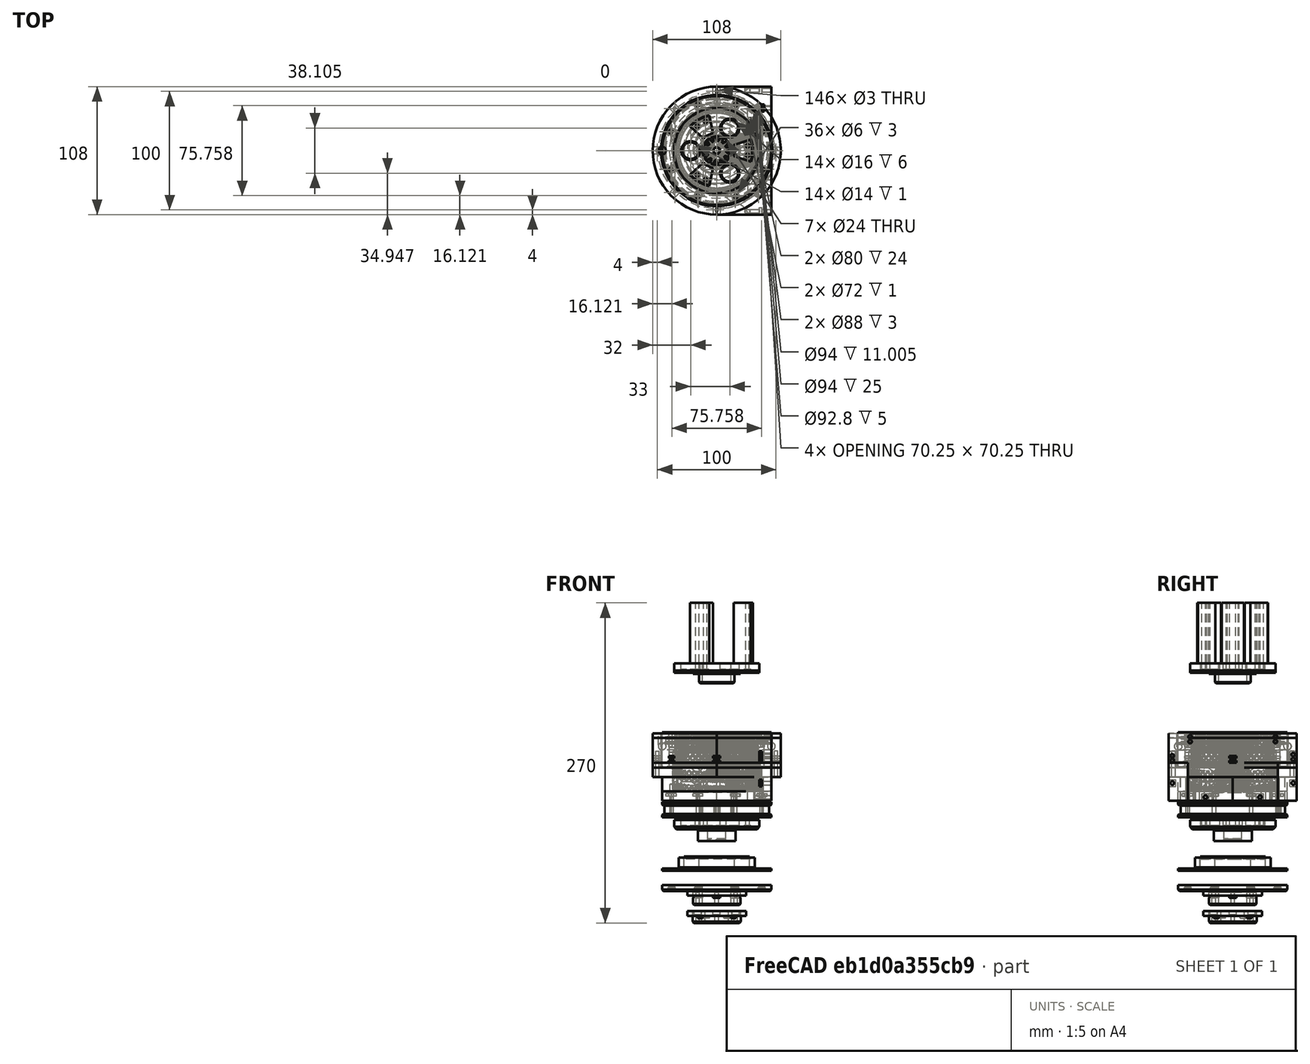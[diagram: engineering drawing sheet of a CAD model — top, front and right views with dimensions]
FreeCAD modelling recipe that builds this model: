
FCSTD DOCUMENT  (FreeCAD 0.19R24276 (Git))
Label: J-midi-deep_048
License: All rights reserved
LicenseURL: http://en.wikipedia.org/wiki/All_rights_reserved
objects: Part::Cylinder×435, Part::Box×228, Part::Compound×200, Part::Cut×185, Part::FeaturePython×106, Part::Chamfer×20, Part::Wedge×20, Mesh::Feature×7, Part::Torus×6, Part::Fillet×2, Part::Mirroring×1, Part::Common×1
note: 1204 computed .brp shape members not serialized (recipe doc carries the construction recipe); baked Part::Feature solids carry a one-line shape summary decoded from their .brp

FEATURE [Part::Cylinder] Cylinder714  label="Válec714"
  Angle = 360
  AttacherType = Attacher::AttachEngine3D
  Height = 60
  Placement = pos=(41,0,-54) rot=(0,0,1;0rad)
  Radius = 1.5
FEATURE [Part::Cylinder] Cylinder715  label="Válec715"
  Angle = 360
  AttacherType = Attacher::AttachEngine3D
  Height = 40
  Placement = pos=(202,50,-28) rot=(0,0,1;0rad)
  Radius = 12
FEATURE [Part::Box] Box334  label="Krychle334"
  AttacherType = Attacher::AttachEngine3D
  Height = 2
  Length = 8
  Placement = pos=(37,-3,-4) rot=(0,0,1;0rad)
  Width = 6
FEATURE [Part::Cylinder] Cylinder716  label="Válec716"
  Angle = 360
  AttacherType = Attacher::AttachEngine3D
  Height = 40
  Placement = pos=(214,56,-30) rot=(0,0,1;0rad)
  Radius = 12
FEATURE [Part::Cylinder] Cylinder717  label="Válec717"
  Angle = 360
  AttacherType = Attacher::AttachEngine3D
  Height = 12
  Radius = 46
FEATURE [Part::Box] Box335  label="Krychle335"
  AttacherType = Attacher::AttachEngine3D
  Height = 28
  Length = 6
  Placement = pos=(26,28,-8) rot=(0,0,1;0rad)
  Width = 10
FEATURE [Part::Cylinder] Cylinder718  label="Válec718"
  Angle = 360
  AttacherType = Attacher::AttachEngine3D
  Height = 40
  Placement = pos=(256,0,-30) rot=(0,0,1;0rad)
  Radius = 10
FEATURE [Part::Box] Box336  label="Krychle336"
  AttacherType = Attacher::AttachEngine3D
  Height = 32
  Length = 8
  Placement = pos=(238,0,-8) rot=(0,0,1;0rad)
  Width = 38
FEATURE [Part::Cylinder] Cylinder719  label="Válec719"
  Angle = 360
  AttacherType = Attacher::AttachEngine3D
  Height = 12
  Radius = 54
FEATURE [Part::Box] Box337  label="Krychle337"
  AttacherType = Attacher::AttachEngine3D
  Height = 28
  Length = 6
  Placement = pos=(32,24,-8) rot=(0,0,1;0rad)
  Width = 14
FEATURE [Part::Cylinder] Cylinder720  label="Válec720"
  Angle = 360
  AttacherType = Attacher::AttachEngine3D
  Height = 40
  Placement = pos=(202,50,-28) rot=(0,0,1;0rad)
  Radius = 12
FEATURE [Part::Box] Box338  label="Krychle338"
  AttacherType = Attacher::AttachEngine3D
  Height = 32
  Length = 8
  Placement = pos=(238,0,-8) rot=(0,0,1;0rad)
  Width = 38
FEATURE [Part::Box] Box339  label="Krychle339"
  AttacherType = Attacher::AttachEngine3D
  Height = 2
  Length = 8
  Placement = pos=(28.2843,24.0416,-4) rot=(0,0,1;0.785398rad)
  Width = 6
FEATURE [Part::Box] Box340  label="Krychle340"
  AttacherType = Attacher::AttachEngine3D
  Height = 2
  Length = 8
  Placement = pos=(-28.2843,-24.0416,-4) rot=(0,0,1;3.92699rad)
  Width = 6
FEATURE [Part::Cylinder] Cylinder721  label="Válec721"
  Angle = 360
  AttacherType = Attacher::AttachEngine3D
  Height = 40
  Placement = pos=(214,56,-30) rot=(0,0,1;0rad)
  Radius = 12
FEATURE [Part::Box] Box341  label="Krychle341"
  AttacherType = Attacher::AttachEngine3D
  Height = 28
  Length = 6
  Placement = pos=(26,28,-8) rot=(0,0,1;0rad)
  Width = 10
FEATURE [Part::Compound] Compound705
  Links = -> [Box341,Box337]
FEATURE [Part::Box] Box342  label="Krychle342"
  AttacherType = Attacher::AttachEngine3D
  Height = 32
  Length = 46
  Placement = pos=(200,38,-8) rot=(0,0,1;0rad)
  Width = 16
FEATURE [Part::Compound] Compound709
  Links = -> [Box336,Box342]
FEATURE [Part::Box] Box343  label="Krychle343"
  AttacherType = Attacher::AttachEngine3D
  Height = 28
  Length = 6
  Placement = pos=(32,24,-8) rot=(0,0,1;0rad)
  Width = 14
FEATURE [Part::Box] Box344  label="Krychle344"
  AttacherType = Attacher::AttachEngine3D
  Height = 2
  Length = 8
  Placement = pos=(3,37,-4) rot=(0,0,1;1.5708rad)
  Width = 6
FEATURE [Part::Cylinder] Cylinder722  label="Válec722"
  Angle = 360
  AttacherType = Attacher::AttachEngine3D
  Height = 40
  Placement = pos=(256,0,-30) rot=(0,0,1;0rad)
  Radius = 10
FEATURE [Part::Cylinder] Cylinder723  label="Válec723"
  Angle = 360
  AttacherType = Attacher::AttachEngine3D
  Height = 60
  Placement = pos=(28.9914,28.9914,-54) rot=(0,0,1;0.785398rad)
  Radius = 1.5
FEATURE [Part::Box] Box345  label="Krychle345"
  AttacherType = Attacher::AttachEngine3D
  Height = 32
  Length = 46
  Placement = pos=(200,38,-8) rot=(0,0,1;0rad)
  Width = 16
FEATURE [Part::Compound] Compound706
  Links = -> [Box338,Box345]
FEATURE [Part::Box] Box346  label="Krychle346"
  AttacherType = Attacher::AttachEngine3D
  Height = 2
  Length = 8
  Placement = pos=(24.0416,-28.2843,-4) rot=(0,0,-1;0.785398rad)
  Width = 6
FEATURE [Part::Cylinder] Cylinder724  label="Válec724"
  Angle = 360
  AttacherType = Attacher::AttachEngine3D
  Height = 60
  Placement = pos=(28.9914,-28.9914,-54) rot=(0,0,-1;0.785398rad)
  Radius = 1.5
FEATURE [Part::Box] Box347  label="Krychle347"
  AttacherType = Attacher::AttachEngine3D
  Height = 2
  Length = 8
  Placement = pos=(-3,-37,-4) rot=(0,0,-1;1.5708rad)
  Width = 6
FEATURE [Part::Cylinder] Cylinder725  label="Válec725"
  Angle = 360
  AttacherType = Attacher::AttachEngine3D
  Height = 60
  Placement = pos=(-41,-1.1e-14,-54) rot=(0,0,1;3.14159rad)
  Radius = 1.5
FEATURE [Part::Cylinder] Cylinder726  label="Válec726"
  Angle = 360
  AttacherType = Attacher::AttachEngine3D
  Height = 60
  Placement = pos=(1.2e-14,-41,-54) rot=(0,0,-1;1.5708rad)
  Radius = 1.5
FEATURE [Part::Cylinder] Cylinder727  label="Válec727"
  Angle = 360
  AttacherType = Attacher::AttachEngine3D
  Height = 60
  Placement = pos=(-28.9914,-28.9914,-54) rot=(0,0,1;3.92699rad)
  Radius = 1.5
FEATURE [Part::Cylinder] Cylinder728  label="Válec728"
  Angle = 360
  AttacherType = Attacher::AttachEngine3D
  Height = 60
  Placement = pos=(28.9914,-28.9914,-54) rot=(0,0,-1;0.785398rad)
  Radius = 1.5
FEATURE [Part::Box] Box348  label="Krychle348"
  AttacherType = Attacher::AttachEngine3D
  Height = 2
  Length = 8
  Placement = pos=(37,-3,-4) rot=(0,0,1;0rad)
  Width = 6
FEATURE [Part::Cylinder] Cylinder729  label="Válec729"
  Angle = 360
  AttacherType = Attacher::AttachEngine3D
  Height = 60
  Placement = pos=(41,0,-54) rot=(0,0,1;0rad)
  Radius = 1.5
FEATURE [Part::Box] Box349  label="Krychle349"
  AttacherType = Attacher::AttachEngine3D
  Height = 2
  Length = 8
  Placement = pos=(-37,3,-4) rot=(0,0,1;3.14159rad)
  Width = 6
FEATURE [Part::Cylinder] Cylinder730  label="Válec730"
  Angle = 360
  AttacherType = Attacher::AttachEngine3D
  Height = 60
  Placement = pos=(1.2e-14,-41,-54) rot=(0,0,-1;1.5708rad)
  Radius = 1.5
FEATURE [Part::Box] Box350  label="Krychle350"
  AttacherType = Attacher::AttachEngine3D
  Height = 2
  Length = 8
  Placement = pos=(28.2843,24.0416,-4) rot=(0,0,1;0.785398rad)
  Width = 6
FEATURE [Part::Box] Box351  label="Krychle351"
  AttacherType = Attacher::AttachEngine3D
  Height = 2
  Length = 8
  Placement = pos=(-28.2843,-24.0416,-4) rot=(0,0,1;3.92699rad)
  Width = 6
FEATURE [Part::Cylinder] Cylinder731  label="Válec731"
  Angle = 360
  AttacherType = Attacher::AttachEngine3D
  Height = 60
  Placement = pos=(-4e-15,41,-54) rot=(0,0,1;1.5708rad)
  Radius = 1.5
FEATURE [Part::Box] Box352  label="Krychle352"
  AttacherType = Attacher::AttachEngine3D
  Height = 2
  Length = 8
  Placement = pos=(-3,-37,-4) rot=(0,0,-1;1.5708rad)
  Width = 6
FEATURE [Part::Box] Box353  label="Krychle353"
  AttacherType = Attacher::AttachEngine3D
  Height = 2
  Length = 8
  Placement = pos=(-24.0416,28.2843,-4) rot=(0,0,1;2.35619rad)
  Width = 6
FEATURE [Part::Cylinder] Cylinder732  label="Válec732"
  Angle = 360
  AttacherType = Attacher::AttachEngine3D
  Height = 60
  Placement = pos=(-28.9914,28.9914,-54) rot=(0,0,1;2.35619rad)
  Radius = 1.5
FEATURE [Part::Cylinder] Cylinder733  label="Válec733"
  Angle = 360
  AttacherType = Attacher::AttachEngine3D
  Height = 60
  Placement = pos=(28.9914,-28.9914,-54) rot=(0,0,-1;0.785398rad)
  Radius = 1.5
FEATURE [Part::Box] Box354  label="Krychle354"
  AttacherType = Attacher::AttachEngine3D
  Height = 2
  Length = 8
  Placement = pos=(-24.0416,28.2843,-4) rot=(0,0,1;2.35619rad)
  Width = 6
FEATURE [Part::Cylinder] Cylinder734  label="Válec734"
  Angle = 360
  AttacherType = Attacher::AttachEngine3D
  Height = 60
  Placement = pos=(-41,-1.1e-14,-54) rot=(0,0,1;3.14159rad)
  Radius = 1.5
FEATURE [Part::Cylinder] Cylinder735  label="Válec735"
  Angle = 360
  AttacherType = Attacher::AttachEngine3D
  Height = 60
  Placement = pos=(28.9914,28.9914,-54) rot=(0,0,1;0.785398rad)
  Radius = 1.5
FEATURE [Part::Box] Box355  label="Krychle355"
  AttacherType = Attacher::AttachEngine3D
  Height = 2
  Length = 8
  Placement = pos=(24.0416,-28.2843,-4) rot=(0,0,-1;0.785398rad)
  Width = 6
FEATURE [Part::Cylinder] Cylinder736  label="Válec736"
  Angle = 360
  AttacherType = Attacher::AttachEngine3D
  Height = 60
  Placement = pos=(-28.9914,28.9914,-54) rot=(0,0,1;2.35619rad)
  Radius = 1.5
FEATURE [Part::Cylinder] Cylinder737  label="Válec737"
  Angle = 360
  AttacherType = Attacher::AttachEngine3D
  Height = 60
  Placement = pos=(-4e-15,41,-54) rot=(0,0,1;1.5708rad)
  Radius = 1.5
FEATURE [Part::Box] Box356  label="Krychle356"
  AttacherType = Attacher::AttachEngine3D
  Height = 2
  Length = 8
  Placement = pos=(3,37,-4) rot=(0,0,1;1.5708rad)
  Width = 6
FEATURE [Part::Cylinder] Cylinder738  label="Válec738"
  Angle = 360
  AttacherType = Attacher::AttachEngine3D
  Height = 60
  Placement = pos=(-28.9914,-28.9914,-54) rot=(0,0,1;3.92699rad)
  Radius = 1.5
FEATURE [Part::Cylinder] Cylinder739  label="Válec739"
  Angle = 360
  AttacherType = Attacher::AttachEngine3D
  Height = 60
  Placement = pos=(28,-51,7) rot=(0,1,0;1.5708rad)
  Radius = 1.5
FEATURE [Part::Cylinder] Cylinder740  label="Válec740"
  Angle = 360
  AttacherType = Attacher::AttachEngine3D
  Height = 60
  Placement = pos=(-4e-15,41,-54) rot=(0,0,1;1.5708rad)
  Radius = 1.5
FEATURE [Part::Box] Box357  label="Krychle357"
  AttacherType = Attacher::AttachEngine3D
  Height = 2
  Length = 8
  Placement = pos=(-37,3,-4) rot=(0,0,1;3.14159rad)
  Width = 6
FEATURE [Part::Box] Box358  label="Krychle358"
  AttacherType = Attacher::AttachEngine3D
  Height = 6
  Length = 2
  Placement = pos=(36,18,-8) rot=(0,0,1;0rad)
  Width = 6
FEATURE [Part::Box] Box359  label="Krychle359"
  AttacherType = Attacher::AttachEngine3D
  Height = 6
  Length = 2
  Placement = pos=(32,-54,4) rot=(0,0,1;0rad)
  Width = 6
FEATURE [Part::Cylinder] Cylinder741  label="Válec741"
  Angle = 360
  AttacherType = Attacher::AttachEngine3D
  Height = 50
  Placement = pos=(-50,-2.3e-14,-15) rot=(0,0,1;3.14159rad)
  Radius = 1.5
FEATURE [Part::Cylinder] Cylinder742  label="Válec742"
  Angle = 360
  AttacherType = Attacher::AttachEngine3D
  Height = 60
  Placement = pos=(28,51,7) rot=(0,1,0;1.5708rad)
  Radius = 1.5
FEATURE [Part::Box] Box360  label="Krychle360"
  AttacherType = Attacher::AttachEngine3D
  Height = 6
  Length = 2
  Placement = pos=(36,20,-8) rot=(0,0,1;0rad)
  Width = 6
FEATURE [Part::Cylinder] Cylinder743  label="Válec743"
  Angle = 360
  AttacherType = Attacher::AttachEngine3D
  Height = 60
  Placement = pos=(41,0,-54) rot=(0,0,1;0rad)
  Radius = 1.5
FEATURE [Part::Cylinder] Cylinder744  label="Válec744"
  Angle = 360
  AttacherType = Attacher::AttachEngine3D
  Height = 60
  Placement = pos=(-28.9914,-28.9914,-54) rot=(0,0,1;3.92699rad)
  Radius = 1.5
FEATURE [Part::Cylinder] Cylinder745  label="Válec745"
  Angle = 360
  AttacherType = Attacher::AttachEngine3D
  Height = 60
  Placement = pos=(28,-51,7) rot=(0,1,0;1.5708rad)
  Radius = 1.5
FEATURE [Part::Box] Box361  label="Krychle361"
  AttacherType = Attacher::AttachEngine3D
  Height = 6
  Length = 2
  Placement = pos=(32,-54,4) rot=(0,0,1;0rad)
  Width = 6
FEATURE [Part::Cylinder] Cylinder746  label="Válec746"
  Angle = 360
  AttacherType = Attacher::AttachEngine3D
  Height = 60
  Placement = pos=(-28.9914,28.9914,-54) rot=(0,0,1;2.35619rad)
  Radius = 1.5
FEATURE [Part::Cylinder] Cylinder747  label="Válec747"
  Angle = 360
  AttacherType = Attacher::AttachEngine3D
  Height = 60
  Placement = pos=(32,-21,-5) rot=(0,1,0;1.5708rad)
  Radius = 1.5
FEATURE [Part::Box] Box362  label="Krychle362"
  AttacherType = Attacher::AttachEngine3D
  Height = 6
  Length = 2
  Placement = pos=(36,-24,-8) rot=(0,0,1;0rad)
  Width = 6
FEATURE [Part::Cylinder] Cylinder748  label="Válec748"
  Angle = 360
  AttacherType = Attacher::AttachEngine3D
  Height = 60
  Placement = pos=(1.2e-14,-41,-54) rot=(0,0,-1;1.5708rad)
  Radius = 1.5
FEATURE [Part::Box] Box363  label="Krychle363"
  AttacherType = Attacher::AttachEngine3D
  Height = 6
  Length = 2
  Placement = pos=(32,48,4) rot=(0,0,1;0rad)
  Width = 6
FEATURE [Part::Compound] Compound703
  Links = -> [Box358,Box362,Box363,Box359]
FEATURE [Part::Cylinder] Cylinder749  label="Válec749"
  Angle = 360
  AttacherType = Attacher::AttachEngine3D
  Height = 60
  Placement = pos=(28.9914,28.9914,-54) rot=(0,0,1;0.785398rad)
  Radius = 1.5
FEATURE [Part::Cylinder] Cylinder750  label="Válec750"
  Angle = 360
  AttacherType = Attacher::AttachEngine3D
  Height = 60
  Placement = pos=(32,21,-5) rot=(0,1,0;1.5708rad)
  Radius = 1.5
FEATURE [Part::Compound] Compound710
  Links = -> [Cylinder750,Cylinder747,Cylinder742,Cylinder739]
FEATURE [Part::Cylinder] Cylinder751  label="Válec751"
  Angle = 360
  AttacherType = Attacher::AttachEngine3D
  Height = 60
  Placement = pos=(-41,-1.1e-14,-54) rot=(0,0,1;3.14159rad)
  Radius = 1.5
FEATURE [Part::Cylinder] Cylinder752  label="Válec752"
  Angle = 360
  AttacherType = Attacher::AttachEngine3D
  Height = 50
  Placement = pos=(50,0,-15) rot=(0,0,1;0rad)
  Radius = 1.5
FEATURE [Part::Box] Box364  label="Krychle364"
  AttacherType = Attacher::AttachEngine3D
  Height = 6
  Length = 2
  Placement = pos=(32,48,4) rot=(0,0,1;0rad)
  Width = 6
FEATURE [Part::Box] Box365  label="Krychle365"
  AttacherType = Attacher::AttachEngine3D
  Height = 6
  Length = 2
  Placement = pos=(36,-26,-8) rot=(0,0,1;0rad)
  Width = 6
FEATURE [Part::Cylinder] Cylinder753  label="Válec753"
  Angle = 360
  AttacherType = Attacher::AttachEngine3D
  Height = 60
  Placement = pos=(32,23,-5) rot=(0,1,0;1.5708rad)
  Radius = 1.5
FEATURE [Part::Cylinder] Cylinder754  label="Válec754"
  Angle = 360
  AttacherType = Attacher::AttachEngine3D
  Height = 50
  Placement = pos=(2.5e-14,-50,-15) rot=(0,0,-1;1.5708rad)
  Radius = 1.5
FEATURE [Part::Cylinder] Cylinder755  label="Válec755"
  Angle = 360
  AttacherType = Attacher::AttachEngine3D
  Height = 50
  Placement = pos=(-35.3553,-35.3553,-15) rot=(0,0,1;3.92699rad)
  Radius = 1.5
FEATURE [Part::Cylinder] Cylinder756  label="Válec756"
  Angle = 360
  AttacherType = Attacher::AttachEngine3D
  Height = 50
  Placement = pos=(35.3553,-35.3553,-15) rot=(0,0,-1;0.785398rad)
  Radius = 1.5
FEATURE [Part::Cylinder] Cylinder757  label="Válec757"
  Angle = 360
  AttacherType = Attacher::AttachEngine3D
  Height = 60
  Placement = pos=(28,51,7) rot=(0,1,0;1.5708rad)
  Radius = 1.5
FEATURE [Part::Cylinder] Cylinder758  label="Válec758"
  Angle = 360
  AttacherType = Attacher::AttachEngine3D
  Height = 50
  Placement = pos=(-35.3553,35.3553,-15) rot=(0,0,1;2.35619rad)
  Radius = 1.5
FEATURE [Part::Cylinder] Cylinder759  label="Válec759"
  Angle = 360
  AttacherType = Attacher::AttachEngine3D
  Height = 50
  Placement = pos=(35.3553,35.3553,-15) rot=(0,0,1;0.785398rad)
  Radius = 1.5
FEATURE [Part::Cylinder] Cylinder760  label="Válec760"
  Angle = 360
  AttacherType = Attacher::AttachEngine3D
  Height = 60
  Placement = pos=(32,-23,-5) rot=(0,1,0;1.5708rad)
  Radius = 1.5
FEATURE [Part::Cylinder] Cylinder761  label="Válec761"
  Angle = 360
  AttacherType = Attacher::AttachEngine3D
  Height = 50
  Placement = pos=(50,0,-15) rot=(0,0,1;0rad)
  Radius = 1.5
FEATURE [Part::Box] Box366  label="Krychle366"
  AttacherType = Attacher::AttachEngine3D
  Height = 6
  Length = 2
  Placement = pos=(36,20,-8) rot=(0,0,1;0rad)
  Width = 6
FEATURE [Part::Cylinder] Cylinder762  label="Válec762"
  Angle = 360
  AttacherType = Attacher::AttachEngine3D
  Height = 50
  Placement = pos=(-50,-2.3e-14,-15) rot=(0,0,1;3.14159rad)
  Radius = 1.5
FEATURE [Part::Cylinder] Cylinder763  label="Válec763"
  Angle = 360
  AttacherType = Attacher::AttachEngine3D
  Height = 50
  Placement = pos=(-35.3553,-35.3553,-15) rot=(0,0,1;3.92699rad)
  Radius = 1.5
FEATURE [Part::Cylinder] Cylinder764  label="Válec764"
  Angle = 360
  AttacherType = Attacher::AttachEngine3D
  Height = 50
  Placement = pos=(-7e-15,50,-15) rot=(0,0,1;1.5708rad)
  Radius = 1.5
FEATURE [Part::Cylinder] Cylinder765  label="Válec765"
  Angle = 360
  AttacherType = Attacher::AttachEngine3D
  Height = 50
  Placement = pos=(35.3553,-35.3553,-15) rot=(0,0,-1;0.785398rad)
  Radius = 1.5
FEATURE [Part::Box] Box367  label="Krychle367"
  AttacherType = Attacher::AttachEngine3D
  Height = 6
  Length = 2
  Placement = pos=(36,-26,-8) rot=(0,0,1;0rad)
  Width = 6
FEATURE [Part::Box] Box368  label="Krychle368"
  AttacherType = Attacher::AttachEngine3D
  Height = 6
  Length = 2
  Placement = pos=(36,48,4) rot=(0,0,1;0rad)
  Width = 6
FEATURE [Part::Cylinder] Cylinder766  label="Válec766"
  Angle = 360
  AttacherType = Attacher::AttachEngine3D
  Height = 50
  Placement = pos=(-35.3553,35.3553,-15) rot=(0,0,1;2.35619rad)
  Radius = 1.5
FEATURE [Part::Cylinder] Cylinder767  label="Válec767"
  Angle = 360
  AttacherType = Attacher::AttachEngine3D
  Height = 50
  Placement = pos=(-7e-15,50,-15) rot=(0,0,1;1.5708rad)
  Radius = 1.5
FEATURE [Part::Cylinder] Cylinder768  label="Válec768"
  Angle = 360
  AttacherType = Attacher::AttachEngine3D
  Height = 50
  Placement = pos=(35.3553,35.3553,-15) rot=(0,0,1;0.785398rad)
  Radius = 1.5
FEATURE [Part::Cylinder] Cylinder769  label="Válec769"
  Angle = 360
  AttacherType = Attacher::AttachEngine3D
  Height = 60
  Placement = pos=(28,51,7) rot=(0,1,0;1.5708rad)
  Radius = 1.5
FEATURE [Part::Compound] Compound704
  Links = -> [Cylinder753,Cylinder760,Cylinder769,Cylinder745]
FEATURE [Part::Cylinder] Cylinder770  label="Válec770"
  Angle = 360
  AttacherType = Attacher::AttachEngine3D
  Height = 60
  Placement = pos=(32,-23,-5) rot=(0,1,0;1.5708rad)
  Radius = 1.5
FEATURE [Part::Cylinder] Cylinder771  label="Válec771"
  Angle = 360
  AttacherType = Attacher::AttachEngine3D
  Height = 50
  Placement = pos=(2.5e-14,-50,-15) rot=(0,0,-1;1.5708rad)
  Radius = 1.5
FEATURE [Part::Box] Box369  label="Krychle369"
  AttacherType = Attacher::AttachEngine3D
  Height = 6
  Length = 2
  Placement = pos=(36,-54,4) rot=(0,0,1;0rad)
  Width = 6
FEATURE [Part::Cylinder] Cylinder772  label="Válec772"
  Angle = 360
  AttacherType = Attacher::AttachEngine3D
  Height = 60
  Placement = pos=(28,-51,7) rot=(0,1,0;1.5708rad)
  Radius = 1.5
FEATURE [Part::Cylinder] Cylinder773  label="Válec773"
  Angle = 360
  AttacherType = Attacher::AttachEngine3D
  Height = 50
  Placement = pos=(35.36,35.36,-40) rot=(0,0,1;0.785398rad)
  Radius = 4
FEATURE [Part::Cylinder] Cylinder774  label="Válec774"
  Angle = 360
  AttacherType = Attacher::AttachEngine3D
  Height = 60
  Placement = pos=(32,23,-5) rot=(0,1,0;1.5708rad)
  Radius = 1.5
FEATURE [Part::Cylinder] Cylinder775  label="Válec775"
  Angle = 360
  AttacherType = Attacher::AttachEngine3D
  Height = 50
  Placement = pos=(35.36,-35.36,-40) rot=(0,0,1;0.785398rad)
  Radius = 4
FEATURE [Part::FeaturePython] wormgear040  # WARN: FeaturePython — macro-defined, semantics opaque (R4)
  AttacherType = Attacher::AttachEngine3D
  Placement = pos=(0,0,0) rot=(0,0,-1;0.107861rad)
  beta = 39.4866
  clearance = 0.25
  diameter = 71
  head = 0
  height = 20
  module = 1.5
  pressure_angle = 20
  reverse_pitch = true
  teeth = 39
  version = 0.0.3
FEATURE [Part::FeaturePython] wormgear041  # WARN: FeaturePython — macro-defined, semantics opaque (R4)
  AttacherType = Attacher::AttachEngine3D
  beta = 39.4866
  clearance = 0.25
  diameter = 71
  head = 0
  height = 20
  module = 1.5
  pressure_angle = 20
  reverse_pitch = false
  teeth = 39
  version = 0.0.3
FEATURE [Part::FeaturePython] Tube077  # WARN: FeaturePython — macro-defined, semantics opaque (R4)
  AttacherType = Attacher::AttachEngine3D
  Height = 8
  InnerRadius = 38
  OuterRadius = 46
  Placement = pos=(0,0,-8) rot=(0,0,1;0rad)
FEATURE [Part::Compound] Compound711
  Links = -> [Cylinder722,Cylinder721]
  Placement = pos=(0,0,2) rot=(0,0,1;0rad)
FEATURE [Part::Compound] Compound712
  Links = -> [Box335,Box343]
FEATURE [Part::Compound] Compound713
  Links = -> [Cylinder718,Cylinder716]
  Placement = pos=(0,0,2) rot=(0,0,1;0rad)
FEATURE [Part::Compound] Compound715
  Links = -> [Cylinder774,Cylinder770,Cylinder757,Cylinder772]
FEATURE [Part::Compound] Compound716
  Links = -> [Box350,Box356,Box354,Box357,Box351,Box352,Box355,Box348]
  Placement = pos=(0,0,0) rot=(0,0,1;0.392699rad)
FEATURE [Part::Compound] Compound717
  Links = -> [Cylinder749,Cylinder740,Cylinder746,Cylinder751,Cylinder744,Cylinder748,Cylinder733,Cylinder743]
  Placement = pos=(0,0,0) rot=(0,0,1;0.392699rad)
FEATURE [Part::Compound] Compound719
  Links = -> [Box339,Box344,Box353,Box349,Box340,Box347,Box346,Box334]
  Placement = pos=(0,0,0) rot=(0,0,1;0.392699rad)
FEATURE [Part::Compound] Compound721
  Links = -> [Cylinder773,Cylinder775]
  Placement = pos=(0,0,2) rot=(0,0,1;0rad)
FEATURE [Part::Compound] Compound722
  Links = -> [Cylinder761,Cylinder768,Cylinder764,Cylinder758,Cylinder762,Cylinder763,Cylinder771,Cylinder765]
FEATURE [Part::Compound] Compound723
  Links = -> [Cylinder752,Cylinder759,Cylinder767,Cylinder766,Cylinder741,Cylinder755,Cylinder754,Cylinder756]
FEATURE [Part::Compound] Compound724
  Links = -> [Box366,Box367,Box368,Box369]
FEATURE [Part::Compound] Compound725
  Links = -> [Box360,Box365,Box364,Box361]
FEATURE [Part::Compound] Compound726
  Links = -> [Cylinder735,Cylinder737,Cylinder732,Cylinder734,Cylinder738,Cylinder730,Cylinder724,Cylinder729]
  Placement = pos=(0,0,0) rot=(0,0,1;0.392699rad)
FEATURE [Part::Compound] Compound727
  Links = -> [Cylinder723,Cylinder731,Cylinder736,Cylinder725,Cylinder727,Cylinder726,Cylinder728,Cylinder714]
  Placement = pos=(0,0,0) rot=(0,0,1;0.392699rad)
FEATURE [Part::Cut] Cut337
  Base = -> Compound706
  Tool = -> Compound711
FEATURE [Part::Cut] Cut338
  Base = -> Cylinder717
  Tool = -> wormgear041
FEATURE [Part::Cut] Cut339
  Base = -> Cylinder719
  Placement = pos=(0,0,12) rot=(0,0,1;0.034907rad)
  Tool = -> wormgear040
FEATURE [Part::Compound] Compound707
  Links = -> [Cut339,Cut338]
FEATURE [Part::Cut] Cut335
  Base = -> Compound707
  Tool = -> Compound717
FEATURE [Part::Cut] Cut333
  Base = -> Cut335
  Tool = -> Compound710
FEATURE [Part::Cut] Cut340
  Base = -> Compound709
  Tool = -> Compound713
FEATURE [Part::Cut] Cut331
  Base = -> Cut340
  Placement = pos=(-200,0,0) rot=(0,0,1;0rad)
  Tool = -> Cylinder720
FEATURE [Part::Compound] Compound708
  Links = -> [Cut331,Compound705]
FEATURE [Part::Cut] Cut341
  Base = -> Tube077
  Tool = -> Compound727
FEATURE [Part::Cut] Cut344
  Base = -> Cut333
  Tool = -> Compound703
FEATURE [Part::Cut] Cut332
  Base = -> Cut344
  Tool = -> Compound723
FEATURE [Part::Cut] Cut345
  Base = -> Cut337
  Placement = pos=(-200,0,0) rot=(0,0,1;0rad)
  Tool = -> Cylinder715
FEATURE [Part::Compound] Compound714
  Links = -> [Cut345,Compound712]
FEATURE [Part::Mirroring] mirror012  label="Compound196 (mirrored)001"
  Base = (0,0,0)
  Normal = (1e-16,-1,0)
  Source = -> Compound714
FEATURE [Part::Compound] Compound720
  Links = -> [mirror012,Compound708]
FEATURE [Part::Cut] Cut342
  Base = -> Compound720
  Tool = -> Compound716
FEATURE [Part::Cut] Cut336
  Base = -> Cut342
  Tool = -> Compound726
FEATURE [Part::Cut] Cut346
  Base = -> Cut336
  Tool = -> Compound722
FEATURE [Part::Cut] Cut334
  Base = -> Cut346
  Tool = -> Compound724
FEATURE [Part::Cut] Cut343
  Base = -> Cut334
  Tool = -> Compound715
FEATURE [Part::Cut] Cut347
  Base = -> Cut343
  Tool = -> Compound721
FEATURE [Part::Fillet] Fillet022
  Base = -> Cut347
  Edges = 1 edges r=8: [Edge273]
FEATURE [Part::Fillet] Fillet021
  Base = -> Fillet022
  Edges = 1 edges r=8: [Edge173]
FEATURE [Part::Cut] Cut350
  Base = -> Cut341
  Tool = -> Compound719
FEATURE [Part::Cut] Cut349
  Base = -> Cut350
  Tool = -> Compound725
FEATURE [Part::Cut] Cut348
  Base = -> Cut349
  Tool = -> Compound704
FEATURE [Part::Compound] Compound  label="J-midi-deep_monoblok"
  Links = -> [Cut332,Fillet021,Cut348]
FEATURE [Part::Box] Box157  label="Krychle157"
  AttacherType = Attacher::AttachEngine3D
  Height = 2
  Length = 8
  Placement = pos=(46,-3,23) rot=(0,0,1;0rad)
  Width = 6
FEATURE [Part::Cylinder] Cylinder006  label="Válec006"
  Angle = 360
  AttacherType = Attacher::AttachEngine3D
  Height = 16
  Placement = pos=(-45.6,0,34) rot=(0,0,1;0rad)
  Radius = 3.5
FEATURE [Part::Box] Box156  label="Krychle156"
  AttacherType = Attacher::AttachEngine3D
  Height = 25
  Length = 46
  Placement = pos=(0,-54,20) rot=(0,0,1;0rad)
  Width = 108
FEATURE [Part::Box] Box158  label="Krychle158"
  AttacherType = Attacher::AttachEngine3D
  Height = 2
  Length = 8
  Placement = pos=(34.6482,30.4056,23) rot=(0,0,1;0.785398rad)
  Width = 6
FEATURE [Part::Box] Box159  label="Krychle159"
  AttacherType = Attacher::AttachEngine3D
  Height = 2
  Length = 8
  Placement = pos=(3,46,23) rot=(0,0,1;1.5708rad)
  Width = 6
FEATURE [Part::Box] Box160  label="Krychle160"
  AttacherType = Attacher::AttachEngine3D
  Height = 2
  Length = 8
  Placement = pos=(-30.4056,34.6482,23) rot=(0,0,1;2.35619rad)
  Width = 6
FEATURE [Part::Box] Box161  label="Krychle161"
  AttacherType = Attacher::AttachEngine3D
  Height = 2
  Length = 8
  Placement = pos=(-46,3,23) rot=(0,0,1;3.14159rad)
  Width = 6
FEATURE [Part::Cylinder] Cylinder374  label="Válec374"
  Angle = 360
  AttacherType = Attacher::AttachEngine3D
  Height = 50
  Placement = pos=(50,0,-15) rot=(0,0,1;0rad)
  Radius = 1.5
FEATURE [Part::Cylinder] Cylinder375  label="Válec375"
  Angle = 360
  AttacherType = Attacher::AttachEngine3D
  Height = 50
  Placement = pos=(35.3553,35.3553,-15) rot=(0,0,1;0.785398rad)
  Radius = 1.5
FEATURE [Part::Cylinder] Cylinder376  label="Válec376"
  Angle = 360
  AttacherType = Attacher::AttachEngine3D
  Height = 50
  Placement = pos=(-7e-15,50,-15) rot=(0,0,1;1.5708rad)
  Radius = 1.5
FEATURE [Part::Box] Box162  label="Krychle162"
  AttacherType = Attacher::AttachEngine3D
  Height = 2
  Length = 8
  Placement = pos=(-34.6482,-30.4056,23) rot=(0,0,1;3.92699rad)
  Width = 6
FEATURE [Part::Box] Box163  label="Krychle163"
  AttacherType = Attacher::AttachEngine3D
  Height = 2
  Length = 8
  Placement = pos=(-3,-46,23) rot=(0,0,-1;1.5708rad)
  Width = 6
FEATURE [Part::Box] Box164  label="Krychle164"
  AttacherType = Attacher::AttachEngine3D
  Height = 2
  Length = 8
  Placement = pos=(30.4056,-34.6482,23) rot=(0,0,-1;0.785398rad)
  Width = 6
FEATURE [Part::Compound] Compound297
  Links = -> [Box157,Box158,Box159,Box160,Box161,Box162,Box163,Box164]
  Placement = pos=(0,0,1) rot=(0,0,1;0rad)
FEATURE [Part::Cylinder] Cylinder377  label="Válec377"
  Angle = 360
  AttacherType = Attacher::AttachEngine3D
  Height = 50
  Placement = pos=(-35.3553,35.3553,-15) rot=(0,0,1;2.35619rad)
  Radius = 1.5
FEATURE [Part::Cylinder] Cylinder378  label="Válec378"
  Angle = 360
  AttacherType = Attacher::AttachEngine3D
  Height = 50
  Placement = pos=(-50,-2.3e-14,-15) rot=(0,0,1;3.14159rad)
  Radius = 1.5
FEATURE [Part::Cylinder] Cylinder379  label="Válec379"
  Angle = 360
  AttacherType = Attacher::AttachEngine3D
  Height = 50
  Placement = pos=(-35.3553,-35.3553,-15) rot=(0,0,1;3.92699rad)
  Radius = 1.5
FEATURE [Part::Cylinder] Cylinder380  label="Válec380"
  Angle = 360
  AttacherType = Attacher::AttachEngine3D
  Height = 50
  Placement = pos=(2.5e-14,-50,-15) rot=(0,0,-1;1.5708rad)
  Radius = 1.5
FEATURE [Part::Cylinder] Cylinder381  label="Válec381"
  Angle = 360
  AttacherType = Attacher::AttachEngine3D
  Height = 50
  Placement = pos=(35.3553,-35.3553,-15) rot=(0,0,-1;0.785398rad)
  Radius = 1.5
FEATURE [Part::Compound] Compound298
  Links = -> [Cylinder374,Cylinder375,Cylinder376,Cylinder377,Cylinder378,Cylinder379,Cylinder380,Cylinder381]
  Placement = pos=(0,0,-5) rot=(0,0,1;0rad)
FEATURE [Part::Box] Box165  label="Krychle165"
  AttacherType = Attacher::AttachEngine3D
  Height = 2
  Length = 8
  Placement = pos=(3,46,23) rot=(0,0,1;1.5708rad)
  Width = 6
FEATURE [Part::Box] Box166  label="Krychle166"
  AttacherType = Attacher::AttachEngine3D
  Height = 2
  Length = 8
  Placement = pos=(-30.4056,34.6482,23) rot=(0,0,1;2.35619rad)
  Width = 6
FEATURE [Part::Box] Box167  label="Krychle167"
  AttacherType = Attacher::AttachEngine3D
  Height = 2
  Length = 8
  Placement = pos=(46,-3,23) rot=(0,0,1;0rad)
  Width = 6
FEATURE [Part::Box] Box168  label="Krychle168"
  AttacherType = Attacher::AttachEngine3D
  Height = 2
  Length = 8
  Placement = pos=(-46,3,23) rot=(0,0,1;3.14159rad)
  Width = 6
FEATURE [Part::Box] Box169  label="Krychle169"
  AttacherType = Attacher::AttachEngine3D
  Height = 2
  Length = 8
  Placement = pos=(-34.6482,-30.4056,23) rot=(0,0,1;3.92699rad)
  Width = 6
FEATURE [Part::Box] Box170  label="Krychle170"
  AttacherType = Attacher::AttachEngine3D
  Height = 2
  Length = 8
  Placement = pos=(30.4056,-34.6482,23) rot=(0,0,-1;0.785398rad)
  Width = 6
FEATURE [Part::Box] Box171  label="Krychle171"
  AttacherType = Attacher::AttachEngine3D
  Height = 2
  Length = 8
  Placement = pos=(34.6482,30.4056,23) rot=(0,0,1;0.785398rad)
  Width = 6
FEATURE [Part::Box] Box172  label="Krychle172"
  AttacherType = Attacher::AttachEngine3D
  Height = 2
  Length = 8
  Placement = pos=(-3,-46,23) rot=(0,0,-1;1.5708rad)
  Width = 6
FEATURE [Part::Compound] Compound300
  Links = -> [Box167,Box171,Box165,Box166,Box168,Box169,Box172,Box170]
  Placement = pos=(0,0,1) rot=(0,0,1;0rad)
FEATURE [Part::Cylinder] Cylinder  label="Válec"
  Angle = 360
  AttacherType = Attacher::AttachEngine3D
  Height = 25
  Placement = pos=(0,0,20) rot=(0,0,1;0rad)
  Radius = 47
FEATURE [Part::Box] Box173  label="Krychle173"
  AttacherType = Attacher::AttachEngine3D
  Height = 6
  Length = 2
  Placement = pos=(32,48,24) rot=(0,0,1;0rad)
  Width = 6
FEATURE [Part::Cylinder] Cylinder391  label="Válec391"
  Angle = 360
  AttacherType = Attacher::AttachEngine3D
  Height = 100
  Placement = pos=(24,51,27) rot=(0,1,0;1.5708rad)
  Radius = 1.5
FEATURE [Part::Cylinder] Cylinder392  label="Válec392"
  Angle = 360
  AttacherType = Attacher::AttachEngine3D
  Height = 100
  Placement = pos=(24,-51,26) rot=(0,1,0;1.5708rad)
  Radius = 1.5
FEATURE [Part::Box] Box174  label="Krychle174"
  AttacherType = Attacher::AttachEngine3D
  Height = 6
  Length = 2
  Placement = pos=(32,-54,24) rot=(0,0,1;0rad)
  Width = 6
FEATURE [Part::Box] Box175  label="Krychle175"
  AttacherType = Attacher::AttachEngine3D
  Height = 6
  Length = 2
  Placement = pos=(38,33,39) rot=(0,0,1;0rad)
  Width = 6
FEATURE [Part::Cylinder] Cylinder393  label="Válec393"
  Angle = 360
  AttacherType = Attacher::AttachEngine3D
  Height = 100
  Placement = pos=(34,36,42) rot=(0,1,0;1.5708rad)
  Radius = 1.5
FEATURE [Part::Cylinder] Cylinder394  label="Válec394"
  Angle = 360
  AttacherType = Attacher::AttachEngine3D
  Height = 100
  Placement = pos=(34,-36,42) rot=(0,1,0;1.5708rad)
  Radius = 1.5
FEATURE [Part::Compound] Compound301
  Links = -> [Cylinder391,Cylinder392,Cylinder393,Cylinder394]
FEATURE [Part::Box] Box176  label="Krychle176"
  AttacherType = Attacher::AttachEngine3D
  Height = 6
  Length = 2
  Placement = pos=(38,-39,39) rot=(0,0,1;0rad)
  Width = 6
FEATURE [Part::Compound] Compound302
  Links = -> [Box173,Box174,Box175,Box176]
FEATURE [Part::Cylinder] Cylinder395  label="Válec395"
  Angle = 360
  AttacherType = Attacher::AttachEngine3D
  Height = 100
  Placement = pos=(34,-36,42) rot=(0,1,0;1.5708rad)
  Radius = 1.5
FEATURE [Part::Cylinder] Cylinder396  label="Válec396"
  Angle = 360
  AttacherType = Attacher::AttachEngine3D
  Height = 100
  Placement = pos=(24,51,27) rot=(0,1,0;1.5708rad)
  Radius = 1.5
FEATURE [Part::Cylinder] Cylinder397  label="Válec397"
  Angle = 360
  AttacherType = Attacher::AttachEngine3D
  Height = 100
  Placement = pos=(24,-51,27) rot=(0,1,0;1.5708rad)
  Radius = 1.5
FEATURE [Part::Cylinder] Cylinder398  label="Válec398"
  Angle = 360
  AttacherType = Attacher::AttachEngine3D
  Height = 100
  Placement = pos=(34,36,42) rot=(0,1,0;1.5708rad)
  Radius = 1.5
FEATURE [Part::Compound] Compound303
  Links = -> [Cylinder396,Cylinder397,Cylinder398,Cylinder395]
FEATURE [Part::Box] Box177  label="Krychle177"
  AttacherType = Attacher::AttachEngine3D
  Height = 6
  Length = 2
  Placement = pos=(36,48,24) rot=(0,0,1;0rad)
  Width = 6
FEATURE [Part::Box] Box178  label="Krychle178"
  AttacherType = Attacher::AttachEngine3D
  Height = 6
  Length = 2
  Placement = pos=(36,-54,24) rot=(0,0,1;0rad)
  Width = 6
FEATURE [Part::Box] Box179  label="Krychle179"
  AttacherType = Attacher::AttachEngine3D
  Height = 6
  Length = 2
  Placement = pos=(38,33,39) rot=(0,0,1;0rad)
  Width = 6
FEATURE [Part::Box] Box180  label="Krychle180"
  AttacherType = Attacher::AttachEngine3D
  Height = 6
  Length = 2
  Placement = pos=(38,-39,39) rot=(0,0,1;0rad)
  Width = 6
FEATURE [Part::Compound] Compound304
  Links = -> [Box177,Box178,Box179,Box180]
FEATURE [Part::Torus] Torus004  label="Anuloid004"
  Angle1 = -180
  Angle2 = 180
  Angle3 = 360
  AttacherType = Attacher::AttachEngine3D
  Placement = pos=(0,0,34) rot=(0,0,1;0rad)
  Radius1 = 46.2
  Radius2 = 3.1
FEATURE [Part::Torus] Torus005  label="Anuloid005"
  Angle1 = -180
  Angle2 = 180
  Angle3 = 360
  AttacherType = Attacher::AttachEngine3D
  Placement = pos=(0,0,34) rot=(0,0,1;0rad)
  Radius1 = 46.2
  Radius2 = 3.1
FEATURE [Part::FeaturePython] Tube002  # WARN: FeaturePython — macro-defined, semantics opaque (R4)
  AttacherType = Attacher::AttachEngine3D
  Height = 25
  InnerRadius = 47
  OuterRadius = 54
  Placement = pos=(0,0,20) rot=(0,0,1;0rad)
FEATURE [Part::Cut] Cut153
  Base = -> Box156
  Tool = -> Cylinder
FEATURE [Part::Cut] Cut154
  Base = -> Cut153
  Tool = -> Torus005
FEATURE [Part::Cut] Cut155
  Base = -> Cut154
  Tool = -> Compound298
FEATURE [Part::Cut] Cut156
  Base = -> Cut155
  Tool = -> Compound300
FEATURE [Part::Cut] Cut157
  Base = -> Cut156
  Tool = -> Compound301
FEATURE [Part::Cut] Cut158
  Base = -> Cut157
  Tool = -> Compound304
FEATURE [Part::Cut] Cut009
  Base = -> Tube002
  Tool = -> Torus004
FEATURE [Part::Cut] Cut010
  Base = -> Cut009
  Tool = -> Cylinder006
FEATURE [Part::Cut] Cut151
  Base = -> Cut010
  Tool = -> Compound297
FEATURE [Part::Cut] Cut152
  Base = -> Cut151
  Tool = -> Compound298
FEATURE [Part::Cut] Cut159
  Base = -> Cut152
  Tool = -> Compound303
FEATURE [Part::Cut] Cut160
  Base = -> Cut159
  Tool = -> Compound302
FEATURE [Part::Compound] Compound728  label="J-midi-deep_bearing-ring"
  Links = -> [Cut160,Cut158]
  Placement = pos=(0,0,4) rot=(0,0,1;0rad)
FEATURE [Part::FeaturePython] Tube045  # WARN: FeaturePython — macro-defined, semantics opaque (R4)
  AttacherType = Attacher::AttachEngine3D
  Height = 1
  InnerRadius = 7
  OuterRadius = 8
  Placement = pos=(-22,0,2) rot=(0,0,1;0rad)
FEATURE [Part::FeaturePython] Tube046  # WARN: FeaturePython — macro-defined, semantics opaque (R4)
  AttacherType = Attacher::AttachEngine3D
  Height = 1
  InnerRadius = 7
  OuterRadius = 8
  Placement = pos=(11,-19.0526,2) rot=(0,0,1;2.0944rad)
FEATURE [Part::FeaturePython] Tube047  # WARN: FeaturePython — macro-defined, semantics opaque (R4)
  AttacherType = Attacher::AttachEngine3D
  Height = 1
  InnerRadius = 7
  OuterRadius = 8
  Placement = pos=(0,0,2) rot=(0,0,1;4.18879rad)
FEATURE [Part::FeaturePython] Tube048  # WARN: FeaturePython — macro-defined, semantics opaque (R4)
  AttacherType = Attacher::AttachEngine3D
  Height = 1
  InnerRadius = 7
  OuterRadius = 8
  Placement = pos=(11,19.0526,2) rot=(0,0,1;4.18879rad)
FEATURE [Part::Cylinder] Cylinder632  label="Válec632"
  Angle = 360
  AttacherType = Attacher::AttachEngine3D
  Height = 6
  Placement = pos=(11,19.0526,2) rot=(0,0,1;4.18879rad)
  Radius = 8
FEATURE [Part::Cylinder] Cylinder633  label="Válec633"
  Angle = 360
  AttacherType = Attacher::AttachEngine3D
  Height = 6
  Placement = pos=(-22,0,2) rot=(0,0,1;0rad)
  Radius = 8
FEATURE [Part::Cylinder] Cylinder634  label="Válec634"
  Angle = 360
  AttacherType = Attacher::AttachEngine3D
  Height = 6
  Placement = pos=(11,-19.0526,2) rot=(0,0,1;2.0944rad)
  Radius = 8
FEATURE [Part::Cylinder] Cylinder635  label="Válec635"
  Angle = 360
  AttacherType = Attacher::AttachEngine3D
  Height = 8
  Radius = 36
FEATURE [Part::Cylinder] Cylinder636  label="Válec636"
  Angle = 360
  AttacherType = Attacher::AttachEngine3D
  Height = 6
  Placement = pos=(0,0,2) rot=(0,0,1;0rad)
  Radius = 8
FEATURE [Part::Cylinder] Cylinder637  label="Válec637"
  Angle = 360
  AttacherType = Attacher::AttachEngine3D
  Height = 3
  Placement = pos=(26,-4,-6) rot=(0,0,1;0rad)
  Radius = 3
FEATURE [Part::Cylinder] Cylinder638  label="Válec638"
  Angle = 360
  AttacherType = Attacher::AttachEngine3D
  Height = 60
  Placement = pos=(26,4,-6) rot=(0,0,1;0rad)
  Radius = 1.5
FEATURE [Part::Cylinder] Cylinder639  label="Válec639"
  Angle = 360
  AttacherType = Attacher::AttachEngine3D
  Height = 60
  Placement = pos=(26,-4,-6) rot=(0,0,1;0rad)
  Radius = 1.5
FEATURE [Part::Cylinder] Cylinder640  label="Válec640"
  Angle = 360
  AttacherType = Attacher::AttachEngine3D
  Height = 3
  Placement = pos=(26,4,-6) rot=(0,0,1;0rad)
  Radius = 3
FEATURE [Part::Cylinder] Cylinder641  label="Válec641"
  Angle = 360
  AttacherType = Attacher::AttachEngine3D
  Height = 1
  Placement = pos=(0,0,-1) rot=(0,0,1;0rad)
  Radius = 10
FEATURE [Part::Cylinder] Cylinder642  label="Válec642"
  Angle = 360
  AttacherType = Attacher::AttachEngine3D
  Height = 8
  Placement = pos=(0,0,-9) rot=(0,0,1;0rad)
  Radius = 7.5
FEATURE [Part::Compound] Compound657
  Links = -> [Cylinder638,Cylinder639]
  Placement = pos=(0,0,0) rot=(0,0,1;2.0944rad)
FEATURE [Part::Compound] Compound658
  Links = -> [Cylinder640,Cylinder637]
  Placement = pos=(0,0,6) rot=(0,0,1;2.0944rad)
FEATURE [Part::Compound] Compound659
  Links = -> [Cylinder638,Cylinder639]
  Placement = pos=(0,0,0) rot=(0,0,1;4.18879rad)
FEATURE [Part::Compound] Compound660
  Links = -> [Cylinder638,Cylinder639]
FEATURE [Part::Compound] Compound661
  Links = -> [Compound657,Compound659,Compound660]
FEATURE [Part::Compound] Compound663
  Links = -> [Cylinder640,Cylinder637]
  Placement = pos=(0,0,6) rot=(0,0,1;0rad)
FEATURE [Part::Compound] Compound665
  Links = -> [Cylinder640,Cylinder637]
  Placement = pos=(0,0,6) rot=(0,0,1;4.18879rad)
FEATURE [Part::Compound] Compound664
  Links = -> [Compound658,Compound665,Compound663]
FEATURE [Part::Compound] Compound666
  Links = -> [Cylinder633,Cylinder634,Cylinder632,Cylinder636]
FEATURE [Part::Cut] Cut287
  Base = -> Cylinder635
  Tool = -> Compound666
FEATURE [Part::Cut] Cut286
  Base = -> Cut287
  Tool = -> Compound661
FEATURE [Part::Cut] Cut285
  Base = -> Cut286
  Tool = -> Compound664
FEATURE [Part::Compound] Compound662  label="J-midi_quikovina_fixo2"
  Links = -> [Tube045,Tube047,Tube046,Tube048,Cut285]
FEATURE [Part::Chamfer] Chamfer018
  Base = -> Cylinder642
  Edges = 1 edges r=1: [Edge3]
FEATURE [Part::Compound] Compound667  label="auxi3"
  Links = -> [Chamfer018,Cylinder641,Compound662]
  Placement = pos=(0,0,-32) rot=(0,0,1;0rad)
FEATURE [Part::FeaturePython] Tube050  # WARN: FeaturePython — macro-defined, semantics opaque (R4)
  AttacherType = Attacher::AttachEngine3D
  Height = 51
  InnerRadius = 15
  OuterRadius = 30.5
  Placement = pos=(0,0,8) rot=(0,0,1;0rad)
FEATURE [Part::FeaturePython] Tube049  # WARN: FeaturePython — macro-defined, semantics opaque (R4)
  AttacherType = Attacher::AttachEngine3D
  Height = 1
  InnerRadius = 12
  OuterRadius = 20
  Placement = pos=(0,0,-1) rot=(0,0,1;0rad)
FEATURE [Part::FeaturePython] Tube  # WARN: FeaturePython — macro-defined, semantics opaque (R4)
  AttacherType = Attacher::AttachEngine3D
  Height = 8
  InnerRadius = 12
  OuterRadius = 15
  Placement = pos=(0,0,-9) rot=(0,0,1;0rad)
FEATURE [Part::Cylinder] Cylinder653  label="Válec653"
  Angle = 360
  AttacherType = Attacher::AttachEngine3D
  Height = 6
  Placement = pos=(11,19.0526,2) rot=(0,0,1;4.18879rad)
  Radius = 8
FEATURE [Part::Cylinder] Cylinder652  label="Válec652"
  Angle = 360
  AttacherType = Attacher::AttachEngine3D
  Height = 6
  Placement = pos=(11,-19.0526,2) rot=(0,0,1;2.0944rad)
  Radius = 8
FEATURE [Part::Cylinder] Cylinder651  label="Válec651"
  Angle = 360
  AttacherType = Attacher::AttachEngine3D
  Height = 6
  Placement = pos=(-22,0,2) rot=(0,0,1;0rad)
  Radius = 8
FEATURE [Part::Cylinder] Cylinder650  label="Válec650"
  Angle = 360
  AttacherType = Attacher::AttachEngine3D
  Height = 20
  Placement = pos=(0,0,-4) rot=(0,0,1;0rad)
  Radius = 12
FEATURE [Part::Compound] Compound677
  Links = -> [Cylinder651,Cylinder652,Cylinder653]
FEATURE [Part::FeaturePython] Tube051  # WARN: FeaturePython — macro-defined, semantics opaque (R4)
  AttacherType = Attacher::AttachEngine3D
  Height = 1
  InnerRadius = 7
  OuterRadius = 8
  Placement = pos=(-22,0,2) rot=(0,0,1;0rad)
FEATURE [Part::FeaturePython] Tube052  # WARN: FeaturePython — macro-defined, semantics opaque (R4)
  AttacherType = Attacher::AttachEngine3D
  Height = 1
  InnerRadius = 7
  OuterRadius = 8
  Placement = pos=(11,19.0526,2) rot=(0,0,1;4.18879rad)
FEATURE [Part::FeaturePython] Tube053  # WARN: FeaturePython — macro-defined, semantics opaque (R4)
  AttacherType = Attacher::AttachEngine3D
  Height = 1
  InnerRadius = 7
  OuterRadius = 8
  Placement = pos=(11,-19.0526,2) rot=(0,0,1;2.0944rad)
FEATURE [Part::Compound] Compound680
  Links = -> [Tube053,Tube052,Tube051]
FEATURE [Part::Box] Box298  label="Krychle298"
  AttacherType = Attacher::AttachEngine3D
  Height = 60
  Length = 50
  Placement = pos=(0,0,8) rot=(0,0,1;4.18879rad)
  Width = 100
FEATURE [Part::Cut] Cut290
  Base = -> Tube050
  Tool = -> Box298
FEATURE [Part::Box] Box299  label="Krychle299"
  AttacherType = Attacher::AttachEngine3D
  Height = 60
  Length = 50
  Placement = pos=(0,0,8) rot=(0,0,1;1.36136rad)
  Width = 50
FEATURE [Part::Box] Box300  label="Krychle300"
  AttacherType = Attacher::AttachEngine3D
  Height = 60
  Length = 50
  Placement = pos=(0,0,8) rot=(0,0,1;2.61799rad)
  Width = 100
FEATURE [Part::Cut] Cut292
  Base = -> Cut290
  Tool = -> Box300
FEATURE [Part::Box] Box301  label="Krychle301"
  AttacherType = Attacher::AttachEngine3D
  Height = 60
  Length = 50
  Placement = pos=(0,0,8) rot=(0,0,-1;0.837758rad)
  Width = 50
FEATURE [Part::Cut] Cut288
  Base = -> Cut292
  Tool = -> Box301
FEATURE [Part::Cut] Cut289
  Base = -> Cut288
  Tool = -> Box299
FEATURE [Part::Cylinder] Cylinder649  label="Válec649"
  Angle = 360
  AttacherType = Attacher::AttachEngine3D
  Height = 8
  Radius = 36
FEATURE [Part::Cut] Cut295
  Base = -> Cylinder649
  Tool = -> Cylinder650
FEATURE [Part::Cut] Cut296
  Base = -> Cut295
  Tool = -> Compound677
FEATURE [Part::Cylinder] Cylinder643  label="Válec643"
  Angle = 360
  AttacherType = Attacher::AttachEngine3D
  Height = 3
  Placement = pos=(26,4,-6) rot=(0,0,1;0rad)
  Radius = 3
FEATURE [Part::Cylinder] Cylinder644  label="Válec644"
  Angle = 360
  AttacherType = Attacher::AttachEngine3D
  Height = 80
  Placement = pos=(26,4,-6) rot=(0,0,1;0rad)
  Radius = 1.45
FEATURE [Part::Cylinder] Cylinder645  label="Válec645"
  Angle = 360
  AttacherType = Attacher::AttachEngine3D
  Height = 80
  Placement = pos=(26,-4,-6) rot=(0,0,1;0rad)
  Radius = 1.45
FEATURE [Part::Compound] Compound673
  Links = -> [Cylinder644,Cylinder645]
  Placement = pos=(0,0,0) rot=(0,0,1;1.0472rad)
FEATURE [Part::Cut] Cut298
  Base = -> Cut289
  Placement = pos=(0,0,0) rot=(0,0,1;3.14159rad)
  Tool = -> Compound673
FEATURE [Part::Cut] Cut291
  Base = -> Cut289
  Placement = pos=(0,0,0) rot=(0,0,1;1.0472rad)
  Tool = -> Compound673
FEATURE [Part::Cut] Cut294
  Base = -> Cut289
  Placement = pos=(0,0,0) rot=(0,0,-1;1.0472rad)
  Tool = -> Compound673
FEATURE [Part::Compound] Compound678
  Links = -> [Cut294,Cut298,Cut291]
FEATURE [Part::Cylinder] Cylinder646  label="Válec646"
  Angle = 360
  AttacherType = Attacher::AttachEngine3D
  Height = 60
  Placement = pos=(26,4,-6) rot=(0,0,1;0rad)
  Radius = 1.45
FEATURE [Part::Cylinder] Cylinder647  label="Válec647"
  Angle = 360
  AttacherType = Attacher::AttachEngine3D
  Height = 60
  Placement = pos=(26,-4,-6) rot=(0,0,1;0rad)
  Radius = 1.45
FEATURE [Part::Compound] Compound671
  Links = -> [Cylinder646,Cylinder647]
FEATURE [Part::Compound] Compound669
  Links = -> [Cylinder646,Cylinder647]
  Placement = pos=(0,0,0) rot=(0,0,1;2.0944rad)
FEATURE [Part::Compound] Compound672
  Links = -> [Cylinder646,Cylinder647]
  Placement = pos=(0,0,0) rot=(0,0,1;4.18879rad)
FEATURE [Part::Compound] Compound676
  Links = -> [Compound669,Compound672,Compound671]
FEATURE [Part::Cylinder] Cylinder648  label="Válec648"
  Angle = 360
  AttacherType = Attacher::AttachEngine3D
  Height = 3
  Placement = pos=(26,-4,-6) rot=(0,0,1;0rad)
  Radius = 3
FEATURE [Part::Compound] Compound670
  Links = -> [Cylinder643,Cylinder648]
  Placement = pos=(0,0,6) rot=(0,0,1;2.0944rad)
FEATURE [Part::Compound] Compound674
  Links = -> [Cylinder643,Cylinder648]
  Placement = pos=(0,0,6) rot=(0,0,1;4.18879rad)
FEATURE [Part::Compound] Compound675
  Links = -> [Cylinder643,Cylinder648]
  Placement = pos=(0,0,6) rot=(0,0,1;0rad)
FEATURE [Part::Compound] Compound668
  Links = -> [Compound670,Compound674,Compound675]
FEATURE [Part::Cut] Cut297
  Base = -> Cut296
  Tool = -> Compound668
FEATURE [Part::Cut] Cut293
  Base = -> Cut297
  Tool = -> Compound676
FEATURE [Part::Compound] Compound679  label="J-midi_pikovina001"
  Links = -> [Compound678,Cut293,Compound680]
FEATURE [Part::Compound] Compound681  label="J-midi_pikovina_fixo1"
  Links = -> [Tube,Tube049,Compound679]
FEATURE [Part::Chamfer] Chamfer019  label="J-midi-deep_pikovina_fixo_too-wide"
  Base = -> Compound681
  Edges = 1 edges r=1: [Edge3]
  Placement = pos=(0,0,100) rot=(0,0,1;0rad)
FEATURE [Part::Cylinder] Cylinder654  label="Válec654"
  Angle = 360
  AttacherType = Attacher::AttachEngine3D
  Height = 60
  Placement = pos=(-41,-1.1e-14,-54) rot=(0,0,1;3.14159rad)
  Radius = 1.5
FEATURE [Part::Cylinder] Cylinder655  label="Válec655"
  Angle = 360
  AttacherType = Attacher::AttachEngine3D
  Height = 60
  Placement = pos=(28.9914,-28.9914,-54) rot=(0,0,-1;0.785398rad)
  Radius = 1.5
FEATURE [Part::Cylinder] Cylinder656  label="Válec656"
  Angle = 360
  AttacherType = Attacher::AttachEngine3D
  Height = 60
  Placement = pos=(28.9914,28.9914,-54) rot=(0,0,1;0.785398rad)
  Radius = 1.5
FEATURE [Part::Cylinder] Cylinder657  label="Válec657"
  Angle = 360
  AttacherType = Attacher::AttachEngine3D
  Height = 60
  Placement = pos=(-4e-15,41,-54) rot=(0,0,1;1.5708rad)
  Radius = 1.5
FEATURE [Part::Cylinder] Cylinder658  label="Válec658"
  Angle = 360
  AttacherType = Attacher::AttachEngine3D
  Height = 60
  Placement = pos=(1.2e-14,-41,-54) rot=(0,0,-1;1.5708rad)
  Radius = 1.5
FEATURE [Part::Cylinder] Cylinder659  label="Válec659"
  Angle = 360
  AttacherType = Attacher::AttachEngine3D
  Height = 60
  Placement = pos=(-28.9914,28.9914,-54) rot=(0,0,1;2.35619rad)
  Radius = 1.5
FEATURE [Part::Cylinder] Cylinder660  label="Válec660"
  Angle = 360
  AttacherType = Attacher::AttachEngine3D
  Height = 60
  Placement = pos=(-28.9914,-28.9914,-54) rot=(0,0,1;3.92699rad)
  Radius = 1.5
FEATURE [Part::Cylinder] Cylinder661  label="Válec661"
  Angle = 360
  AttacherType = Attacher::AttachEngine3D
  Height = 60
  Placement = pos=(41,0,-54) rot=(0,0,1;0rad)
  Radius = 1.5
FEATURE [Part::Box] Box302  label="Krychle302"
  AttacherType = Attacher::AttachEngine3D
  Height = 7
  Length = 1.4
  Placement = pos=(0,0,-22) rot=(0,0,1;0.047124rad)
  Width = 60
FEATURE [Part::Box] Box303  label="Krychle303"
  AttacherType = Attacher::AttachEngine3D
  Height = 7
  Length = 1.4
  Placement = pos=(0,0,-22) rot=(0,0,-1;0.034907rad)
  Width = 60
FEATURE [Part::Cylinder] Cylinder689  label="Válec689"
  Angle = 360
  AttacherType = Attacher::AttachEngine3D
  Height = 7
  Placement = pos=(0,0,-22) rot=(0,0,1;0rad)
  Radius = 39
FEATURE [Part::Box] Box304  label="Krychle304"
  AttacherType = Attacher::AttachEngine3D
  Height = 7
  Length = 60
  Placement = pos=(-56.3816,-20.5212,-22) rot=(0,0,1;0.349066rad)
  Width = 60
FEATURE [Part::Box] Box305  label="Krychle305"
  AttacherType = Attacher::AttachEngine3D
  Height = 7
  Length = 60
  Placement = pos=(0,0,-22) rot=(0,0,-1;0.349066rad)
  Width = 60
FEATURE [Part::Box] Box306  label="Krychle306"
  AttacherType = Attacher::AttachEngine3D
  Height = 7
  Length = 120
  Placement = pos=(-60,-60,-22) rot=(0,0,-1;0rad)
  Width = 60
FEATURE [Part::FeaturePython] Tube054  # WARN: FeaturePython — macro-defined, semantics opaque (R4)
  AttacherType = Attacher::AttachEngine3D
  Height = 10
  InnerRadius = 38
  OuterRadius = 44
  Placement = pos=(0,0,-8) rot=(0,0,1;0rad)
FEATURE [Part::FeaturePython] Tube056  # WARN: FeaturePython — macro-defined, semantics opaque (R4)
  AttacherType = Attacher::AttachEngine3D
  Height = 3
  InnerRadius = 44
  OuterRadius = 46
  Placement = pos=(0,0,-1) rot=(0,0,1;0rad)
FEATURE [Part::FeaturePython] Tube071  # WARN: FeaturePython — macro-defined, semantics opaque (R4)
  AttacherType = Attacher::AttachEngine3D
  Height = 7
  InnerRadius = 39.5
  OuterRadius = 40.9
  Placement = pos=(0,0,-22) rot=(0,0,1;0rad)
FEATURE [Part::FeaturePython] Tube074  # WARN: FeaturePython — macro-defined, semantics opaque (R4)
  AttacherType = Attacher::AttachEngine3D
  Height = 7
  InnerRadius = 39.5
  OuterRadius = 40.9
  Placement = pos=(0,0,-22) rot=(0,0,1;0rad)
FEATURE [Part::Compound] Compound682
  Links = -> [Cylinder656,Cylinder657,Cylinder659,Cylinder654,Cylinder660,Cylinder658,Cylinder655,Cylinder661]
  Placement = pos=(0,0,0) rot=(0,0,1;0.392699rad)
FEATURE [Part::Cut] Cut299  label="J-midi_motor-high-washer1"
  Base = -> Tube054
  Tool = -> Compound682
FEATURE [Part::Compound] Compound691
  Links = -> [Box303,Box302]
FEATURE [Part::Cut] Cut310
  Base = -> Compound691
  Placement = pos=(0,0,14) rot=(0,0,1;0rad)
  Tool = -> Cylinder689
FEATURE [Part::Compound] Compound690
  Links = -> [Box305,Box304]
FEATURE [Part::Cut] Cut308
  Base = -> Tube071
  Tool = -> Box306
FEATURE [Part::Cut] Cut309
  Base = -> Cut308
  Placement = pos=(0,0,-7) rot=(0,0,1;0rad)
  Tool = -> Compound690
FEATURE [Part::Box] Box307  label="Krychle307"
  AttacherType = Attacher::AttachEngine3D
  Height = 7
  Length = 60
  Placement = pos=(0,0,-22) rot=(0,0,-1;0.034907rad)
  Width = 60
FEATURE [Part::Box] Box308  label="Krychle308"
  AttacherType = Attacher::AttachEngine3D
  Height = 7
  Length = 120
  Placement = pos=(-60,-60,-22) rot=(0,0,-1;0rad)
  Width = 60
FEATURE [Part::Cut] Cut312
  Base = -> Tube074
  Tool = -> Box308
FEATURE [Part::Box] Box309  label="Krychle309"
  AttacherType = Attacher::AttachEngine3D
  Height = 7
  Length = 60
  Placement = pos=(-59.9909,-1.04714,-22) rot=(0,0,1;0.017453rad)
  Width = 60
FEATURE [Part::Compound] Compound694
  Links = -> [Box307,Box309]
FEATURE [Part::Cut] Cut313
  Base = -> Cut312
  Placement = pos=(0,0,-7) rot=(0,0,1;0rad)
  Tool = -> Compound694
FEATURE [Part::Cut] Cut314
  Base = -> Cut309
  Placement = pos=(0,0,21) rot=(0,0,1;0rad)
  Tool = -> Cut313
FEATURE [Part::Compound] Compound683  label="J-midi_motor-high-washer_A2"
  Links = -> [Cut299,Tube056,Cut314]
FEATURE [Part::Chamfer] Chamfer021
  Base = -> Compound683
  Edges = 1 edges r=1: [Edge33]
FEATURE [Part::Cut] Cut315
  Base = -> Chamfer021
  Tool = -> Cut314
FEATURE [Part::Cut] Cut316  label="J-midi_encoder-belt-ring_A-part"
  Base = -> Cut315
  Tool = -> Cut310
FEATURE [Part::Box] Box310  label="Krychle310"
  AttacherType = Attacher::AttachEngine3D
  Height = 7
  Length = 1.4
  Placement = pos=(0,0,-22) rot=(0,0,1;0.34383rad)
  Width = 60
FEATURE [Part::Box] Box311  label="Krychle311"
  AttacherType = Attacher::AttachEngine3D
  Height = 7
  Length = 1.4
  Placement = pos=(0,0,-22) rot=(0,0,-1;0.314159rad)
  Width = 60
FEATURE [Part::Cylinder] Cylinder690  label="Válec690"
  Angle = 360
  AttacherType = Attacher::AttachEngine3D
  Height = 7
  Placement = pos=(0,0,-22) rot=(0,0,1;0rad)
  Radius = 39
FEATURE [Part::Cylinder] Cylinder691  label="Válec691"
  Angle = 360
  AttacherType = Attacher::AttachEngine3D
  Height = 7
  Placement = pos=(0,0,-8) rot=(0,0,1;0rad)
  Radius = 43
FEATURE [Part::Compound] Compound695
  Links = -> [Box311,Box310]
FEATURE [Part::Cut] Cut317
  Base = -> Compound695
  Placement = pos=(0,0,14) rot=(0,0,1;0rad)
  Tool = -> Cylinder690
FEATURE [Part::Common] Common
  Base = -> Cut317
  Tool = -> Cylinder691
FEATURE [Part::Cut] Cut  label="J-midi_encoder-belt-ring-A"
  Base = -> Cut316
  Placement = pos=(0,0,-11) rot=(0,0,1;0rad)
  Tool = -> Common
FEATURE [Part::Cylinder] Cylinder662  label="Válec662"
  Angle = 360
  AttacherType = Attacher::AttachEngine3D
  Height = 60
  Placement = pos=(-41,-1.1e-14,-54) rot=(0,0,1;3.14159rad)
  Radius = 1.5
FEATURE [Part::Cylinder] Cylinder663  label="Válec663"
  Angle = 360
  AttacherType = Attacher::AttachEngine3D
  Height = 60
  Placement = pos=(28.9914,28.9914,-54) rot=(0,0,1;0.785398rad)
  Radius = 1.5
FEATURE [Part::Cylinder] Cylinder664  label="Válec664"
  Angle = 360
  AttacherType = Attacher::AttachEngine3D
  Height = 60
  Placement = pos=(28.9914,-28.9914,-54) rot=(0,0,-1;0.785398rad)
  Radius = 1.5
FEATURE [Part::FeaturePython] Tube057  # WARN: FeaturePython — macro-defined, semantics opaque (R4)
  AttacherType = Attacher::AttachEngine3D
  Height = 3
  InnerRadius = 38
  OuterRadius = 44
  Placement = pos=(0,0,-13) rot=(0,0,1;0rad)
FEATURE [Part::FeaturePython] Tube058  # WARN: FeaturePython — macro-defined, semantics opaque (R4)
  AttacherType = Attacher::AttachEngine3D
  Height = 3
  InnerRadius = 44
  OuterRadius = 46
  Placement = pos=(0,0,-13) rot=(0,0,1;0rad)
FEATURE [Part::Cylinder] Cylinder665  label="Válec665"
  Angle = 360
  AttacherType = Attacher::AttachEngine3D
  Height = 60
  Placement = pos=(-28.9914,-28.9914,-54) rot=(0,0,1;3.92699rad)
  Radius = 1.5
FEATURE [Part::Cylinder] Cylinder666  label="Válec666"
  Angle = 360
  AttacherType = Attacher::AttachEngine3D
  Height = 60
  Placement = pos=(41,0,-54) rot=(0,0,1;0rad)
  Radius = 1.5
FEATURE [Part::Cylinder] Cylinder667  label="Válec667"
  Angle = 360
  AttacherType = Attacher::AttachEngine3D
  Height = 60
  Placement = pos=(1.2e-14,-41,-54) rot=(0,0,-1;1.5708rad)
  Radius = 1.5
FEATURE [Part::Cylinder] Cylinder668  label="Válec668"
  Angle = 360
  AttacherType = Attacher::AttachEngine3D
  Height = 60
  Placement = pos=(-4e-15,41,-54) rot=(0,0,1;1.5708rad)
  Radius = 1.5
FEATURE [Part::Cylinder] Cylinder669  label="Válec669"
  Angle = 360
  AttacherType = Attacher::AttachEngine3D
  Height = 60
  Placement = pos=(-28.9914,28.9914,-54) rot=(0,0,1;2.35619rad)
  Radius = 1.5
FEATURE [Part::Compound] Compound685
  Links = -> [Cylinder663,Cylinder668,Cylinder669,Cylinder662,Cylinder665,Cylinder667,Cylinder664,Cylinder666]
  Placement = pos=(0,0,0) rot=(0,0,1;0.392699rad)
FEATURE [Part::Cut] Cut300  label="J-midi_motor-high-washer003"
  Base = -> Tube057
  Tool = -> Compound685
FEATURE [Part::Compound] Compound684  label="J-midi_motor-high-washer_B1"
  Links = -> [Cut300,Tube058]
FEATURE [Part::Chamfer] Chamfer023  label="J-midi_encoder-belt-ring_B"
  Base = -> Compound684
  Edges = 1 edges r=1: [Edge31]
  Placement = pos=(0,0,-9) rot=(0,0,1;0rad)
FEATURE [Part::FeaturePython] wormgear038  # WARN: FeaturePython — macro-defined, semantics opaque (R4)
  AttacherType = Attacher::AttachEngine3D
  Placement = pos=(0,0,0) rot=(0,0,1;0.296706rad)
  beta = 39.0939
  clearance = 0.2
  diameter = 24
  head = 0.25
  height = 12
  module = 1.5
  pressure_angle = 25
  reverse_pitch = false
  teeth = 13
  version = 0.0.3
FEATURE [Part::Cylinder] Cylinder694  label="Válec694"
  Angle = 360
  AttacherType = Attacher::AttachEngine3D
  Height = 80
  Placement = pos=(0,0,-10) rot=(0,0,1;0rad)
  Radius = 2.75
FEATURE [Part::FeaturePython] wormgear042  # WARN: FeaturePython — macro-defined, semantics opaque (R4)
  AttacherType = Attacher::AttachEngine3D
  Placement = pos=(0,0,12) rot=(0,0,1;0.560251rad)
  beta = 39.0939
  clearance = 0.2
  diameter = 24
  head = 0.25
  height = 12
  module = 1.5
  pressure_angle = 25
  reverse_pitch = true
  teeth = 13
  version = 0.0.3
FEATURE [Part::FeaturePython] wormgear039  # WARN: FeaturePython — macro-defined, semantics opaque (R4)
  AttacherType = Attacher::AttachEngine3D
  Placement = pos=(0,0,37) rot=(0,0,1;0.139626rad)
  beta = 39.5226
  clearance = 0.25
  diameter = 20
  head = 0.25
  height = 12
  module = 1.5
  pressure_angle = 20
  reverse_pitch = true
  teeth = 11
  version = 0.0.3
FEATURE [Part::FeaturePython] wormgear043  # WARN: FeaturePython — macro-defined, semantics opaque (R4)
  AttacherType = Attacher::AttachEngine3D
  Placement = pos=(0,0,24) rot=(0,0,1;0.279253rad)
  beta = 39.5226
  clearance = 0.25
  diameter = 20
  head = 0.25
  height = 13
  module = 1.5
  pressure_angle = 20
  reverse_pitch = false
  teeth = 11
  version = 0.0.3
FEATURE [Part::Compound] Compound729
  Links = -> [wormgear038,wormgear039,wormgear042,wormgear043]
FEATURE [Part::Cut] Cut351  label="J-midi-deep_outer-planeo"
  Base = -> Compound729
  Placement = pos=(22,0,0) rot=(0,0,1;0.226893rad)
  Tool = -> Cylinder694
FEATURE [Mesh::Feature] Mesh004  label="J-midi-deep_outer-planeo (Meshed)"
FEATURE [Part::Torus] Torus006  label="Anuloid006"
  Angle1 = -180
  Angle2 = 180
  Angle3 = 360
  AttacherType = Attacher::AttachEngine3D
  Placement = pos=(0,0,34) rot=(0,0,1;0rad)
  Radius1 = 46
  Radius2 = 3.1
FEATURE [Part::Box] Box370  label="Krychle370"
  AttacherType = Attacher::AttachEngine3D
  Height = 2
  Length = 6
  Placement = pos=(30.4056,-34.6482,33) rot=(0,0,1;0.785398rad)
  Width = 8
FEATURE [Part::Cylinder] Cylinder695  label="Válec695"
  Angle = 360
  AttacherType = Attacher::AttachEngine3D
  Height = 20
  Placement = pos=(-46.4,0,34) rot=(0,0,1;0rad)
  Radius = 3.5
FEATURE [Part::Box] Box371  label="Krychle371"
  AttacherType = Attacher::AttachEngine3D
  Height = 2
  Length = 6
  Placement = pos=(3,46,33) rot=(0,0,1;3.14159rad)
  Width = 8
FEATURE [Part::Box] Box312  label="Krychle312"
  AttacherType = Attacher::AttachEngine3D
  Height = 2
  Length = 6
  Placement = pos=(-3,-46,33) rot=(0,0,1;0rad)
  Width = 8
FEATURE [Part::Cylinder] Cylinder696  label="Válec696"
  Angle = 360
  AttacherType = Attacher::AttachEngine3D
  Height = 12
  Radius = 40
FEATURE [Part::Cylinder] Cylinder697  label="Válec697"
  Angle = 360
  AttacherType = Attacher::AttachEngine3D
  Height = 12
  Radius = 40
FEATURE [Part::Box] Box313  label="Krychle313"
  AttacherType = Attacher::AttachEngine3D
  Height = 2
  Length = 6
  Placement = pos=(-46,3,33) rot=(0,0,-1;1.5708rad)
  Width = 8
FEATURE [Part::Box] Box314  label="Krychle314"
  AttacherType = Attacher::AttachEngine3D
  Height = 2
  Length = 6
  Placement = pos=(-3,-46,33) rot=(0,0,1;0rad)
  Width = 8
FEATURE [Part::Box] Box315  label="Krychle315"
  AttacherType = Attacher::AttachEngine3D
  Height = 2
  Length = 6
  Placement = pos=(-46,3,33) rot=(0,0,-1;1.5708rad)
  Width = 8
FEATURE [Part::Box] Box316  label="Krychle316"
  AttacherType = Attacher::AttachEngine3D
  Height = 2
  Length = 6
  Placement = pos=(-34.6482,-30.4056,33) rot=(0,0,-1;0.785398rad)
  Width = 8
FEATURE [Part::Box] Box317  label="Krychle317"
  AttacherType = Attacher::AttachEngine3D
  Height = 2
  Length = 6
  Placement = pos=(46,-3,33) rot=(0,0,1;1.5708rad)
  Width = 8
FEATURE [Part::Box] Box318  label="Krychle318"
  AttacherType = Attacher::AttachEngine3D
  Height = 2
  Length = 6
  Placement = pos=(34.6482,30.4056,33) rot=(0,0,1;2.35619rad)
  Width = 8
FEATURE [Part::Box] Box319  label="Krychle319"
  AttacherType = Attacher::AttachEngine3D
  Height = 2
  Length = 6
  Placement = pos=(30.4056,-34.6482,33) rot=(0,0,1;0.785398rad)
  Width = 8
FEATURE [Part::Box] Box320  label="Krychle320"
  AttacherType = Attacher::AttachEngine3D
  Height = 2
  Length = 6
  Placement = pos=(-30.4056,34.6482,33) rot=(0,0,1;3.92699rad)
  Width = 8
FEATURE [Part::Compound] Compound697
  Links = -> [Box316,Box370,Box317,Box314,Box318,Box371,Box320,Box313]
  Placement = pos=(0,0,7) rot=(0,0,1;0.392699rad)
FEATURE [Part::Box] Box321  label="Krychle321"
  AttacherType = Attacher::AttachEngine3D
  Height = 2
  Length = 6
  Placement = pos=(46,-3,33) rot=(0,0,1;1.5708rad)
  Width = 8
FEATURE [Part::Box] Box322  label="Krychle322"
  AttacherType = Attacher::AttachEngine3D
  Height = 2
  Length = 6
  Placement = pos=(3,46,33) rot=(0,0,1;3.14159rad)
  Width = 8
FEATURE [Part::Cylinder] Cylinder698  label="Válec698"
  Angle = 360
  AttacherType = Attacher::AttachEngine3D
  Height = 20
  Placement = pos=(-46.4,0,34) rot=(0,0,1;0rad)
  Radius = 3.5
FEATURE [Part::Cylinder] Cylinder699  label="Válec699"
  Angle = 360
  AttacherType = Attacher::AttachEngine3D
  Height = 32
  Placement = pos=(-29.6985,-29.6985,33.5) rot=(0,0,-1;0.785398rad)
  Radius = 1.5
FEATURE [Part::Cylinder] Cylinder700  label="Válec700"
  Angle = 360
  AttacherType = Attacher::AttachEngine3D
  Height = 12
  Placement = pos=(-29.6985,-29.6985,33.5) rot=(0,0,-1;0.785398rad)
  Radius = 1.5
FEATURE [Part::Cylinder] Cylinder701  label="Válec701"
  Angle = 360
  AttacherType = Attacher::AttachEngine3D
  Height = 12
  Placement = pos=(29.6985,-29.6985,33.5) rot=(0,0,1;0.785398rad)
  Radius = 1.5
FEATURE [Part::Box] Box323  label="Krychle323"
  AttacherType = Attacher::AttachEngine3D
  Height = 2
  Length = 6
  Placement = pos=(-34.6482,-30.4056,33) rot=(0,0,-1;0.785398rad)
  Width = 8
FEATURE [Part::Cylinder] Cylinder702  label="Válec702"
  Angle = 360
  AttacherType = Attacher::AttachEngine3D
  Height = 32
  Placement = pos=(0,-42,33.5) rot=(0,0,1;0rad)
  Radius = 1.5
FEATURE [Part::Cylinder] Cylinder703  label="Válec703"
  Angle = 360
  AttacherType = Attacher::AttachEngine3D
  Height = 12
  Placement = pos=(0,-42,33.5) rot=(0,0,1;0rad)
  Radius = 1.5
FEATURE [Part::Cylinder] Cylinder704  label="Válec704"
  Angle = 360
  AttacherType = Attacher::AttachEngine3D
  Height = 32
  Placement = pos=(-1.4e-14,42,33.5) rot=(0,0,1;3.14159rad)
  Radius = 1.5
FEATURE [Part::FeaturePython] wormgear044  # WARN: FeaturePython — macro-defined, semantics opaque (R4)
  AttacherType = Attacher::AttachEngine3D
  Placement = pos=(0,0,0) rot=(0,0,-1;0.1309rad)
  beta = 39.2894
  clearance = 0.25
  diameter = 66
  head = 0
  height = 14
  module = 1.5
  pressure_angle = 20
  reverse_pitch = false
  teeth = 36
  version = 0.0.3
FEATURE [Part::Cut] Cut324
  Base = -> Cylinder697
  Placement = pos=(0,0,21) rot=(0,0,1;0.258309rad)
  Tool = -> wormgear044
FEATURE [Part::FeaturePython] Tube075  # WARN: FeaturePython — macro-defined, semantics opaque (R4)
  AttacherType = Attacher::AttachEngine3D
  Height = 24
  InnerRadius = 40
  OuterRadius = 46
  Placement = pos=(0,0,21) rot=(0,0,1;0rad)
FEATURE [Part::Cut] Cut325
  Base = -> Tube075
  Tool = -> Torus006
FEATURE [Part::Cut] Cut326
  Base = -> Cut325
  Tool = -> Cylinder695
FEATURE [Part::FeaturePython] wormgear045  # WARN: FeaturePython — macro-defined, semantics opaque (R4)
  AttacherType = Attacher::AttachEngine3D
  Placement = pos=(0,0,0) rot=(0,0,1;0.10472rad)
  beta = 39.2894
  clearance = 0.25
  diameter = 66
  head = 0
  height = 14
  module = 1.5
  pressure_angle = 20
  reverse_pitch = true
  teeth = 36
  version = 0.0.3
FEATURE [Part::Cut] Cut322
  Base = -> Cylinder696
  Placement = pos=(0,0,33) rot=(0,0,1;0.466876rad)
  Tool = -> wormgear045
FEATURE [Part::Cut] Cut327
  Base = -> Cut322
  Tool = -> Compound697
FEATURE [Part::Compound] Compound699
  Links = -> [Cut327,Cut324]
FEATURE [Part::FeaturePython] Tube076  # WARN: FeaturePython — macro-defined, semantics opaque (R4)
  AttacherType = Attacher::AttachEngine3D
  Height = 1
  InnerRadius = 36
  OuterRadius = 46
  Placement = pos=(0,0,45) rot=(0,0,1;0rad)
FEATURE [Part::Cut] Cut323
  Base = -> Tube076
  Tool = -> Cylinder698
FEATURE [Part::Cylinder] Cylinder705  label="Válec705"
  Angle = 360
  AttacherType = Attacher::AttachEngine3D
  Height = 12
  Placement = pos=(-42,-2.4e-14,33.5) rot=(0,0,-1;1.5708rad)
  Radius = 1.5
FEATURE [Part::Cylinder] Cylinder706  label="Válec706"
  Angle = 360
  AttacherType = Attacher::AttachEngine3D
  Height = 12
  Placement = pos=(-1.4e-14,42,33.5) rot=(0,0,1;3.14159rad)
  Radius = 1.5
FEATURE [Part::Box] Box324  label="Krychle324"
  AttacherType = Attacher::AttachEngine3D
  Height = 2
  Length = 6
  Placement = pos=(34.6482,30.4056,33) rot=(0,0,1;2.35619rad)
  Width = 8
FEATURE [Part::Cylinder] Cylinder707  label="Válec707"
  Angle = 360
  AttacherType = Attacher::AttachEngine3D
  Height = 12
  Placement = pos=(29.6985,29.6985,33.5) rot=(0,0,1;2.35619rad)
  Radius = 1.5
FEATURE [Part::Box] Box325  label="Krychle325"
  AttacherType = Attacher::AttachEngine3D
  Height = 2
  Length = 6
  Placement = pos=(-34.6482,-30.4056,33) rot=(0,0,-1;0.785398rad)
  Width = 8
FEATURE [Part::Box] Box326  label="Krychle326"
  AttacherType = Attacher::AttachEngine3D
  Height = 2
  Length = 6
  Placement = pos=(-30.4056,34.6482,33) rot=(0,0,1;3.92699rad)
  Width = 8
FEATURE [Part::Compound] Compound700
  Links = -> [Box325,Box319,Box321,Box312,Box324,Box322,Box326,Box315]
  Placement = pos=(0,0,7) rot=(0,0,1;0.392699rad)
FEATURE [Part::Cylinder] Cylinder708  label="Válec708"
  Angle = 360
  AttacherType = Attacher::AttachEngine3D
  Height = 12
  Placement = pos=(-29.6985,29.6985,33.5) rot=(0,0,1;3.92699rad)
  Radius = 1.5
FEATURE [Part::Cylinder] Cylinder709  label="Válec709"
  Angle = 360
  AttacherType = Attacher::AttachEngine3D
  Height = 12
  Placement = pos=(42,6e-15,33.5) rot=(0,0,1;1.5708rad)
  Radius = 1.5
FEATURE [Part::Compound] Compound701
  Links = -> [Cylinder703,Cylinder701,Cylinder709,Cylinder707,Cylinder706,Cylinder708,Cylinder705,Cylinder700]
  Placement = pos=(0,0,4) rot=(0,0,1;0.392699rad)
FEATURE [Part::Cut] Cut330
  Base = -> Cut323
  Tool = -> Compound701
FEATURE [Part::Cut] Cut321
  Base = -> Cut330
  Tool = -> Compound700
FEATURE [Part::Box] Box327  label="Krychle327"
  AttacherType = Attacher::AttachEngine3D
  Height = 2
  Length = 6
  Placement = pos=(-30.4056,34.6482,33) rot=(0,0,1;3.92699rad)
  Width = 8
FEATURE [Part::Box] Box328  label="Krychle328"
  AttacherType = Attacher::AttachEngine3D
  Height = 2
  Length = 6
  Placement = pos=(-3,-46,33) rot=(0,0,1;0rad)
  Width = 8
FEATURE [Part::Box] Box329  label="Krychle329"
  AttacherType = Attacher::AttachEngine3D
  Height = 2
  Length = 6
  Placement = pos=(46,-3,33) rot=(0,0,1;1.5708rad)
  Width = 8
FEATURE [Part::Cylinder] Cylinder710  label="Válec710"
  Angle = 360
  AttacherType = Attacher::AttachEngine3D
  Height = 32
  Placement = pos=(-29.6985,29.6985,33.5) rot=(0,0,1;3.92699rad)
  Radius = 1.5
FEATURE [Part::Box] Box330  label="Krychle330"
  AttacherType = Attacher::AttachEngine3D
  Height = 2
  Length = 6
  Placement = pos=(-46,3,33) rot=(0,0,-1;1.5708rad)
  Width = 8
FEATURE [Part::Box] Box331  label="Krychle331"
  AttacherType = Attacher::AttachEngine3D
  Height = 2
  Length = 6
  Placement = pos=(30.4056,-34.6482,33) rot=(0,0,1;0.785398rad)
  Width = 8
FEATURE [Part::Cylinder] Cylinder711  label="Válec711"
  Angle = 360
  AttacherType = Attacher::AttachEngine3D
  Height = 32
  Placement = pos=(-42,-2.4e-14,33.5) rot=(0,0,-1;1.5708rad)
  Radius = 1.5
FEATURE [Part::Box] Box332  label="Krychle332"
  AttacherType = Attacher::AttachEngine3D
  Height = 2
  Length = 6
  Placement = pos=(3,46,33) rot=(0,0,1;3.14159rad)
  Width = 8
FEATURE [Part::Cylinder] Cylinder712  label="Válec712"
  Angle = 360
  AttacherType = Attacher::AttachEngine3D
  Height = 32
  Placement = pos=(29.6985,29.6985,33.5) rot=(0,0,1;2.35619rad)
  Radius = 1.5
FEATURE [Part::Box] Box333  label="Krychle333"
  AttacherType = Attacher::AttachEngine3D
  Height = 2
  Length = 6
  Placement = pos=(34.6482,30.4056,33) rot=(0,0,1;2.35619rad)
  Width = 8
FEATURE [Part::Compound] Compound696
  Links = -> [Box323,Box331,Box329,Box328,Box333,Box332,Box327,Box330]
  Placement = pos=(0,0,7) rot=(0,0,1;0.392699rad)
FEATURE [Part::Cylinder] Cylinder713  label="Válec713"
  Angle = 360
  AttacherType = Attacher::AttachEngine3D
  Height = 32
  Placement = pos=(42,6e-15,33.5) rot=(0,0,1;1.5708rad)
  Radius = 1.5
FEATURE [Part::Cylinder] Cylinder776  label="Válec776"
  Angle = 360
  AttacherType = Attacher::AttachEngine3D
  Height = 32
  Placement = pos=(29.6985,-29.6985,33.5) rot=(0,0,1;0.785398rad)
  Radius = 1.5
FEATURE [Part::Compound] Compound698
  Links = -> [Cylinder702,Cylinder776,Cylinder713,Cylinder712,Cylinder704,Cylinder710,Cylinder711,Cylinder699]
  Placement = pos=(0,0,4) rot=(0,0,1;0.392699rad)
FEATURE [Part::Cut] Cut328
  Base = -> Cut326
  Tool = -> Compound698
FEATURE [Part::Cut] Cut329
  Base = -> Cut328
  Tool = -> Compound696
FEATURE [Part::Compound] Compound702  label="J-midi_actuator-ring-m1.5_v1"
  Links = -> [Cut329,Cut321,Compound699]
  Placement = pos=(0,0,4) rot=(0,0,1;0rad)
FEATURE [Part::Cylinder] Cylinder1031  label="Válec1031"
  Angle = 360
  AttacherType = Attacher::AttachEngine3D
  Height = 20
  Placement = pos=(-4.25,-4.25,-88) rot=(0,0,1;0rad)
  Radius = 1
FEATURE [Part::Cylinder] Cylinder1032  label="Válec1032"
  Angle = 360
  AttacherType = Attacher::AttachEngine3D
  Height = 20
  Placement = pos=(4.25,4.25,-88) rot=(0,0,1;3.14159rad)
  Radius = 1
FEATURE [Part::Cylinder] Cylinder1033  label="Válec1033"
  Angle = 360
  AttacherType = Attacher::AttachEngine3D
  Height = 2
  Placement = pos=(-4.25,4.25,-88) rot=(0,0,-1;1.5708rad)
  Radius = 2
FEATURE [Part::Cylinder] Cylinder1034  label="Válec1034"
  Angle = 360
  AttacherType = Attacher::AttachEngine3D
  Height = 2
  Placement = pos=(4.25,4.25,-88) rot=(0,0,1;3.14159rad)
  Radius = 2
FEATURE [Part::Cylinder] Cylinder1035  label="Válec1035"
  Angle = 360
  AttacherType = Attacher::AttachEngine3D
  Height = 4
  Placement = pos=(0,0,15) rot=(0,0,1;0rad)
  Radius = 8
FEATURE [Part::Cylinder] Cylinder1036  label="Válec1036"
  Angle = 360
  AttacherType = Attacher::AttachEngine3D
  Height = 20
  Placement = pos=(4.25,-4.25,-88) rot=(0,0,1;1.5708rad)
  Radius = 1
FEATURE [Part::Cylinder] Cylinder1037  label="Válec1037"
  Angle = 360
  AttacherType = Attacher::AttachEngine3D
  Height = 20
  Placement = pos=(4.25,-4.25,-88) rot=(0,0,1;1.5708rad)
  Radius = 1
FEATURE [Part::Cylinder] Cylinder1038  label="Válec1038"
  Angle = 360
  AttacherType = Attacher::AttachEngine3D
  Height = 20
  Placement = pos=(-4.25,4.25,-88) rot=(0,0,-1;1.5708rad)
  Radius = 1
FEATURE [Part::Cylinder] Cylinder1039  label="Válec1039"
  Angle = 360
  AttacherType = Attacher::AttachEngine3D
  Height = 2
  Placement = pos=(4.25,-4.25,-88) rot=(0,0,1;1.5708rad)
  Radius = 2
FEATURE [Part::Cylinder] Cylinder1040  label="Válec1040"
  Angle = 360
  AttacherType = Attacher::AttachEngine3D
  Height = 20
  Placement = pos=(4.25,-4.25,-88) rot=(0,0,1;1.5708rad)
  Radius = 1
FEATURE [Part::Cylinder] Cylinder1041  label="Válec1041"
  Angle = 360
  AttacherType = Attacher::AttachEngine3D
  Height = 20
  Placement = pos=(4.25,4.25,-88) rot=(0,0,1;3.14159rad)
  Radius = 1
FEATURE [Part::FeaturePython] Tube086  # WARN: FeaturePython — macro-defined, semantics opaque (R4)
  AttacherType = Attacher::AttachEngine3D
  Height = 12
  InnerRadius = 4.1
  OuterRadius = 8
  Placement = pos=(0,0,12) rot=(0,0,1;0rad)
FEATURE [Part::FeaturePython] Tube087  # WARN: FeaturePython — macro-defined, semantics opaque (R4)
  AttacherType = Attacher::AttachEngine3D
  Height = 10
  InnerRadius = 2.65
  OuterRadius = 8
  Placement = pos=(0,0,19) rot=(0,0,1;0rad)
FEATURE [Part::FeaturePython] wormgear047  # WARN: FeaturePython — macro-defined, semantics opaque (R4)
  AttacherType = Attacher::AttachEngine3D
  Placement = pos=(0,0,29) rot=(0,0,1;0.994838rad)
  beta = 39.2894
  clearance = 0.25
  diameter = 22
  head = 0.25
  height = 12
  module = 1.5
  pressure_angle = 20
  reverse_pitch = false
  teeth = 12
  version = 0.0.3
FEATURE [Part::Wedge] Wedge021  label="Klín021"
  AttacherType = Attacher::AttachEngine3D
  Placement = pos=(0,0,12) rot=(0,0,1;0rad)
  X2max = 0
  X2min = 0
  Xmax = 10
  Xmin = -10
  Ymax = 0
  Ymin = -32
  Z2max = 12
  Z2min = 0
  Zmax = 12
  Zmin = 0
FEATURE [Part::Wedge] Wedge022  label="Klín022"
  AttacherType = Attacher::AttachEngine3D
  Placement = pos=(0,0,12) rot=(0,0,1;3.14159rad)
  X2max = 0
  X2min = 0
  Xmax = 10
  Xmin = -10
  Ymax = 0
  Ymin = -32
  Z2max = 12
  Z2min = 0
  Zmax = 12
  Zmin = 0
FEATURE [Part::Wedge] Wedge023  label="Klín023"
  AttacherType = Attacher::AttachEngine3D
  Placement = pos=(0,0,12) rot=(0,0,1;1.5708rad)
  X2max = 0
  X2min = 0
  Xmax = 10
  Xmin = -10
  Ymax = 0
  Ymin = -32
  Z2max = 12
  Z2min = 0
  Zmax = 12
  Zmin = 0
FEATURE [Part::Wedge] Wedge020  label="Klín020"
  AttacherType = Attacher::AttachEngine3D
  Placement = pos=(0,0,12) rot=(0,0,-1;1.5708rad)
  X2max = 0
  X2min = 0
  Xmax = 10
  Xmin = -10
  Ymax = 0
  Ymin = -32
  Z2max = 12
  Z2min = 0
  Zmax = 12
  Zmin = 0
FEATURE [Part::Cylinder] Cylinder1024  label="Válec1024"
  Angle = 360
  AttacherType = Attacher::AttachEngine3D
  Height = 20
  Placement = pos=(-4.25,4.25,-88) rot=(0,0,-1;1.5708rad)
  Radius = 1
FEATURE [Part::Cylinder] Cylinder1025  label="Válec1025"
  Angle = 360
  AttacherType = Attacher::AttachEngine3D
  Height = 20
  Placement = pos=(-4.25,-4.25,-88) rot=(0,0,1;0rad)
  Radius = 1
FEATURE [Part::Compound] Compound826
  Links = -> [Cylinder1025,Cylinder1040,Cylinder1032,Cylinder1038]
  Placement = pos=(0,0,91) rot=(0,0,1;0rad)
FEATURE [Part::Cylinder] Cylinder1026  label="Válec1026"
  Angle = 360
  AttacherType = Attacher::AttachEngine3D
  Height = 2
  Placement = pos=(-4.25,-4.25,-88) rot=(0,0,1;0rad)
  Radius = 2
FEATURE [Part::Cylinder] Cylinder1027  label="Válec1027"
  Angle = 360
  AttacherType = Attacher::AttachEngine3D
  Height = 20
  Placement = pos=(-4.25,4.25,-88) rot=(0,0,-1;1.5708rad)
  Radius = 1
FEATURE [Part::Cylinder] Cylinder1028  label="Válec1028"
  Angle = 360
  AttacherType = Attacher::AttachEngine3D
  Height = 20
  Placement = pos=(-4.25,-4.25,-88) rot=(0,0,1;0rad)
  Radius = 1
FEATURE [Part::Cylinder] Cylinder1029  label="Válec1029"
  Angle = 360
  AttacherType = Attacher::AttachEngine3D
  Height = 20
  Placement = pos=(4.25,4.25,-88) rot=(0,0,1;3.14159rad)
  Radius = 1
FEATURE [Part::Cylinder] Cylinder1030  label="Válec1030"
  Angle = 360
  AttacherType = Attacher::AttachEngine3D
  Height = 60
  Placement = pos=(0,0,-10) rot=(0,0,1;0rad)
  Radius = 2.65
FEATURE [Part::Compound] Compound827
  Links = -> [Cylinder1026,Cylinder1039,Cylinder1034,Cylinder1033]
  Placement = pos=(0,0,91) rot=(0,0,1;0rad)
FEATURE [Part::Compound] Compound829
  Links = -> [Cylinder1031,Cylinder1037,Cylinder1041,Cylinder1027]
  Placement = pos=(0,0,91) rot=(0,0,1;0rad)
FEATURE [Part::Compound] Compound830
  Links = -> [Wedge021,Wedge023,Wedge022,Wedge020]
FEATURE [Part::Compound] Compound831
  Links = -> [Cylinder1028,Cylinder1036,Cylinder1029,Cylinder1024]
  Placement = pos=(0,0,91) rot=(0,0,1;0rad)
FEATURE [Part::Cut] Cut377
  Base = -> wormgear047
  Tool = -> Cylinder1030
FEATURE [Part::Cut] Cut372
  Base = -> Tube087
  Tool = -> Compound829
FEATURE [Part::Cut] Cut373
  Base = -> Cylinder1035
  Tool = -> Compound831
FEATURE [Part::Cut] Cut376
  Base = -> Tube086
  Placement = pos=(0,0,-9) rot=(0,0,1;0rad)
  Tool = -> Compound830
FEATURE [Part::Chamfer] Chamfer026
  Base = -> Cut376
  Edges = 8 edges r=1: [Edge7,Edge8,Edge21,Edge22,Edge31,Edge32,Edge45,Edge46]
FEATURE [Part::Cut] Cut375
  Base = -> Chamfer026
  Tool = -> Compound827
FEATURE [Part::Cut] Cut374
  Base = -> Cut375
  Tool = -> Compound826
FEATURE [Part::Compound] Compound828  label="J-midi_inner-planeo-m1.5-reinforced_v1"
  Links = -> [Cut377,Cut374,Cut373,Cut372]
  Placement = pos=(0,0,8) rot=(0,0,1;0.10472rad)
FEATURE [Part::FeaturePython] wormgear048  # WARN: FeaturePython — macro-defined, semantics opaque (R4)
  AttacherType = Attacher::AttachEngine3D
  Placement = pos=(0,0,0) rot=(0,0,1;0.296706rad)
  beta = 41.1859
  clearance = 0.2
  diameter = 24
  head = 0.25
  height = 12
  module = 1.5
  pressure_angle = 25
  reverse_pitch = false
  teeth = 14
  version = 0.0.3
FEATURE [Part::FeaturePython] wormgear049  # WARN: FeaturePython — macro-defined, semantics opaque (R4)
  AttacherType = Attacher::AttachEngine3D
  Placement = pos=(0,0,24) rot=(0,0,1;0.279253rad)
  beta = 39.5226
  clearance = 0.25
  diameter = 20
  head = 0.25
  height = 13
  module = 1.5
  pressure_angle = 20
  reverse_pitch = false
  teeth = 11
  version = 0.0.3
FEATURE [Part::FeaturePython] wormgear050  # WARN: FeaturePython — macro-defined, semantics opaque (R4)
  AttacherType = Attacher::AttachEngine3D
  Placement = pos=(0,0,12) rot=(0,0,1;0.542797rad)
  beta = 41.1859
  clearance = 0.2
  diameter = 24
  head = 0.25
  height = 12
  module = 1.5
  pressure_angle = 25
  reverse_pitch = true
  teeth = 14
  version = 0.0.3
FEATURE [Part::Cylinder] Cylinder1042  label="Válec1042"
  Angle = 360
  AttacherType = Attacher::AttachEngine3D
  Height = 80
  Placement = pos=(0,0,-10) rot=(0,0,1;0rad)
  Radius = 2.8
FEATURE [Part::FeaturePython] wormgear051  # WARN: FeaturePython — macro-defined, semantics opaque (R4)
  AttacherType = Attacher::AttachEngine3D
  Placement = pos=(0,0,37) rot=(0,0,1;0.139626rad)
  beta = 39.5226
  clearance = 0.25
  diameter = 20
  head = 0.25
  height = 12
  module = 1.5
  pressure_angle = 20
  reverse_pitch = true
  teeth = 11
  version = 0.0.3
FEATURE [Part::Compound] Compound832
  Links = -> [wormgear048,wormgear051,wormgear050,wormgear049]
FEATURE [Part::Cut] Cut378  label="J-midi-deep_outer-planeo-v2"
  Base = -> Compound832
  Placement = pos=(22,0,0) rot=(0,0,1;0.226893rad)
  Tool = -> Cylinder1042
FEATURE [Mesh::Feature] Mesh005  label="J-midi-deep_outer-planeo-v2 (Meshed)"
FEATURE [Part::Cylinder] Cylinder1043  label="Válec1043"
  Angle = 360
  AttacherType = Attacher::AttachEngine3D
  Height = 80
  Placement = pos=(0,0,-10) rot=(0,0,1;0rad)
  Radius = 2.65
FEATURE [Part::FeaturePython] wormgear052  # WARN: FeaturePython — macro-defined, semantics opaque (R4)
  AttacherType = Attacher::AttachEngine3D
  Placement = pos=(0,0,0) rot=(0,0,1;0.296706rad)
  beta = 41.1859
  clearance = 0.2
  diameter = 24
  head = 0.25
  height = 12
  module = 1.5
  pressure_angle = 25
  reverse_pitch = false
  teeth = 14
  version = 0.0.3
FEATURE [Part::FeaturePython] wormgear053  # WARN: FeaturePython — macro-defined, semantics opaque (R4)
  AttacherType = Attacher::AttachEngine3D
  Placement = pos=(0,0,24) rot=(0,0,1;0.279253rad)
  beta = 39.5226
  clearance = 0.25
  diameter = 20
  head = 0.25
  height = 13
  module = 1.5
  pressure_angle = 20
  reverse_pitch = false
  teeth = 11
  version = 0.0.3
FEATURE [Part::FeaturePython] wormgear054  # WARN: FeaturePython — macro-defined, semantics opaque (R4)
  AttacherType = Attacher::AttachEngine3D
  Placement = pos=(0,0,37) rot=(0,0,1;0.139626rad)
  beta = 39.5226
  clearance = 0.25
  diameter = 20
  head = 0.25
  height = 12
  module = 1.5
  pressure_angle = 20
  reverse_pitch = true
  teeth = 11
  version = 0.0.3
FEATURE [Part::FeaturePython] wormgear055  # WARN: FeaturePython — macro-defined, semantics opaque (R4)
  AttacherType = Attacher::AttachEngine3D
  Placement = pos=(0,0,12) rot=(0,0,1;0.542797rad)
  beta = 41.1859
  clearance = 0.2
  diameter = 24
  head = 0.25
  height = 12
  module = 1.5
  pressure_angle = 25
  reverse_pitch = true
  teeth = 14
  version = 0.0.3
FEATURE [Part::Compound] Compound833
  Links = -> [wormgear052,wormgear054,wormgear055,wormgear053]
FEATURE [Part::Cut] Cut379  label="J-midi-deep_outer-planeo-v3"
  Base = -> Compound833
  Placement = pos=(22,0,0) rot=(0,0,1;0.226893rad)
  Tool = -> Cylinder1043
FEATURE [Mesh::Feature] Mesh007  label="J-midi-deep_outer-planeo-v3 (Meshed)"
FEATURE [Mesh::Feature] Mesh008  label="J-midi_quikovina_fixo (Meshed)"
FEATURE [Part::Cylinder] Cylinder1044  label="Válec1044"
  Angle = 360
  AttacherType = Attacher::AttachEngine3D
  Height = 80
  Placement = pos=(0,0,-10) rot=(0,0,1;0rad)
  Radius = 2.65
FEATURE [Part::FeaturePython] wormgear056  # WARN: FeaturePython — macro-defined, semantics opaque (R4)
  AttacherType = Attacher::AttachEngine3D
  Placement = pos=(0,0,0) rot=(0,0,1;0.296706rad)
  beta = 40.3141
  clearance = 0.2
  diameter = 24.75
  head = 0.25
  height = 12
  module = 1.5
  pressure_angle = 25
  reverse_pitch = false
  teeth = 14
  version = 0.0.3
FEATURE [Part::FeaturePython] wormgear057  # WARN: FeaturePython — macro-defined, semantics opaque (R4)
  AttacherType = Attacher::AttachEngine3D
  Placement = pos=(0,0,24) rot=(0,0,1;0.279253rad)
  beta = 39.1737
  clearance = 0.25
  diameter = 20.25
  head = 0.25
  height = 13
  module = 1.5
  pressure_angle = 20
  reverse_pitch = false
  teeth = 11
  version = 0.0.3
FEATURE [Part::FeaturePython] wormgear058  # WARN: FeaturePython — macro-defined, semantics opaque (R4)
  AttacherType = Attacher::AttachEngine3D
  Placement = pos=(0,0,12) rot=(0,0,1;0.542797rad)
  beta = 40.3141
  clearance = 0.2
  diameter = 24.75
  head = 0.25
  height = 12
  module = 1.5
  pressure_angle = 25
  reverse_pitch = true
  teeth = 14
  version = 0.0.3
FEATURE [Part::FeaturePython] wormgear059  # WARN: FeaturePython — macro-defined, semantics opaque (R4)
  AttacherType = Attacher::AttachEngine3D
  Placement = pos=(0,0,37) rot=(0,0,1;0.139626rad)
  beta = 39.1737
  clearance = 0.25
  diameter = 20.25
  head = 0.25
  height = 12
  module = 1.5
  pressure_angle = 20
  reverse_pitch = true
  teeth = 11
  version = 0.0.3
FEATURE [Part::Compound] Compound834
  Links = -> [wormgear056,wormgear059,wormgear058,wormgear057]
FEATURE [Part::Cut] Cut380  label="J-midi-deep_outer-planeo-v4"
  Base = -> Compound834
  Placement = pos=(22,0,0) rot=(0,0,1;0.226893rad)
  Tool = -> Cylinder1044
FEATURE [Mesh::Feature] Mesh009  label="J-midi-deep_outer-planeo-v4 (Meshed)"
FEATURE [Part::Box] Box372  label="Krychle372"
  AttacherType = Attacher::AttachEngine3D
  Height = 60
  Length = 50
  Placement = pos=(0,0,8) rot=(0,0,1;1.36136rad)
  Width = 50
FEATURE [Part::Cylinder] Cylinder1045  label="Válec1045"
  Angle = 360
  AttacherType = Attacher::AttachEngine3D
  Height = 3
  Placement = pos=(26,4,-6) rot=(0,0,1;0rad)
  Radius = 3
FEATURE [Part::Cylinder] Cylinder1046  label="Válec1046"
  Angle = 360
  AttacherType = Attacher::AttachEngine3D
  Height = 8
  Radius = 36
FEATURE [Part::Cylinder] Cylinder1047  label="Válec1047"
  Angle = 360
  AttacherType = Attacher::AttachEngine3D
  Height = 80
  Placement = pos=(26,-4,-6) rot=(0,0,1;0rad)
  Radius = 1.45
FEATURE [Part::Cylinder] Cylinder1048  label="Válec1048"
  Angle = 360
  AttacherType = Attacher::AttachEngine3D
  Height = 6
  Placement = pos=(11,19.0526,2) rot=(0,0,1;4.18879rad)
  Radius = 8
FEATURE [Part::Box] Box373  label="Krychle373"
  AttacherType = Attacher::AttachEngine3D
  Height = 60
  Length = 50
  Placement = pos=(0,0,8) rot=(0,0,1;2.61799rad)
  Width = 100
FEATURE [Part::Cylinder] Cylinder1049  label="Válec1049"
  Angle = 360
  AttacherType = Attacher::AttachEngine3D
  Height = 6
  Placement = pos=(11,-19.0526,2) rot=(0,0,1;2.0944rad)
  Radius = 8
FEATURE [Part::Cylinder] Cylinder1050  label="Válec1050"
  Angle = 360
  AttacherType = Attacher::AttachEngine3D
  Height = 20
  Placement = pos=(0,0,-4) rot=(0,0,1;0rad)
  Radius = 12
FEATURE [Part::Cylinder] Cylinder1051  label="Válec1051"
  Angle = 360
  AttacherType = Attacher::AttachEngine3D
  Height = 80
  Placement = pos=(26,4,-6) rot=(0,0,1;0rad)
  Radius = 1.45
FEATURE [Part::Box] Box374  label="Krychle374"
  AttacherType = Attacher::AttachEngine3D
  Height = 60
  Length = 50
  Placement = pos=(0,0,8) rot=(0,0,-1;0.837758rad)
  Width = 50
FEATURE [Part::Compound] Compound839
  Links = -> [Cylinder1051,Cylinder1047]
  Placement = pos=(0,0,0) rot=(0,0,1;1.0472rad)
FEATURE [Part::Cut] Cut381
  Base = -> Cylinder1046
  Tool = -> Cylinder1050
FEATURE [Part::FeaturePython] Tube088  # WARN: FeaturePython — macro-defined, semantics opaque (R4)
  AttacherType = Attacher::AttachEngine3D
  Height = 1
  InnerRadius = 7
  OuterRadius = 8
  Placement = pos=(-22,0,2) rot=(0,0,1;0rad)
FEATURE [Part::FeaturePython] Tube089  # WARN: FeaturePython — macro-defined, semantics opaque (R4)
  AttacherType = Attacher::AttachEngine3D
  Height = 51
  InnerRadius = 15
  OuterRadius = 30
  Placement = pos=(0,0,8) rot=(0,0,1;0rad)
FEATURE [Part::FeaturePython] Tube090  # WARN: FeaturePython — macro-defined, semantics opaque (R4)
  AttacherType = Attacher::AttachEngine3D
  Height = 1
  InnerRadius = 7
  OuterRadius = 8
  Placement = pos=(11,-19.0526,2) rot=(0,0,1;2.0944rad)
FEATURE [Part::FeaturePython] Tube091  # WARN: FeaturePython — macro-defined, semantics opaque (R4)
  AttacherType = Attacher::AttachEngine3D
  Height = 1
  InnerRadius = 12
  OuterRadius = 20
  Placement = pos=(0,0,-1) rot=(0,0,1;0rad)
FEATURE [Part::FeaturePython] Tube092  # WARN: FeaturePython — macro-defined, semantics opaque (R4)
  AttacherType = Attacher::AttachEngine3D
  Height = 1
  InnerRadius = 7
  OuterRadius = 8
  Placement = pos=(11,19.0526,2) rot=(0,0,1;4.18879rad)
FEATURE [Part::Compound] Compound847
  Links = -> [Tube090,Tube092,Tube088]
FEATURE [Part::FeaturePython] Tube093  # WARN: FeaturePython — macro-defined, semantics opaque (R4)
  AttacherType = Attacher::AttachEngine3D
  Height = 8
  InnerRadius = 12
  OuterRadius = 15
  Placement = pos=(0,0,-9) rot=(0,0,1;0rad)
FEATURE [Part::Cylinder] Cylinder1052  label="Válec1052"
  Angle = 360
  AttacherType = Attacher::AttachEngine3D
  Height = 3
  Placement = pos=(26,-4,-6) rot=(0,0,1;0rad)
  Radius = 3
FEATURE [Part::Compound] Compound840
  Links = -> [Cylinder1045,Cylinder1052]
  Placement = pos=(0,0,6) rot=(0,0,1;2.0944rad)
FEATURE [Part::Compound] Compound843
  Links = -> [Cylinder1045,Cylinder1052]
  Placement = pos=(0,0,6) rot=(0,0,1;0rad)
FEATURE [Part::Compound] Compound844
  Links = -> [Cylinder1045,Cylinder1052]
  Placement = pos=(0,0,6) rot=(0,0,1;4.18879rad)
FEATURE [Part::Compound] Compound836
  Links = -> [Compound840,Compound844,Compound843]
FEATURE [Part::Cylinder] Cylinder1053  label="Válec1053"
  Angle = 360
  AttacherType = Attacher::AttachEngine3D
  Height = 60
  Placement = pos=(26,4,-6) rot=(0,0,1;0rad)
  Radius = 1.45
FEATURE [Part::Cylinder] Cylinder1054  label="Válec1054"
  Angle = 360
  AttacherType = Attacher::AttachEngine3D
  Height = 6
  Placement = pos=(-22,0,2) rot=(0,0,1;0rad)
  Radius = 8
FEATURE [Part::Compound] Compound841
  Links = -> [Cylinder1054,Cylinder1049,Cylinder1048]
FEATURE [Part::Cut] Cut390
  Base = -> Cut381
  Tool = -> Compound841
FEATURE [Part::Cut] Cut385
  Base = -> Cut390
  Tool = -> Compound836
FEATURE [Part::Cylinder] Cylinder1055  label="Válec1055"
  Angle = 360
  AttacherType = Attacher::AttachEngine3D
  Height = 60
  Placement = pos=(26,-4,-6) rot=(0,0,1;0rad)
  Radius = 1.45
FEATURE [Part::Compound] Compound837
  Links = -> [Cylinder1053,Cylinder1055]
  Placement = pos=(0,0,0) rot=(0,0,1;4.18879rad)
FEATURE [Part::Compound] Compound842
  Links = -> [Cylinder1053,Cylinder1055]
FEATURE [Part::Compound] Compound848
  Links = -> [Cylinder1053,Cylinder1055]
  Placement = pos=(0,0,0) rot=(0,0,1;2.0944rad)
FEATURE [Part::Compound] Compound845
  Links = -> [Compound848,Compound837,Compound842]
FEATURE [Part::Cut] Cut387
  Base = -> Cut385
  Tool = -> Compound845
FEATURE [Part::Box] Box375  label="Krychle375"
  AttacherType = Attacher::AttachEngine3D
  Height = 60
  Length = 50
  Placement = pos=(0,0,8) rot=(0,0,1;4.18879rad)
  Width = 100
FEATURE [Part::Cut] Cut391
  Base = -> Tube089
  Tool = -> Box375
FEATURE [Part::Cut] Cut388
  Base = -> Cut391
  Tool = -> Box373
FEATURE [Part::Cut] Cut389
  Base = -> Cut388
  Tool = -> Box374
FEATURE [Part::Cut] Cut384
  Base = -> Cut389
  Tool = -> Box372
FEATURE [Part::Cut] Cut382
  Base = -> Cut384
  Placement = pos=(0,0,0) rot=(0,0,1;3.14159rad)
  Tool = -> Compound839
FEATURE [Part::Cut] Cut383
  Base = -> Cut384
  Placement = pos=(0,0,0) rot=(0,0,-1;1.0472rad)
  Tool = -> Compound839
FEATURE [Part::Cut] Cut386
  Base = -> Cut384
  Placement = pos=(0,0,0) rot=(0,0,1;1.0472rad)
  Tool = -> Compound839
FEATURE [Part::Compound] Compound835
  Links = -> [Cut383,Cut382,Cut386]
FEATURE [Part::Compound] Compound846  label="J-midi_pikovina002"
  Links = -> [Compound835,Cut387,Compound847]
FEATURE [Part::Compound] Compound838  label="auxi1"
  Links = -> [Tube093,Tube091,Compound846]
FEATURE [Part::Chamfer] Chamfer027  label="auxi2"
  Base = -> Compound838
  Edges = 1 edges r=1: [Edge3]
  Placement = pos=(0,0,100) rot=(0,0,1;0rad)
FEATURE [Part::Wedge] Wedge024  label="Klín024"
  AttacherType = Attacher::AttachEngine3D
  Placement = pos=(0,0,12) rot=(0,0,1;0rad)
  X2max = 0
  X2min = 0
  Xmax = 10
  Xmin = -10
  Ymax = 0
  Ymin = -32
  Z2max = 12
  Z2min = 0
  Zmax = 12
  Zmin = 0
FEATURE [Part::Wedge] Wedge025  label="Klín025"
  AttacherType = Attacher::AttachEngine3D
  Placement = pos=(0,0,12) rot=(0,0,1;3.14159rad)
  X2max = 0
  X2min = 0
  Xmax = 10
  Xmin = -10
  Ymax = 0
  Ymin = -32
  Z2max = 12
  Z2min = 0
  Zmax = 12
  Zmin = 0
FEATURE [Part::Wedge] Wedge026  label="Klín026"
  AttacherType = Attacher::AttachEngine3D
  Placement = pos=(0,0,12) rot=(0,0,1;1.5708rad)
  X2max = 0
  X2min = 0
  Xmax = 10
  Xmin = -10
  Ymax = 0
  Ymin = -32
  Z2max = 12
  Z2min = 0
  Zmax = 12
  Zmin = 0
FEATURE [Part::Wedge] Wedge027  label="Klín027"
  AttacherType = Attacher::AttachEngine3D
  Placement = pos=(0,0,12) rot=(0,0,-1;1.5708rad)
  X2max = 0
  X2min = 0
  Xmax = 10
  Xmin = -10
  Ymax = 0
  Ymin = -32
  Z2max = 12
  Z2min = 0
  Zmax = 12
  Zmin = 0
FEATURE [Part::FeaturePython] Tube094  # WARN: FeaturePython — macro-defined, semantics opaque (R4)
  AttacherType = Attacher::AttachEngine3D
  Height = 10
  InnerRadius = 2.65
  OuterRadius = 8
  Placement = pos=(0,0,19) rot=(0,0,1;0rad)
FEATURE [Part::FeaturePython] wormgear060  # WARN: FeaturePython — macro-defined, semantics opaque (R4)
  AttacherType = Attacher::AttachEngine3D
  Placement = pos=(0,0,29) rot=(0,0,1;0.994838rad)
  beta = 39.9364
  clearance = 0.25
  diameter = 21.5
  head = 0.25
  height = 12
  module = 1.5
  pressure_angle = 20
  reverse_pitch = false
  teeth = 12
  version = 0.0.3
FEATURE [Part::FeaturePython] Tube095  # WARN: FeaturePython — macro-defined, semantics opaque (R4)
  AttacherType = Attacher::AttachEngine3D
  Height = 12
  InnerRadius = 4.1
  OuterRadius = 8
  Placement = pos=(0,0,12) rot=(0,0,1;0rad)
FEATURE [Part::Cylinder] Cylinder1056  label="Válec1056"
  Angle = 360
  AttacherType = Attacher::AttachEngine3D
  Height = 20
  Placement = pos=(4.25,4.25,-88) rot=(0,0,1;3.14159rad)
  Radius = 1
FEATURE [Part::Cylinder] Cylinder1057  label="Válec1057"
  Angle = 360
  AttacherType = Attacher::AttachEngine3D
  Height = 4
  Placement = pos=(0,0,15) rot=(0,0,1;0rad)
  Radius = 8
FEATURE [Part::Cylinder] Cylinder1058  label="Válec1058"
  Angle = 360
  AttacherType = Attacher::AttachEngine3D
  Height = 20
  Placement = pos=(-4.25,4.25,-88) rot=(0,0,-1;1.5708rad)
  Radius = 1
FEATURE [Part::Cylinder] Cylinder1059  label="Válec1059"
  Angle = 360
  AttacherType = Attacher::AttachEngine3D
  Height = 20
  Placement = pos=(4.25,-4.25,-88) rot=(0,0,1;1.5708rad)
  Radius = 1
FEATURE [Part::Cylinder] Cylinder1060  label="Válec1060"
  Angle = 360
  AttacherType = Attacher::AttachEngine3D
  Height = 20
  Placement = pos=(-4.25,4.25,-88) rot=(0,0,-1;1.5708rad)
  Radius = 1
FEATURE [Part::Cylinder] Cylinder1061  label="Válec1061"
  Angle = 360
  AttacherType = Attacher::AttachEngine3D
  Height = 2
  Placement = pos=(-4.25,-4.25,-88) rot=(0,0,1;0rad)
  Radius = 2
FEATURE [Part::Cylinder] Cylinder1062  label="Válec1062"
  Angle = 360
  AttacherType = Attacher::AttachEngine3D
  Height = 20
  Placement = pos=(-4.25,-4.25,-88) rot=(0,0,1;0rad)
  Radius = 1
FEATURE [Part::Cylinder] Cylinder1063  label="Válec1063"
  Angle = 360
  AttacherType = Attacher::AttachEngine3D
  Height = 2
  Placement = pos=(-4.25,4.25,-88) rot=(0,0,-1;1.5708rad)
  Radius = 2
FEATURE [Part::Cylinder] Cylinder1064  label="Válec1064"
  Angle = 360
  AttacherType = Attacher::AttachEngine3D
  Height = 2
  Placement = pos=(4.25,4.25,-88) rot=(0,0,1;3.14159rad)
  Radius = 2
FEATURE [Part::Cylinder] Cylinder1065  label="Válec1065"
  Angle = 360
  AttacherType = Attacher::AttachEngine3D
  Height = 20
  Placement = pos=(4.25,-4.25,-88) rot=(0,0,1;1.5708rad)
  Radius = 1
FEATURE [Part::Cylinder] Cylinder1066  label="Válec1066"
  Angle = 360
  AttacherType = Attacher::AttachEngine3D
  Height = 20
  Placement = pos=(4.25,-4.25,-88) rot=(0,0,1;1.5708rad)
  Radius = 1
FEATURE [Part::Cylinder] Cylinder1067  label="Válec1067"
  Angle = 360
  AttacherType = Attacher::AttachEngine3D
  Height = 2
  Placement = pos=(4.25,-4.25,-88) rot=(0,0,1;1.5708rad)
  Radius = 2
FEATURE [Part::Cylinder] Cylinder1068  label="Válec1068"
  Angle = 360
  AttacherType = Attacher::AttachEngine3D
  Height = 20
  Placement = pos=(4.25,4.25,-88) rot=(0,0,1;3.14159rad)
  Radius = 1
FEATURE [Part::Cylinder] Cylinder1069  label="Válec1069"
  Angle = 360
  AttacherType = Attacher::AttachEngine3D
  Height = 20
  Placement = pos=(-4.25,4.25,-88) rot=(0,0,-1;1.5708rad)
  Radius = 1
FEATURE [Part::Cylinder] Cylinder1070  label="Válec1070"
  Angle = 360
  AttacherType = Attacher::AttachEngine3D
  Height = 20
  Placement = pos=(4.25,4.25,-88) rot=(0,0,1;3.14159rad)
  Radius = 1
FEATURE [Part::Cylinder] Cylinder1071  label="Válec1071"
  Angle = 360
  AttacherType = Attacher::AttachEngine3D
  Height = 20
  Placement = pos=(-4.25,-4.25,-88) rot=(0,0,1;0rad)
  Radius = 1
FEATURE [Part::Compound] Compound849
  Links = -> [Cylinder1071,Cylinder1059,Cylinder1056,Cylinder1058]
  Placement = pos=(0,0,91) rot=(0,0,1;0rad)
FEATURE [Part::Cylinder] Cylinder1072  label="Válec1072"
  Angle = 360
  AttacherType = Attacher::AttachEngine3D
  Height = 20
  Placement = pos=(-4.25,-4.25,-88) rot=(0,0,1;0rad)
  Radius = 1
FEATURE [Part::Cylinder] Cylinder1073  label="Válec1073"
  Angle = 360
  AttacherType = Attacher::AttachEngine3D
  Height = 60
  Placement = pos=(0,0,-10) rot=(0,0,1;0rad)
  Radius = 2.65
FEATURE [Part::Cut] Cut394
  Base = -> wormgear060
  Tool = -> Cylinder1073
FEATURE [Part::Compound] Compound850
  Links = -> [Cylinder1062,Cylinder1066,Cylinder1068,Cylinder1069]
  Placement = pos=(0,0,91) rot=(0,0,1;0rad)
FEATURE [Part::Cut] Cut392
  Base = -> Tube094
  Tool = -> Compound850
FEATURE [Part::Compound] Compound852
  Links = -> [Wedge024,Wedge026,Wedge025,Wedge027]
FEATURE [Part::Compound] Compound853
  Links = -> [Cylinder1061,Cylinder1067,Cylinder1064,Cylinder1063]
  Placement = pos=(0,0,91) rot=(0,0,1;0rad)
FEATURE [Part::Compound] Compound854
  Links = -> [Cylinder1072,Cylinder1065,Cylinder1070,Cylinder1060]
  Placement = pos=(0,0,91) rot=(0,0,1;0rad)
FEATURE [Part::Cut] Cut393
  Base = -> Cylinder1057
  Tool = -> Compound854
FEATURE [Part::Cut] Cut397
  Base = -> Tube095
  Placement = pos=(0,0,-9) rot=(0,0,1;0rad)
  Tool = -> Compound852
FEATURE [Part::Chamfer] Chamfer028
  Base = -> Cut397
  Edges = 8 edges r=1: [Edge7,Edge8,Edge21,Edge22,Edge31,Edge32,Edge45,Edge46]
FEATURE [Part::Cut] Cut396
  Base = -> Chamfer028
  Tool = -> Compound853
FEATURE [Part::Cut] Cut395
  Base = -> Cut396
  Tool = -> Compound849
FEATURE [Part::Compound] Compound851  label="J-midi_inner-planeo-m1.5-reinforced_v2"
  Links = -> [Cut394,Cut395,Cut393,Cut392]
  Placement = pos=(0,0,8) rot=(0,0,1;0.10472rad)
FEATURE [Part::Torus] Torus007  label="Anuloid007"
  Angle1 = -180
  Angle2 = 180
  Angle3 = 360
  AttacherType = Attacher::AttachEngine3D
  Placement = pos=(0,0,34) rot=(0,0,1;0rad)
  Radius1 = 46
  Radius2 = 3.1
FEATURE [Part::Box] Box376  label="Krychle376"
  AttacherType = Attacher::AttachEngine3D
  Height = 2
  Length = 6
  Placement = pos=(30.4056,-34.6482,33) rot=(0,0,1;0.785398rad)
  Width = 8
FEATURE [Part::Cylinder] Cylinder1074  label="Válec1074"
  Angle = 360
  AttacherType = Attacher::AttachEngine3D
  Height = 20
  Placement = pos=(-46.4,0,34) rot=(0,0,1;0rad)
  Radius = 3.5
FEATURE [Part::Box] Box377  label="Krychle377"
  AttacherType = Attacher::AttachEngine3D
  Height = 2
  Length = 6
  Placement = pos=(3,46,33) rot=(0,0,1;3.14159rad)
  Width = 8
FEATURE [Part::Box] Box378  label="Krychle378"
  AttacherType = Attacher::AttachEngine3D
  Height = 2
  Length = 6
  Placement = pos=(-3,-46,33) rot=(0,0,1;0rad)
  Width = 8
FEATURE [Part::Cylinder] Cylinder1075  label="Válec1075"
  Angle = 360
  AttacherType = Attacher::AttachEngine3D
  Height = 12
  Radius = 40
FEATURE [Part::Cylinder] Cylinder1076  label="Válec1076"
  Angle = 360
  AttacherType = Attacher::AttachEngine3D
  Height = 12
  Radius = 40
FEATURE [Part::Box] Box379  label="Krychle379"
  AttacherType = Attacher::AttachEngine3D
  Height = 2
  Length = 6
  Placement = pos=(-46,3,33) rot=(0,0,-1;1.5708rad)
  Width = 8
FEATURE [Part::Box] Box380  label="Krychle380"
  AttacherType = Attacher::AttachEngine3D
  Height = 2
  Length = 6
  Placement = pos=(-3,-46,33) rot=(0,0,1;0rad)
  Width = 8
FEATURE [Part::Box] Box381  label="Krychle381"
  AttacherType = Attacher::AttachEngine3D
  Height = 2
  Length = 6
  Placement = pos=(-46,3,33) rot=(0,0,-1;1.5708rad)
  Width = 8
FEATURE [Part::Box] Box382  label="Krychle382"
  AttacherType = Attacher::AttachEngine3D
  Height = 2
  Length = 6
  Placement = pos=(-34.6482,-30.4056,33) rot=(0,0,-1;0.785398rad)
  Width = 8
FEATURE [Part::Box] Box383  label="Krychle383"
  AttacherType = Attacher::AttachEngine3D
  Height = 2
  Length = 6
  Placement = pos=(46,-3,33) rot=(0,0,1;1.5708rad)
  Width = 8
FEATURE [Part::Box] Box384  label="Krychle384"
  AttacherType = Attacher::AttachEngine3D
  Height = 2
  Length = 6
  Placement = pos=(34.6482,30.4056,33) rot=(0,0,1;2.35619rad)
  Width = 8
FEATURE [Part::Box] Box385  label="Krychle385"
  AttacherType = Attacher::AttachEngine3D
  Height = 2
  Length = 6
  Placement = pos=(30.4056,-34.6482,33) rot=(0,0,1;0.785398rad)
  Width = 8
FEATURE [Part::Box] Box386  label="Krychle386"
  AttacherType = Attacher::AttachEngine3D
  Height = 2
  Length = 6
  Placement = pos=(-30.4056,34.6482,33) rot=(0,0,1;3.92699rad)
  Width = 8
FEATURE [Part::Compound] Compound856
  Links = -> [Box382,Box376,Box383,Box380,Box384,Box377,Box386,Box379]
  Placement = pos=(0,0,7) rot=(0,0,1;0.392699rad)
FEATURE [Part::Box] Box387  label="Krychle387"
  AttacherType = Attacher::AttachEngine3D
  Height = 2
  Length = 6
  Placement = pos=(46,-3,33) rot=(0,0,1;1.5708rad)
  Width = 8
FEATURE [Part::Box] Box388  label="Krychle388"
  AttacherType = Attacher::AttachEngine3D
  Height = 2
  Length = 6
  Placement = pos=(3,46,33) rot=(0,0,1;3.14159rad)
  Width = 8
FEATURE [Part::Cylinder] Cylinder1077  label="Válec1077"
  Angle = 360
  AttacherType = Attacher::AttachEngine3D
  Height = 20
  Placement = pos=(-46.4,0,34) rot=(0,0,1;0rad)
  Radius = 3.5
FEATURE [Part::Cylinder] Cylinder1078  label="Válec1078"
  Angle = 360
  AttacherType = Attacher::AttachEngine3D
  Height = 32
  Placement = pos=(-29.6985,-29.6985,33.5) rot=(0,0,-1;0.785398rad)
  Radius = 1.5
FEATURE [Part::Cylinder] Cylinder1079  label="Válec1079"
  Angle = 360
  AttacherType = Attacher::AttachEngine3D
  Height = 12
  Placement = pos=(-29.6985,-29.6985,33.5) rot=(0,0,-1;0.785398rad)
  Radius = 1.5
FEATURE [Part::Cylinder] Cylinder1080  label="Válec1080"
  Angle = 360
  AttacherType = Attacher::AttachEngine3D
  Height = 12
  Placement = pos=(29.6985,-29.6985,33.5) rot=(0,0,1;0.785398rad)
  Radius = 1.5
FEATURE [Part::FeaturePython] wormgear061  # WARN: FeaturePython — macro-defined, semantics opaque (R4)
  AttacherType = Attacher::AttachEngine3D
  Placement = pos=(0,0,0) rot=(0,0,-1;0.1309rad)
  beta = 39.0776
  clearance = 0.25
  diameter = 66.5
  head = 0
  height = 14
  module = 1.5
  pressure_angle = 20
  reverse_pitch = false
  teeth = 36
  version = 0.0.3
FEATURE [Part::Cut] Cut398
  Base = -> Cylinder1076
  Placement = pos=(0,0,21) rot=(0,0,1;0.258309rad)
  Tool = -> wormgear061
FEATURE [Part::FeaturePython] Tube096  # WARN: FeaturePython — macro-defined, semantics opaque (R4)
  AttacherType = Attacher::AttachEngine3D
  Height = 24
  InnerRadius = 40
  OuterRadius = 46
  Placement = pos=(0,0,21) rot=(0,0,1;0rad)
FEATURE [Part::Cut] Cut399
  Base = -> Tube096
  Tool = -> Torus007
FEATURE [Part::Cut] Cut406
  Base = -> Cut399
  Tool = -> Cylinder1074
FEATURE [Part::FeaturePython] wormgear062  # WARN: FeaturePython — macro-defined, semantics opaque (R4)
  AttacherType = Attacher::AttachEngine3D
  Placement = pos=(0,0,0) rot=(0,0,1;0.10472rad)
  beta = 39.0776
  clearance = 0.25
  diameter = 66.5
  head = 0
  height = 14
  module = 1.5
  pressure_angle = 20
  reverse_pitch = true
  teeth = 36
  version = 0.0.3
FEATURE [Part::Cut] Cut403
  Base = -> Cylinder1075
  Placement = pos=(0,0,33) rot=(0,0,1;0.466876rad)
  Tool = -> wormgear062
FEATURE [Part::Cut] Cut407
  Base = -> Cut403
  Tool = -> Compound856
FEATURE [Part::Compound] Compound858
  Links = -> [Cut407,Cut398]
FEATURE [Part::FeaturePython] Tube097  # WARN: FeaturePython — macro-defined, semantics opaque (R4)
  AttacherType = Attacher::AttachEngine3D
  Height = 1
  InnerRadius = 36
  OuterRadius = 46
  Placement = pos=(0,0,45) rot=(0,0,1;0rad)
FEATURE [Part::Cut] Cut404
  Base = -> Tube097
  Tool = -> Cylinder1077
FEATURE [Part::Box] Box389  label="Krychle389"
  AttacherType = Attacher::AttachEngine3D
  Height = 2
  Length = 6
  Placement = pos=(-34.6482,-30.4056,33) rot=(0,0,-1;0.785398rad)
  Width = 8
FEATURE [Part::Cylinder] Cylinder1081  label="Válec1081"
  Angle = 360
  AttacherType = Attacher::AttachEngine3D
  Height = 32
  Placement = pos=(0,-42,33.5) rot=(0,0,1;0rad)
  Radius = 1.5
FEATURE [Part::Cylinder] Cylinder1082  label="Válec1082"
  Angle = 360
  AttacherType = Attacher::AttachEngine3D
  Height = 12
  Placement = pos=(0,-42,33.5) rot=(0,0,1;0rad)
  Radius = 1.5
FEATURE [Part::Cylinder] Cylinder1083  label="Válec1083"
  Angle = 360
  AttacherType = Attacher::AttachEngine3D
  Height = 32
  Placement = pos=(-1.4e-14,42,33.5) rot=(0,0,1;3.14159rad)
  Radius = 1.5
FEATURE [Part::Cylinder] Cylinder1084  label="Válec1084"
  Angle = 360
  AttacherType = Attacher::AttachEngine3D
  Height = 12
  Placement = pos=(-42,-2.4e-14,33.5) rot=(0,0,-1;1.5708rad)
  Radius = 1.5
FEATURE [Part::Cylinder] Cylinder1085  label="Válec1085"
  Angle = 360
  AttacherType = Attacher::AttachEngine3D
  Height = 12
  Placement = pos=(-1.4e-14,42,33.5) rot=(0,0,1;3.14159rad)
  Radius = 1.5
FEATURE [Part::Box] Box390  label="Krychle390"
  AttacherType = Attacher::AttachEngine3D
  Height = 2
  Length = 6
  Placement = pos=(34.6482,30.4056,33) rot=(0,0,1;2.35619rad)
  Width = 8
FEATURE [Part::Cylinder] Cylinder1086  label="Válec1086"
  Angle = 360
  AttacherType = Attacher::AttachEngine3D
  Height = 12
  Placement = pos=(29.6985,29.6985,33.5) rot=(0,0,1;2.35619rad)
  Radius = 1.5
FEATURE [Part::Box] Box391  label="Krychle391"
  AttacherType = Attacher::AttachEngine3D
  Height = 2
  Length = 6
  Placement = pos=(-34.6482,-30.4056,33) rot=(0,0,-1;0.785398rad)
  Width = 8
FEATURE [Part::Box] Box392  label="Krychle392"
  AttacherType = Attacher::AttachEngine3D
  Height = 2
  Length = 6
  Placement = pos=(-30.4056,34.6482,33) rot=(0,0,1;3.92699rad)
  Width = 8
FEATURE [Part::Compound] Compound859
  Links = -> [Box391,Box385,Box387,Box378,Box390,Box388,Box392,Box381]
  Placement = pos=(0,0,7) rot=(0,0,1;0.392699rad)
FEATURE [Part::Cylinder] Cylinder1087  label="Válec1087"
  Angle = 360
  AttacherType = Attacher::AttachEngine3D
  Height = 12
  Placement = pos=(-29.6985,29.6985,33.5) rot=(0,0,1;3.92699rad)
  Radius = 1.5
FEATURE [Part::Cylinder] Cylinder1088  label="Válec1088"
  Angle = 360
  AttacherType = Attacher::AttachEngine3D
  Height = 12
  Placement = pos=(42,6e-15,33.5) rot=(0,0,1;1.5708rad)
  Radius = 1.5
FEATURE [Part::Compound] Compound860
  Links = -> [Cylinder1082,Cylinder1080,Cylinder1088,Cylinder1086,Cylinder1085,Cylinder1087,Cylinder1084,Cylinder1079]
  Placement = pos=(0,0,4) rot=(0,0,1;0.392699rad)
FEATURE [Part::Cut] Cut405
  Base = -> Cut404
  Tool = -> Compound860
FEATURE [Part::Cut] Cut402
  Base = -> Cut405
  Tool = -> Compound859
FEATURE [Part::Box] Box393  label="Krychle393"
  AttacherType = Attacher::AttachEngine3D
  Height = 2
  Length = 6
  Placement = pos=(-30.4056,34.6482,33) rot=(0,0,1;3.92699rad)
  Width = 8
FEATURE [Part::Box] Box394  label="Krychle394"
  AttacherType = Attacher::AttachEngine3D
  Height = 2
  Length = 6
  Placement = pos=(-3,-46,33) rot=(0,0,1;0rad)
  Width = 8
FEATURE [Part::Box] Box395  label="Krychle395"
  AttacherType = Attacher::AttachEngine3D
  Height = 2
  Length = 6
  Placement = pos=(46,-3,33) rot=(0,0,1;1.5708rad)
  Width = 8
FEATURE [Part::Cylinder] Cylinder1089  label="Válec1089"
  Angle = 360
  AttacherType = Attacher::AttachEngine3D
  Height = 32
  Placement = pos=(-29.6985,29.6985,33.5) rot=(0,0,1;3.92699rad)
  Radius = 1.5
FEATURE [Part::Box] Box396  label="Krychle396"
  AttacherType = Attacher::AttachEngine3D
  Height = 2
  Length = 6
  Placement = pos=(-46,3,33) rot=(0,0,-1;1.5708rad)
  Width = 8
FEATURE [Part::Box] Box397  label="Krychle397"
  AttacherType = Attacher::AttachEngine3D
  Height = 2
  Length = 6
  Placement = pos=(30.4056,-34.6482,33) rot=(0,0,1;0.785398rad)
  Width = 8
FEATURE [Part::Cylinder] Cylinder1090  label="Válec1090"
  Angle = 360
  AttacherType = Attacher::AttachEngine3D
  Height = 32
  Placement = pos=(-42,-2.4e-14,33.5) rot=(0,0,-1;1.5708rad)
  Radius = 1.5
FEATURE [Part::Box] Box398  label="Krychle398"
  AttacherType = Attacher::AttachEngine3D
  Height = 2
  Length = 6
  Placement = pos=(3,46,33) rot=(0,0,1;3.14159rad)
  Width = 8
FEATURE [Part::Cylinder] Cylinder1091  label="Válec1091"
  Angle = 360
  AttacherType = Attacher::AttachEngine3D
  Height = 32
  Placement = pos=(29.6985,29.6985,33.5) rot=(0,0,1;2.35619rad)
  Radius = 1.5
FEATURE [Part::Box] Box399  label="Krychle399"
  AttacherType = Attacher::AttachEngine3D
  Height = 2
  Length = 6
  Placement = pos=(34.6482,30.4056,33) rot=(0,0,1;2.35619rad)
  Width = 8
FEATURE [Part::Compound] Compound855
  Links = -> [Box389,Box397,Box395,Box394,Box399,Box398,Box393,Box396]
  Placement = pos=(0,0,7) rot=(0,0,1;0.392699rad)
FEATURE [Part::Cylinder] Cylinder1092  label="Válec1092"
  Angle = 360
  AttacherType = Attacher::AttachEngine3D
  Height = 32
  Placement = pos=(42,6e-15,33.5) rot=(0,0,1;1.5708rad)
  Radius = 1.5
FEATURE [Part::Cylinder] Cylinder1093  label="Válec1093"
  Angle = 360
  AttacherType = Attacher::AttachEngine3D
  Height = 32
  Placement = pos=(29.6985,-29.6985,33.5) rot=(0,0,1;0.785398rad)
  Radius = 1.5
FEATURE [Part::Compound] Compound857
  Links = -> [Cylinder1081,Cylinder1093,Cylinder1092,Cylinder1091,Cylinder1083,Cylinder1089,Cylinder1090,Cylinder1078]
  Placement = pos=(0,0,4) rot=(0,0,1;0.392699rad)
FEATURE [Part::Cut] Cut400
  Base = -> Cut406
  Tool = -> Compound857
FEATURE [Part::Cut] Cut401
  Base = -> Cut400
  Tool = -> Compound855
FEATURE [Part::Compound] Compound861  label="J-midi_actuator-ring-m1.5_v2"
  Links = -> [Cut401,Cut402,Compound858]
  Placement = pos=(0,0,4) rot=(0,0,1;0rad)
FEATURE [Part::Torus] Torus008  label="Anuloid008"
  Angle1 = -180
  Angle2 = 180
  Angle3 = 360
  AttacherType = Attacher::AttachEngine3D
  Placement = pos=(0,0,34) rot=(0,0,1;0rad)
  Radius1 = 46
  Radius2 = 3.1
FEATURE [Part::Box] Box400  label="Krychle400"
  AttacherType = Attacher::AttachEngine3D
  Height = 2
  Length = 6
  Placement = pos=(30.4056,-34.6482,33) rot=(0,0,1;0.785398rad)
  Width = 8
FEATURE [Part::Cylinder] Cylinder1094  label="Válec1094"
  Angle = 360
  AttacherType = Attacher::AttachEngine3D
  Height = 20
  Placement = pos=(-46.4,0,34) rot=(0,0,1;0rad)
  Radius = 3.5
FEATURE [Part::Box] Box401  label="Krychle401"
  AttacherType = Attacher::AttachEngine3D
  Height = 2
  Length = 6
  Placement = pos=(3,46,33) rot=(0,0,1;3.14159rad)
  Width = 8
FEATURE [Part::Box] Box402  label="Krychle402"
  AttacherType = Attacher::AttachEngine3D
  Height = 2
  Length = 6
  Placement = pos=(-3,-46,33) rot=(0,0,1;0rad)
  Width = 8
FEATURE [Part::Cylinder] Cylinder1095  label="Válec1095"
  Angle = 360
  AttacherType = Attacher::AttachEngine3D
  Height = 12
  Radius = 40
FEATURE [Part::Cylinder] Cylinder1096  label="Válec1096"
  Angle = 360
  AttacherType = Attacher::AttachEngine3D
  Height = 12
  Radius = 40
FEATURE [Part::Box] Box403  label="Krychle403"
  AttacherType = Attacher::AttachEngine3D
  Height = 2
  Length = 6
  Placement = pos=(-46,3,33) rot=(0,0,-1;1.5708rad)
  Width = 8
FEATURE [Part::Box] Box404  label="Krychle404"
  AttacherType = Attacher::AttachEngine3D
  Height = 2
  Length = 6
  Placement = pos=(-3,-46,33) rot=(0,0,1;0rad)
  Width = 8
FEATURE [Part::Box] Box405  label="Krychle405"
  AttacherType = Attacher::AttachEngine3D
  Height = 2
  Length = 6
  Placement = pos=(-46,3,33) rot=(0,0,-1;1.5708rad)
  Width = 8
FEATURE [Part::Box] Box406  label="Krychle406"
  AttacherType = Attacher::AttachEngine3D
  Height = 2
  Length = 6
  Placement = pos=(-34.6482,-30.4056,33) rot=(0,0,-1;0.785398rad)
  Width = 8
FEATURE [Part::Box] Box407  label="Krychle407"
  AttacherType = Attacher::AttachEngine3D
  Height = 2
  Length = 6
  Placement = pos=(46,-3,33) rot=(0,0,1;1.5708rad)
  Width = 8
FEATURE [Part::Box] Box408  label="Krychle408"
  AttacherType = Attacher::AttachEngine3D
  Height = 2
  Length = 6
  Placement = pos=(34.6482,30.4056,33) rot=(0,0,1;2.35619rad)
  Width = 8
FEATURE [Part::Box] Box409  label="Krychle409"
  AttacherType = Attacher::AttachEngine3D
  Height = 2
  Length = 6
  Placement = pos=(30.4056,-34.6482,33) rot=(0,0,1;0.785398rad)
  Width = 8
FEATURE [Part::Box] Box410  label="Krychle410"
  AttacherType = Attacher::AttachEngine3D
  Height = 2
  Length = 6
  Placement = pos=(-30.4056,34.6482,33) rot=(0,0,1;3.92699rad)
  Width = 8
FEATURE [Part::Compound] Compound863
  Links = -> [Box406,Box400,Box407,Box404,Box408,Box401,Box410,Box403]
  Placement = pos=(0,0,7) rot=(0,0,1;0.392699rad)
FEATURE [Part::Box] Box411  label="Krychle411"
  AttacherType = Attacher::AttachEngine3D
  Height = 2
  Length = 6
  Placement = pos=(46,-3,33) rot=(0,0,1;1.5708rad)
  Width = 8
FEATURE [Part::Box] Box412  label="Krychle412"
  AttacherType = Attacher::AttachEngine3D
  Height = 2
  Length = 6
  Placement = pos=(3,46,33) rot=(0,0,1;3.14159rad)
  Width = 8
FEATURE [Part::Cylinder] Cylinder1097  label="Válec1097"
  Angle = 360
  AttacherType = Attacher::AttachEngine3D
  Height = 20
  Placement = pos=(-46.4,0,34) rot=(0,0,1;0rad)
  Radius = 3.5
FEATURE [Part::Cylinder] Cylinder1098  label="Válec1098"
  Angle = 360
  AttacherType = Attacher::AttachEngine3D
  Height = 32
  Placement = pos=(-29.6985,-29.6985,33.5) rot=(0,0,-1;0.785398rad)
  Radius = 1.5
FEATURE [Part::Cylinder] Cylinder1099  label="Válec1099"
  Angle = 360
  AttacherType = Attacher::AttachEngine3D
  Height = 12
  Placement = pos=(-29.6985,-29.6985,33.5) rot=(0,0,-1;0.785398rad)
  Radius = 1.5
FEATURE [Part::Cylinder] Cylinder1100  label="Válec1100"
  Angle = 360
  AttacherType = Attacher::AttachEngine3D
  Height = 12
  Placement = pos=(29.6985,-29.6985,33.5) rot=(0,0,1;0.785398rad)
  Radius = 1.5
FEATURE [Part::Box] Box413  label="Krychle413"
  AttacherType = Attacher::AttachEngine3D
  Height = 2
  Length = 6
  Placement = pos=(-34.6482,-30.4056,33) rot=(0,0,-1;0.785398rad)
  Width = 8
FEATURE [Part::Cylinder] Cylinder1101  label="Válec1101"
  Angle = 360
  AttacherType = Attacher::AttachEngine3D
  Height = 32
  Placement = pos=(0,-42,33.5) rot=(0,0,1;0rad)
  Radius = 1.5
FEATURE [Part::Cylinder] Cylinder1102  label="Válec1102"
  Angle = 360
  AttacherType = Attacher::AttachEngine3D
  Height = 12
  Placement = pos=(0,-42,33.5) rot=(0,0,1;0rad)
  Radius = 1.5
FEATURE [Part::Cylinder] Cylinder1103  label="Válec1103"
  Angle = 360
  AttacherType = Attacher::AttachEngine3D
  Height = 32
  Placement = pos=(-1.4e-14,42,33.5) rot=(0,0,1;3.14159rad)
  Radius = 1.5
FEATURE [Part::Cylinder] Cylinder1104  label="Válec1104"
  Angle = 360
  AttacherType = Attacher::AttachEngine3D
  Height = 12
  Placement = pos=(-42,-2.4e-14,33.5) rot=(0,0,-1;1.5708rad)
  Radius = 1.5
FEATURE [Part::Cylinder] Cylinder1105  label="Válec1105"
  Angle = 360
  AttacherType = Attacher::AttachEngine3D
  Height = 12
  Placement = pos=(-1.4e-14,42,33.5) rot=(0,0,1;3.14159rad)
  Radius = 1.5
FEATURE [Part::Box] Box414  label="Krychle414"
  AttacherType = Attacher::AttachEngine3D
  Height = 2
  Length = 6
  Placement = pos=(34.6482,30.4056,33) rot=(0,0,1;2.35619rad)
  Width = 8
FEATURE [Part::Cylinder] Cylinder1106  label="Válec1106"
  Angle = 360
  AttacherType = Attacher::AttachEngine3D
  Height = 12
  Placement = pos=(29.6985,29.6985,33.5) rot=(0,0,1;2.35619rad)
  Radius = 1.5
FEATURE [Part::Box] Box415  label="Krychle415"
  AttacherType = Attacher::AttachEngine3D
  Height = 2
  Length = 6
  Placement = pos=(-34.6482,-30.4056,33) rot=(0,0,-1;0.785398rad)
  Width = 8
FEATURE [Part::Box] Box416  label="Krychle416"
  AttacherType = Attacher::AttachEngine3D
  Height = 2
  Length = 6
  Placement = pos=(-30.4056,34.6482,33) rot=(0,0,1;3.92699rad)
  Width = 8
FEATURE [Part::Compound] Compound866
  Links = -> [Box415,Box409,Box411,Box402,Box414,Box412,Box416,Box405]
  Placement = pos=(0,0,7) rot=(0,0,1;0.392699rad)
FEATURE [Part::Cylinder] Cylinder1107  label="Válec1107"
  Angle = 360
  AttacherType = Attacher::AttachEngine3D
  Height = 12
  Placement = pos=(-29.6985,29.6985,33.5) rot=(0,0,1;3.92699rad)
  Radius = 1.5
FEATURE [Part::Cylinder] Cylinder1108  label="Válec1108"
  Angle = 360
  AttacherType = Attacher::AttachEngine3D
  Height = 12
  Placement = pos=(42,6e-15,33.5) rot=(0,0,1;1.5708rad)
  Radius = 1.5
FEATURE [Part::Compound] Compound867
  Links = -> [Cylinder1102,Cylinder1100,Cylinder1108,Cylinder1106,Cylinder1105,Cylinder1107,Cylinder1104,Cylinder1099]
  Placement = pos=(0,0,4) rot=(0,0,1;0.392699rad)
FEATURE [Part::Box] Box417  label="Krychle417"
  AttacherType = Attacher::AttachEngine3D
  Height = 2
  Length = 6
  Placement = pos=(-30.4056,34.6482,33) rot=(0,0,1;3.92699rad)
  Width = 8
FEATURE [Part::Box] Box418  label="Krychle418"
  AttacherType = Attacher::AttachEngine3D
  Height = 2
  Length = 6
  Placement = pos=(-3,-46,33) rot=(0,0,1;0rad)
  Width = 8
FEATURE [Part::Box] Box419  label="Krychle419"
  AttacherType = Attacher::AttachEngine3D
  Height = 2
  Length = 6
  Placement = pos=(46,-3,33) rot=(0,0,1;1.5708rad)
  Width = 8
FEATURE [Part::Cylinder] Cylinder1109  label="Válec1109"
  Angle = 360
  AttacherType = Attacher::AttachEngine3D
  Height = 32
  Placement = pos=(-29.6985,29.6985,33.5) rot=(0,0,1;3.92699rad)
  Radius = 1.5
FEATURE [Part::Box] Box420  label="Krychle420"
  AttacherType = Attacher::AttachEngine3D
  Height = 2
  Length = 6
  Placement = pos=(-46,3,33) rot=(0,0,-1;1.5708rad)
  Width = 8
FEATURE [Part::Box] Box421  label="Krychle421"
  AttacherType = Attacher::AttachEngine3D
  Height = 2
  Length = 6
  Placement = pos=(30.4056,-34.6482,33) rot=(0,0,1;0.785398rad)
  Width = 8
FEATURE [Part::FeaturePython] wormgear063  # WARN: FeaturePython — macro-defined, semantics opaque (R4)
  AttacherType = Attacher::AttachEngine3D
  Placement = pos=(0,0,0) rot=(0,0,-1;0.1309rad)
  beta = 38.6598
  clearance = 0.25
  diameter = 67.5
  head = 0
  height = 14
  module = 1.5
  pressure_angle = 20
  reverse_pitch = false
  teeth = 36
  version = 0.0.3
FEATURE [Part::Cut] Cut408
  Base = -> Cylinder1096
  Placement = pos=(0,0,21) rot=(0,0,1;0.258309rad)
  Tool = -> wormgear063
FEATURE [Part::FeaturePython] Tube098  # WARN: FeaturePython — macro-defined, semantics opaque (R4)
  AttacherType = Attacher::AttachEngine3D
  Height = 24
  InnerRadius = 40
  OuterRadius = 46
  Placement = pos=(0,0,21) rot=(0,0,1;0rad)
FEATURE [Part::Cut] Cut409
  Base = -> Tube098
  Tool = -> Torus008
FEATURE [Part::Cut] Cut416
  Base = -> Cut409
  Tool = -> Cylinder1094
FEATURE [Part::FeaturePython] wormgear064  # WARN: FeaturePython — macro-defined, semantics opaque (R4)
  AttacherType = Attacher::AttachEngine3D
  Placement = pos=(0,0,0) rot=(0,0,1;0.10472rad)
  beta = 38.6598
  clearance = 0.25
  diameter = 67.5
  head = 0
  height = 14
  module = 1.5
  pressure_angle = 20
  reverse_pitch = true
  teeth = 36
  version = 0.0.3
FEATURE [Part::Cut] Cut413
  Base = -> Cylinder1095
  Placement = pos=(0,0,33) rot=(0,0,1;0.466876rad)
  Tool = -> wormgear064
FEATURE [Part::Cut] Cut417
  Base = -> Cut413
  Tool = -> Compound863
FEATURE [Part::Compound] Compound865
  Links = -> [Cut417,Cut408]
FEATURE [Part::FeaturePython] Tube099  # WARN: FeaturePython — macro-defined, semantics opaque (R4)
  AttacherType = Attacher::AttachEngine3D
  Height = 1
  InnerRadius = 36
  OuterRadius = 46
  Placement = pos=(0,0,45) rot=(0,0,1;0rad)
FEATURE [Part::Cut] Cut414
  Base = -> Tube099
  Tool = -> Cylinder1097
FEATURE [Part::Cut] Cut415
  Base = -> Cut414
  Tool = -> Compound867
FEATURE [Part::Cut] Cut412
  Base = -> Cut415
  Tool = -> Compound866
FEATURE [Part::Cylinder] Cylinder1110  label="Válec1110"
  Angle = 360
  AttacherType = Attacher::AttachEngine3D
  Height = 32
  Placement = pos=(-42,-2.4e-14,33.5) rot=(0,0,-1;1.5708rad)
  Radius = 1.5
FEATURE [Part::Box] Box422  label="Krychle422"
  AttacherType = Attacher::AttachEngine3D
  Height = 2
  Length = 6
  Placement = pos=(3,46,33) rot=(0,0,1;3.14159rad)
  Width = 8
FEATURE [Part::Cylinder] Cylinder1111  label="Válec1111"
  Angle = 360
  AttacherType = Attacher::AttachEngine3D
  Height = 32
  Placement = pos=(29.6985,29.6985,33.5) rot=(0,0,1;2.35619rad)
  Radius = 1.5
FEATURE [Part::Box] Box423  label="Krychle423"
  AttacherType = Attacher::AttachEngine3D
  Height = 2
  Length = 6
  Placement = pos=(34.6482,30.4056,33) rot=(0,0,1;2.35619rad)
  Width = 8
FEATURE [Part::Compound] Compound862
  Links = -> [Box413,Box421,Box419,Box418,Box423,Box422,Box417,Box420]
  Placement = pos=(0,0,7) rot=(0,0,1;0.392699rad)
FEATURE [Part::Cylinder] Cylinder1112  label="Válec1112"
  Angle = 360
  AttacherType = Attacher::AttachEngine3D
  Height = 32
  Placement = pos=(42,6e-15,33.5) rot=(0,0,1;1.5708rad)
  Radius = 1.5
FEATURE [Part::Cylinder] Cylinder1113  label="Válec1113"
  Angle = 360
  AttacherType = Attacher::AttachEngine3D
  Height = 32
  Placement = pos=(29.6985,-29.6985,33.5) rot=(0,0,1;0.785398rad)
  Radius = 1.5
FEATURE [Part::Compound] Compound864
  Links = -> [Cylinder1101,Cylinder1113,Cylinder1112,Cylinder1111,Cylinder1103,Cylinder1109,Cylinder1110,Cylinder1098]
  Placement = pos=(0,0,4) rot=(0,0,1;0.392699rad)
FEATURE [Part::Cut] Cut410
  Base = -> Cut416
  Tool = -> Compound864
FEATURE [Part::Cut] Cut411
  Base = -> Cut410
  Tool = -> Compound862
FEATURE [Part::Compound] Compound868  label="J-midi_actuator-ring-m1.5_v3"
  Links = -> [Cut411,Cut412,Compound865]
  Placement = pos=(0,0,4) rot=(0,0,1;0rad)
FEATURE [Part::Torus] Torus009  label="Anuloid009"
  Angle1 = -180
  Angle2 = 180
  Angle3 = 360
  AttacherType = Attacher::AttachEngine3D
  Placement = pos=(0,0,34) rot=(0,0,1;0rad)
  Radius1 = 46
  Radius2 = 3.1
FEATURE [Part::Box] Box424  label="Krychle424"
  AttacherType = Attacher::AttachEngine3D
  Height = 2
  Length = 6
  Placement = pos=(30.4056,-34.6482,33) rot=(0,0,1;0.785398rad)
  Width = 8
FEATURE [Part::Cylinder] Cylinder1114  label="Válec1114"
  Angle = 360
  AttacherType = Attacher::AttachEngine3D
  Height = 20
  Placement = pos=(-46.4,0,34) rot=(0,0,1;0rad)
  Radius = 3.5
FEATURE [Part::Box] Box425  label="Krychle425"
  AttacherType = Attacher::AttachEngine3D
  Height = 2
  Length = 6
  Placement = pos=(3,46,33) rot=(0,0,1;3.14159rad)
  Width = 8
FEATURE [Part::Box] Box426  label="Krychle426"
  AttacherType = Attacher::AttachEngine3D
  Height = 2
  Length = 6
  Placement = pos=(-3,-46,33) rot=(0,0,1;0rad)
  Width = 8
FEATURE [Part::Cylinder] Cylinder1115  label="Válec1115"
  Angle = 360
  AttacherType = Attacher::AttachEngine3D
  Height = 12
  Radius = 40
FEATURE [Part::Cylinder] Cylinder1116  label="Válec1116"
  Angle = 360
  AttacherType = Attacher::AttachEngine3D
  Height = 12
  Radius = 40
FEATURE [Part::Box] Box427  label="Krychle427"
  AttacherType = Attacher::AttachEngine3D
  Height = 2
  Length = 6
  Placement = pos=(-46,3,33) rot=(0,0,-1;1.5708rad)
  Width = 8
FEATURE [Part::Box] Box428  label="Krychle428"
  AttacherType = Attacher::AttachEngine3D
  Height = 2
  Length = 6
  Placement = pos=(-3,-46,33) rot=(0,0,1;0rad)
  Width = 8
FEATURE [Part::Box] Box429  label="Krychle429"
  AttacherType = Attacher::AttachEngine3D
  Height = 2
  Length = 6
  Placement = pos=(-46,3,33) rot=(0,0,-1;1.5708rad)
  Width = 8
FEATURE [Part::Box] Box430  label="Krychle430"
  AttacherType = Attacher::AttachEngine3D
  Height = 2
  Length = 6
  Placement = pos=(-34.6482,-30.4056,33) rot=(0,0,-1;0.785398rad)
  Width = 8
FEATURE [Part::Box] Box431  label="Krychle431"
  AttacherType = Attacher::AttachEngine3D
  Height = 2
  Length = 6
  Placement = pos=(46,-3,33) rot=(0,0,1;1.5708rad)
  Width = 8
FEATURE [Part::Box] Box432  label="Krychle432"
  AttacherType = Attacher::AttachEngine3D
  Height = 2
  Length = 6
  Placement = pos=(34.6482,30.4056,33) rot=(0,0,1;2.35619rad)
  Width = 8
FEATURE [Part::Box] Box433  label="Krychle433"
  AttacherType = Attacher::AttachEngine3D
  Height = 2
  Length = 6
  Placement = pos=(30.4056,-34.6482,33) rot=(0,0,1;0.785398rad)
  Width = 8
FEATURE [Part::Box] Box434  label="Krychle434"
  AttacherType = Attacher::AttachEngine3D
  Height = 2
  Length = 6
  Placement = pos=(-30.4056,34.6482,33) rot=(0,0,1;3.92699rad)
  Width = 8
FEATURE [Part::Compound] Compound870
  Links = -> [Box430,Box424,Box431,Box428,Box432,Box425,Box434,Box427]
  Placement = pos=(0,0,7) rot=(0,0,1;0.392699rad)
FEATURE [Part::Box] Box435  label="Krychle435"
  AttacherType = Attacher::AttachEngine3D
  Height = 2
  Length = 6
  Placement = pos=(46,-3,33) rot=(0,0,1;1.5708rad)
  Width = 8
FEATURE [Part::Box] Box436  label="Krychle436"
  AttacherType = Attacher::AttachEngine3D
  Height = 2
  Length = 6
  Placement = pos=(3,46,33) rot=(0,0,1;3.14159rad)
  Width = 8
FEATURE [Part::Cylinder] Cylinder1117  label="Válec1117"
  Angle = 360
  AttacherType = Attacher::AttachEngine3D
  Height = 20
  Placement = pos=(-46.4,0,34) rot=(0,0,1;0rad)
  Radius = 3.5
FEATURE [Part::Cylinder] Cylinder1118  label="Válec1118"
  Angle = 360
  AttacherType = Attacher::AttachEngine3D
  Height = 32
  Placement = pos=(-29.6985,-29.6985,33.5) rot=(0,0,-1;0.785398rad)
  Radius = 1.5
FEATURE [Part::Cylinder] Cylinder1119  label="Válec1119"
  Angle = 360
  AttacherType = Attacher::AttachEngine3D
  Height = 12
  Placement = pos=(-29.6985,-29.6985,33.5) rot=(0,0,-1;0.785398rad)
  Radius = 1.5
FEATURE [Part::Cylinder] Cylinder1120  label="Válec1120"
  Angle = 360
  AttacherType = Attacher::AttachEngine3D
  Height = 12
  Placement = pos=(29.6985,-29.6985,33.5) rot=(0,0,1;0.785398rad)
  Radius = 1.5
FEATURE [Part::Box] Box437  label="Krychle437"
  AttacherType = Attacher::AttachEngine3D
  Height = 2
  Length = 6
  Placement = pos=(-34.6482,-30.4056,33) rot=(0,0,-1;0.785398rad)
  Width = 8
FEATURE [Part::Cylinder] Cylinder1121  label="Válec1121"
  Angle = 360
  AttacherType = Attacher::AttachEngine3D
  Height = 32
  Placement = pos=(0,-42,33.5) rot=(0,0,1;0rad)
  Radius = 1.5
FEATURE [Part::Cylinder] Cylinder1122  label="Válec1122"
  Angle = 360
  AttacherType = Attacher::AttachEngine3D
  Height = 12
  Placement = pos=(0,-42,33.5) rot=(0,0,1;0rad)
  Radius = 1.5
FEATURE [Part::Cylinder] Cylinder1123  label="Válec1123"
  Angle = 360
  AttacherType = Attacher::AttachEngine3D
  Height = 32
  Placement = pos=(-1.4e-14,42,33.5) rot=(0,0,1;3.14159rad)
  Radius = 1.5
FEATURE [Part::Cylinder] Cylinder1124  label="Válec1124"
  Angle = 360
  AttacherType = Attacher::AttachEngine3D
  Height = 12
  Placement = pos=(-42,-2.4e-14,33.5) rot=(0,0,-1;1.5708rad)
  Radius = 1.5
FEATURE [Part::Cylinder] Cylinder1125  label="Válec1125"
  Angle = 360
  AttacherType = Attacher::AttachEngine3D
  Height = 12
  Placement = pos=(-1.4e-14,42,33.5) rot=(0,0,1;3.14159rad)
  Radius = 1.5
FEATURE [Part::Box] Box438  label="Krychle438"
  AttacherType = Attacher::AttachEngine3D
  Height = 2
  Length = 6
  Placement = pos=(34.6482,30.4056,33) rot=(0,0,1;2.35619rad)
  Width = 8
FEATURE [Part::Cylinder] Cylinder1126  label="Válec1126"
  Angle = 360
  AttacherType = Attacher::AttachEngine3D
  Height = 12
  Placement = pos=(29.6985,29.6985,33.5) rot=(0,0,1;2.35619rad)
  Radius = 1.5
FEATURE [Part::Box] Box439  label="Krychle439"
  AttacherType = Attacher::AttachEngine3D
  Height = 2
  Length = 6
  Placement = pos=(-34.6482,-30.4056,33) rot=(0,0,-1;0.785398rad)
  Width = 8
FEATURE [Part::Box] Box440  label="Krychle440"
  AttacherType = Attacher::AttachEngine3D
  Height = 2
  Length = 6
  Placement = pos=(-30.4056,34.6482,33) rot=(0,0,1;3.92699rad)
  Width = 8
FEATURE [Part::Compound] Compound873
  Links = -> [Box439,Box433,Box435,Box426,Box438,Box436,Box440,Box429]
  Placement = pos=(0,0,7) rot=(0,0,1;0.392699rad)
FEATURE [Part::Cylinder] Cylinder1127  label="Válec1127"
  Angle = 360
  AttacherType = Attacher::AttachEngine3D
  Height = 12
  Placement = pos=(-29.6985,29.6985,33.5) rot=(0,0,1;3.92699rad)
  Radius = 1.5
FEATURE [Part::Cylinder] Cylinder1128  label="Válec1128"
  Angle = 360
  AttacherType = Attacher::AttachEngine3D
  Height = 12
  Placement = pos=(42,6e-15,33.5) rot=(0,0,1;1.5708rad)
  Radius = 1.5
FEATURE [Part::Compound] Compound874
  Links = -> [Cylinder1122,Cylinder1120,Cylinder1128,Cylinder1126,Cylinder1125,Cylinder1127,Cylinder1124,Cylinder1119]
  Placement = pos=(0,0,4) rot=(0,0,1;0.392699rad)
FEATURE [Part::Box] Box441  label="Krychle441"
  AttacherType = Attacher::AttachEngine3D
  Height = 2
  Length = 6
  Placement = pos=(-30.4056,34.6482,33) rot=(0,0,1;3.92699rad)
  Width = 8
FEATURE [Part::Box] Box442  label="Krychle442"
  AttacherType = Attacher::AttachEngine3D
  Height = 2
  Length = 6
  Placement = pos=(-3,-46,33) rot=(0,0,1;0rad)
  Width = 8
FEATURE [Part::Box] Box443  label="Krychle443"
  AttacherType = Attacher::AttachEngine3D
  Height = 2
  Length = 6
  Placement = pos=(46,-3,33) rot=(0,0,1;1.5708rad)
  Width = 8
FEATURE [Part::Cylinder] Cylinder1129  label="Válec1129"
  Angle = 360
  AttacherType = Attacher::AttachEngine3D
  Height = 32
  Placement = pos=(-29.6985,29.6985,33.5) rot=(0,0,1;3.92699rad)
  Radius = 1.5
FEATURE [Part::Box] Box444  label="Krychle444"
  AttacherType = Attacher::AttachEngine3D
  Height = 2
  Length = 6
  Placement = pos=(-46,3,33) rot=(0,0,-1;1.5708rad)
  Width = 8
FEATURE [Part::Box] Box445  label="Krychle445"
  AttacherType = Attacher::AttachEngine3D
  Height = 2
  Length = 6
  Placement = pos=(30.4056,-34.6482,33) rot=(0,0,1;0.785398rad)
  Width = 8
FEATURE [Part::Cylinder] Cylinder1130  label="Válec1130"
  Angle = 360
  AttacherType = Attacher::AttachEngine3D
  Height = 32
  Placement = pos=(-42,-2.4e-14,33.5) rot=(0,0,-1;1.5708rad)
  Radius = 1.5
FEATURE [Part::Box] Box446  label="Krychle446"
  AttacherType = Attacher::AttachEngine3D
  Height = 2
  Length = 6
  Placement = pos=(3,46,33) rot=(0,0,1;3.14159rad)
  Width = 8
FEATURE [Part::Cylinder] Cylinder1131  label="Válec1131"
  Angle = 360
  AttacherType = Attacher::AttachEngine3D
  Height = 32
  Placement = pos=(29.6985,29.6985,33.5) rot=(0,0,1;2.35619rad)
  Radius = 1.5
FEATURE [Part::Box] Box447  label="Krychle447"
  AttacherType = Attacher::AttachEngine3D
  Height = 2
  Length = 6
  Placement = pos=(34.6482,30.4056,33) rot=(0,0,1;2.35619rad)
  Width = 8
FEATURE [Part::Compound] Compound869
  Links = -> [Box437,Box445,Box443,Box442,Box447,Box446,Box441,Box444]
  Placement = pos=(0,0,7) rot=(0,0,1;0.392699rad)
FEATURE [Part::Cylinder] Cylinder1132  label="Válec1132"
  Angle = 360
  AttacherType = Attacher::AttachEngine3D
  Height = 32
  Placement = pos=(42,6e-15,33.5) rot=(0,0,1;1.5708rad)
  Radius = 1.5
FEATURE [Part::Cylinder] Cylinder1133  label="Válec1133"
  Angle = 360
  AttacherType = Attacher::AttachEngine3D
  Height = 32
  Placement = pos=(29.6985,-29.6985,33.5) rot=(0,0,1;0.785398rad)
  Radius = 1.5
FEATURE [Part::Compound] Compound871
  Links = -> [Cylinder1121,Cylinder1133,Cylinder1132,Cylinder1131,Cylinder1123,Cylinder1129,Cylinder1130,Cylinder1118]
  Placement = pos=(0,0,4) rot=(0,0,1;0.392699rad)
FEATURE [Part::FeaturePython] wormgear065  # WARN: FeaturePython — macro-defined, semantics opaque (R4)
  AttacherType = Attacher::AttachEngine3D
  Placement = pos=(0,0,0) rot=(0,0,-1;0.1309rad)
  beta = 38.7636
  clearance = 0.25
  diameter = 67.25
  head = 0
  height = 14
  module = 1.5
  pressure_angle = 20
  reverse_pitch = false
  teeth = 36
  version = 0.0.3
FEATURE [Part::Cut] Cut418
  Base = -> Cylinder1116
  Placement = pos=(0,0,21) rot=(0,0,1;0.258309rad)
  Tool = -> wormgear065
FEATURE [Part::FeaturePython] Tube100  # WARN: FeaturePython — macro-defined, semantics opaque (R4)
  AttacherType = Attacher::AttachEngine3D
  Height = 24
  InnerRadius = 40
  OuterRadius = 46
  Placement = pos=(0,0,21) rot=(0,0,1;0rad)
FEATURE [Part::Cut] Cut419
  Base = -> Tube100
  Tool = -> Torus009
FEATURE [Part::Cut] Cut426
  Base = -> Cut419
  Tool = -> Cylinder1114
FEATURE [Part::Cut] Cut420
  Base = -> Cut426
  Tool = -> Compound871
FEATURE [Part::Cut] Cut421
  Base = -> Cut420
  Tool = -> Compound869
FEATURE [Part::FeaturePython] wormgear066  # WARN: FeaturePython — macro-defined, semantics opaque (R4)
  AttacherType = Attacher::AttachEngine3D
  Placement = pos=(0,0,0) rot=(0,0,1;0.10472rad)
  beta = 38.7636
  clearance = 0.25
  diameter = 67.25
  head = 0
  height = 14
  module = 1.5
  pressure_angle = 20
  reverse_pitch = true
  teeth = 36
  version = 0.0.3
FEATURE [Part::Cut] Cut423
  Base = -> Cylinder1115
  Placement = pos=(0,0,33) rot=(0,0,1;0.466876rad)
  Tool = -> wormgear066
FEATURE [Part::Cut] Cut427
  Base = -> Cut423
  Tool = -> Compound870
FEATURE [Part::Compound] Compound872
  Links = -> [Cut427,Cut418]
FEATURE [Part::FeaturePython] Tube101  # WARN: FeaturePython — macro-defined, semantics opaque (R4)
  AttacherType = Attacher::AttachEngine3D
  Height = 1
  InnerRadius = 36
  OuterRadius = 46
  Placement = pos=(0,0,45) rot=(0,0,1;0rad)
FEATURE [Part::Cut] Cut424
  Base = -> Tube101
  Tool = -> Cylinder1117
FEATURE [Part::Cut] Cut425
  Base = -> Cut424
  Tool = -> Compound874
FEATURE [Part::Cut] Cut422
  Base = -> Cut425
  Tool = -> Compound873
FEATURE [Part::Compound] Compound875  label="J-midi_actuator-ring-m1.5_v4"
  Links = -> [Cut421,Cut422,Compound872]
  Placement = pos=(0,0,4) rot=(0,0,1;0rad)
FEATURE [Part::Cylinder] Cylinder1134  label="Válec1134"
  Angle = 360
  AttacherType = Attacher::AttachEngine3D
  Height = 20
  Placement = pos=(4.25,4.25,-88) rot=(0,0,1;3.14159rad)
  Radius = 1
FEATURE [Part::Cylinder] Cylinder1135  label="Válec1135"
  Angle = 360
  AttacherType = Attacher::AttachEngine3D
  Height = 4
  Placement = pos=(0,0,15) rot=(0,0,1;0rad)
  Radius = 8
FEATURE [Part::Cylinder] Cylinder1136  label="Válec1136"
  Angle = 360
  AttacherType = Attacher::AttachEngine3D
  Height = 20
  Placement = pos=(-4.25,4.25,-88) rot=(0,0,-1;1.5708rad)
  Radius = 1
FEATURE [Part::Cylinder] Cylinder1137  label="Válec1137"
  Angle = 360
  AttacherType = Attacher::AttachEngine3D
  Height = 20
  Placement = pos=(4.25,-4.25,-88) rot=(0,0,1;1.5708rad)
  Radius = 1
FEATURE [Part::Cylinder] Cylinder1138  label="Válec1138"
  Angle = 360
  AttacherType = Attacher::AttachEngine3D
  Height = 20
  Placement = pos=(-4.25,4.25,-88) rot=(0,0,-1;1.5708rad)
  Radius = 1
FEATURE [Part::Cylinder] Cylinder1139  label="Válec1139"
  Angle = 360
  AttacherType = Attacher::AttachEngine3D
  Height = 2
  Placement = pos=(-4.25,-4.25,-88) rot=(0,0,1;0rad)
  Radius = 2
FEATURE [Part::Cylinder] Cylinder1140  label="Válec1140"
  Angle = 360
  AttacherType = Attacher::AttachEngine3D
  Height = 20
  Placement = pos=(-4.25,-4.25,-88) rot=(0,0,1;0rad)
  Radius = 1
FEATURE [Part::Cylinder] Cylinder1141  label="Válec1141"
  Angle = 360
  AttacherType = Attacher::AttachEngine3D
  Height = 2
  Placement = pos=(-4.25,4.25,-88) rot=(0,0,-1;1.5708rad)
  Radius = 2
FEATURE [Part::Cylinder] Cylinder1142  label="Válec1142"
  Angle = 360
  AttacherType = Attacher::AttachEngine3D
  Height = 2
  Placement = pos=(4.25,4.25,-88) rot=(0,0,1;3.14159rad)
  Radius = 2
FEATURE [Part::Cylinder] Cylinder1143  label="Válec1143"
  Angle = 360
  AttacherType = Attacher::AttachEngine3D
  Height = 20
  Placement = pos=(4.25,-4.25,-88) rot=(0,0,1;1.5708rad)
  Radius = 1
FEATURE [Part::Cylinder] Cylinder1144  label="Válec1144"
  Angle = 360
  AttacherType = Attacher::AttachEngine3D
  Height = 20
  Placement = pos=(4.25,-4.25,-88) rot=(0,0,1;1.5708rad)
  Radius = 1
FEATURE [Part::Cylinder] Cylinder1145  label="Válec1145"
  Angle = 360
  AttacherType = Attacher::AttachEngine3D
  Height = 2
  Placement = pos=(4.25,-4.25,-88) rot=(0,0,1;1.5708rad)
  Radius = 2
FEATURE [Part::Cylinder] Cylinder1146  label="Válec1146"
  Angle = 360
  AttacherType = Attacher::AttachEngine3D
  Height = 20
  Placement = pos=(4.25,4.25,-88) rot=(0,0,1;3.14159rad)
  Radius = 1
FEATURE [Part::Cylinder] Cylinder1147  label="Válec1147"
  Angle = 360
  AttacherType = Attacher::AttachEngine3D
  Height = 20
  Placement = pos=(-4.25,4.25,-88) rot=(0,0,-1;1.5708rad)
  Radius = 1
FEATURE [Part::Cylinder] Cylinder1148  label="Válec1148"
  Angle = 360
  AttacherType = Attacher::AttachEngine3D
  Height = 20
  Placement = pos=(4.25,4.25,-88) rot=(0,0,1;3.14159rad)
  Radius = 1
FEATURE [Part::Cylinder] Cylinder1149  label="Válec1149"
  Angle = 360
  AttacherType = Attacher::AttachEngine3D
  Height = 20
  Placement = pos=(-4.25,-4.25,-88) rot=(0,0,1;0rad)
  Radius = 1
FEATURE [Part::Cylinder] Cylinder1150  label="Válec1150"
  Angle = 360
  AttacherType = Attacher::AttachEngine3D
  Height = 20
  Placement = pos=(-4.25,-4.25,-88) rot=(0,0,1;0rad)
  Radius = 1
FEATURE [Part::Cylinder] Cylinder1151  label="Válec1151"
  Angle = 360
  AttacherType = Attacher::AttachEngine3D
  Height = 60
  Placement = pos=(0,0,-10) rot=(0,0,1;0rad)
  Radius = 2.65
FEATURE [Part::Compound] Compound876
  Links = -> [Cylinder1149,Cylinder1137,Cylinder1134,Cylinder1136]
  Placement = pos=(0,0,91) rot=(0,0,1;0rad)
FEATURE [Part::Compound] Compound877
  Links = -> [Cylinder1140,Cylinder1144,Cylinder1146,Cylinder1147]
  Placement = pos=(0,0,91) rot=(0,0,1;0rad)
FEATURE [Part::Wedge] Wedge028  label="Klín028"
  AttacherType = Attacher::AttachEngine3D
  Placement = pos=(0,0,12) rot=(0,0,1;0rad)
  X2max = 0
  X2min = 0
  Xmax = 10
  Xmin = -10
  Ymax = 0
  Ymin = -32
  Z2max = 12
  Z2min = 0
  Zmax = 12
  Zmin = 0
FEATURE [Part::FeaturePython] Tube102  # WARN: FeaturePython — macro-defined, semantics opaque (R4)
  AttacherType = Attacher::AttachEngine3D
  Height = 10
  InnerRadius = 2.65
  OuterRadius = 8
  Placement = pos=(0,0,19) rot=(0,0,1;0rad)
FEATURE [Part::Cut] Cut428
  Base = -> Tube102
  Tool = -> Compound877
FEATURE [Part::FeaturePython] wormgear067  # WARN: FeaturePython — macro-defined, semantics opaque (R4)
  AttacherType = Attacher::AttachEngine3D
  Placement = pos=(0,0,29) rot=(0,0,1;0.994838rad)
  beta = 40.6013
  clearance = 0.25
  diameter = 21
  head = 0.25
  height = 12
  module = 1.5
  pressure_angle = 20
  reverse_pitch = false
  teeth = 12
  version = 0.0.3
FEATURE [Part::Cut] Cut430
  Base = -> wormgear067
  Tool = -> Cylinder1151
FEATURE [Part::FeaturePython] Tube103  # WARN: FeaturePython — macro-defined, semantics opaque (R4)
  AttacherType = Attacher::AttachEngine3D
  Height = 12
  InnerRadius = 4.1
  OuterRadius = 8
  Placement = pos=(0,0,12) rot=(0,0,1;0rad)
FEATURE [Part::Wedge] Wedge029  label="Klín029"
  AttacherType = Attacher::AttachEngine3D
  Placement = pos=(0,0,12) rot=(0,0,1;3.14159rad)
  X2max = 0
  X2min = 0
  Xmax = 10
  Xmin = -10
  Ymax = 0
  Ymin = -32
  Z2max = 12
  Z2min = 0
  Zmax = 12
  Zmin = 0
FEATURE [Part::Wedge] Wedge030  label="Klín030"
  AttacherType = Attacher::AttachEngine3D
  Placement = pos=(0,0,12) rot=(0,0,1;1.5708rad)
  X2max = 0
  X2min = 0
  Xmax = 10
  Xmin = -10
  Ymax = 0
  Ymin = -32
  Z2max = 12
  Z2min = 0
  Zmax = 12
  Zmin = 0
FEATURE [Part::Wedge] Wedge031  label="Klín031"
  AttacherType = Attacher::AttachEngine3D
  Placement = pos=(0,0,12) rot=(0,0,-1;1.5708rad)
  X2max = 0
  X2min = 0
  Xmax = 10
  Xmin = -10
  Ymax = 0
  Ymin = -32
  Z2max = 12
  Z2min = 0
  Zmax = 12
  Zmin = 0
FEATURE [Part::Compound] Compound879
  Links = -> [Wedge028,Wedge030,Wedge029,Wedge031]
FEATURE [Part::Cut] Cut433
  Base = -> Tube103
  Placement = pos=(0,0,-9) rot=(0,0,1;0rad)
  Tool = -> Compound879
FEATURE [Part::Compound] Compound880
  Links = -> [Cylinder1139,Cylinder1145,Cylinder1142,Cylinder1141]
  Placement = pos=(0,0,91) rot=(0,0,1;0rad)
FEATURE [Part::Compound] Compound881
  Links = -> [Cylinder1150,Cylinder1143,Cylinder1148,Cylinder1138]
  Placement = pos=(0,0,91) rot=(0,0,1;0rad)
FEATURE [Part::Cut] Cut429
  Base = -> Cylinder1135
  Tool = -> Compound881
FEATURE [Part::Chamfer] Chamfer029
  Base = -> Cut433
  Edges = 8 edges r=1: [Edge7,Edge8,Edge21,Edge22,Edge31,Edge32,Edge45,Edge46]
FEATURE [Part::Cut] Cut432
  Base = -> Chamfer029
  Tool = -> Compound880
FEATURE [Part::Cut] Cut431
  Base = -> Cut432
  Tool = -> Compound876
FEATURE [Part::Compound] Compound878  label="J-midi_inner-planeo-m1.5-reinforced_v3"
  Links = -> [Cut430,Cut431,Cut429,Cut428]
  Placement = pos=(0,0,8) rot=(0,0,1;0.10472rad)
FEATURE [Part::FeaturePython] Tube037  # WARN: FeaturePython — macro-defined, semantics opaque (R4)
  AttacherType = Attacher::AttachEngine3D
  Height = 5
  InnerRadius = 12
  OuterRadius = 46
  Placement = pos=(0,0,-100) rot=(0,0,1;0rad)
FEATURE [Part::FeaturePython] Tube038  # WARN: FeaturePython — macro-defined, semantics opaque (R4)
  AttacherType = Attacher::AttachEngine3D
  Height = 4
  InnerRadius = 12
  OuterRadius = 24.8
  Placement = pos=(0,0,-103) rot=(0,0,1;0rad)
FEATURE [Part::FeaturePython] Tube039  # WARN: FeaturePython — macro-defined, semantics opaque (R4)
  AttacherType = Attacher::AttachEngine3D
  Height = 11
  InnerRadius = 12
  OuterRadius = 20
  Placement = pos=(0,0,-111) rot=(0,0,1;0rad)
FEATURE [Part::Box] Box181  label="Krychle181"
  AttacherType = Attacher::AttachEngine3D
  Height = 2
  Length = 10
  Placement = pos=(11,-3,6) rot=(0,0,1;0rad)
  Width = 6
FEATURE [Part::Box] Box182  label="Krychle182"
  AttacherType = Attacher::AttachEngine3D
  Height = 2
  Length = 10
  Placement = pos=(-11,3,6) rot=(0,0,1;3.14159rad)
  Width = 6
FEATURE [Part::Box] Box183  label="Krychle183"
  AttacherType = Attacher::AttachEngine3D
  Height = 2
  Length = 10
  Placement = pos=(-3,-11,6) rot=(0,0,-1;1.5708rad)
  Width = 6
FEATURE [Part::Cylinder] Cylinder415  label="Válec415"
  Angle = 360
  AttacherType = Attacher::AttachEngine3D
  Height = 16
  Placement = pos=(-16,7e-15,2) rot=(0,0,1;0.392699rad)
  Radius = 1.5
FEATURE [Part::Cylinder] Cylinder273  label="Válec273"
  Angle = 360
  AttacherType = Attacher::AttachEngine3D
  Height = 16
  Placement = pos=(-16,7e-15,2) rot=(0,0,1;0.392699rad)
  Radius = 1.5
FEATURE [Part::Cylinder] Cylinder416  label="Válec416"
  Angle = 360
  AttacherType = Attacher::AttachEngine3D
  Height = 16
  Placement = pos=(-16,7e-15,2) rot=(0,0,1;0.392699rad)
  Radius = 1.5
FEATURE [Part::Cylinder] Cylinder417  label="Válec417"
  Angle = 360
  AttacherType = Attacher::AttachEngine3D
  Height = 16
  Placement = pos=(2e-15,16,2) rot=(0,0,-1;1.1781rad)
  Radius = 1.5
FEATURE [Part::Cylinder] Cylinder418  label="Válec418"
  Angle = 360
  AttacherType = Attacher::AttachEngine3D
  Height = 16
  Placement = pos=(16,0,2) rot=(0,0,1;3.53429rad)
  Radius = 1.5
FEATURE [Part::Cylinder] Cylinder419  label="Válec419"
  Angle = 360
  AttacherType = Attacher::AttachEngine3D
  Height = 16
  Placement = pos=(2e-15,16,2) rot=(0,0,-1;1.1781rad)
  Radius = 1.5
FEATURE [Part::Cylinder] Cylinder420  label="Válec420"
  Angle = 360
  AttacherType = Attacher::AttachEngine3D
  Height = 16
  Placement = pos=(16,0,2) rot=(0,0,1;3.53429rad)
  Radius = 1.5
FEATURE [Part::Cylinder] Cylinder274  label="Válec274"
  Angle = 360
  AttacherType = Attacher::AttachEngine3D
  Height = 16
  Placement = pos=(-1.2e-14,-16,2) rot=(0,0,1;1.9635rad)
  Radius = 1.5
FEATURE [Part::Box] Box184  label="Krychle184"
  AttacherType = Attacher::AttachEngine3D
  Height = 2
  Length = 10
  Placement = pos=(3,11,6) rot=(0,0,1;1.5708rad)
  Width = 6
FEATURE [Part::Cylinder] Cylinder423  label="Válec423"
  Angle = 360
  AttacherType = Attacher::AttachEngine3D
  Height = 16
  Placement = pos=(2e-15,16,2) rot=(0,0,-1;1.1781rad)
  Radius = 1.5
FEATURE [Part::Cylinder] Cylinder426  label="Válec426"
  Angle = 360
  AttacherType = Attacher::AttachEngine3D
  Height = 16
  Placement = pos=(16,0,2) rot=(0,0,1;3.53429rad)
  Radius = 1.5
FEATURE [Part::Cylinder] Cylinder427  label="Válec427"
  Angle = 360
  AttacherType = Attacher::AttachEngine3D
  Height = 16
  Placement = pos=(-1.2e-14,-16,2) rot=(0,0,1;1.9635rad)
  Radius = 1.5
FEATURE [Part::Cylinder] Cylinder433  label="Válec433"
  Angle = 360
  AttacherType = Attacher::AttachEngine3D
  Height = 16
  Placement = pos=(-1.2e-14,-16,2) rot=(0,0,1;1.9635rad)
  Radius = 1.5
FEATURE [Part::Cylinder] Cylinder434  label="Válec434"
  Angle = 360
  AttacherType = Attacher::AttachEngine3D
  Height = 60
  Placement = pos=(-28.9914,-28.9914,-54) rot=(0,0,1;3.92699rad)
  Radius = 1.5
FEATURE [Part::Cylinder] Cylinder435  label="Válec435"
  Angle = 360
  AttacherType = Attacher::AttachEngine3D
  Height = 60
  Placement = pos=(41,0,-54) rot=(0,0,1;0rad)
  Radius = 1.5
FEATURE [Part::Cylinder] Cylinder436  label="Válec436"
  Angle = 360
  AttacherType = Attacher::AttachEngine3D
  Height = 60
  Placement = pos=(-4e-15,41,-54) rot=(0,0,1;1.5708rad)
  Radius = 1.5
FEATURE [Part::Cylinder] Cylinder437  label="Válec437"
  Angle = 360
  AttacherType = Attacher::AttachEngine3D
  Height = 60
  Placement = pos=(28.9914,28.9914,-54) rot=(0,0,1;0.785398rad)
  Radius = 1.5
FEATURE [Part::Cylinder] Cylinder438  label="Válec438"
  Angle = 360
  AttacherType = Attacher::AttachEngine3D
  Height = 60
  Placement = pos=(-28.9914,28.9914,-54) rot=(0,0,1;2.35619rad)
  Radius = 1.5
FEATURE [Part::Cylinder] Cylinder439  label="Válec439"
  Angle = 360
  AttacherType = Attacher::AttachEngine3D
  Height = 60
  Placement = pos=(1.2e-14,-41,-54) rot=(0,0,-1;1.5708rad)
  Radius = 1.5
FEATURE [Part::Cylinder] Cylinder440  label="Válec440"
  Angle = 360
  AttacherType = Attacher::AttachEngine3D
  Height = 60
  Placement = pos=(28.9914,-28.9914,-54) rot=(0,0,-1;0.785398rad)
  Radius = 1.5
FEATURE [Part::Cylinder] Cylinder441  label="Válec441"
  Angle = 360
  AttacherType = Attacher::AttachEngine3D
  Height = 60
  Placement = pos=(-41,-1.1e-14,-54) rot=(0,0,1;3.14159rad)
  Radius = 1.5
FEATURE [Part::Cylinder] Cylinder442  label="Válec442"
  Angle = 360
  AttacherType = Attacher::AttachEngine3D
  Height = 3
  Placement = pos=(28.9914,28.9914,-54) rot=(0,0,1;0.785398rad)
  Radius = 3
FEATURE [Part::Cylinder] Cylinder443  label="Válec443"
  Angle = 360
  AttacherType = Attacher::AttachEngine3D
  Height = 3
  Placement = pos=(1.2e-14,-41,-54) rot=(0,0,-1;1.5708rad)
  Radius = 3
FEATURE [Part::Cylinder] Cylinder444  label="Válec444"
  Angle = 360
  AttacherType = Attacher::AttachEngine3D
  Height = 3
  Placement = pos=(-41,-1.1e-14,-54) rot=(0,0,1;3.14159rad)
  Radius = 3
FEATURE [Part::Cylinder] Cylinder445  label="Válec445"
  Angle = 360
  AttacherType = Attacher::AttachEngine3D
  Height = 3
  Placement = pos=(-4e-15,41,-54) rot=(0,0,1;1.5708rad)
  Radius = 3
FEATURE [Part::Cylinder] Cylinder446  label="Válec446"
  Angle = 360
  AttacherType = Attacher::AttachEngine3D
  Height = 3
  Placement = pos=(-28.9914,-28.9914,-54) rot=(0,0,1;3.92699rad)
  Radius = 3
FEATURE [Part::Cylinder] Cylinder447  label="Válec447"
  Angle = 360
  AttacherType = Attacher::AttachEngine3D
  Height = 3
  Placement = pos=(-28.9914,28.9914,-54) rot=(0,0,1;2.35619rad)
  Radius = 3
FEATURE [Part::Cylinder] Cylinder448  label="Válec448"
  Angle = 360
  AttacherType = Attacher::AttachEngine3D
  Height = 3
  Placement = pos=(28.9914,-28.9914,-54) rot=(0,0,-1;0.785398rad)
  Radius = 3
FEATURE [Part::Compound] Compound308
  Links = -> [Cylinder420,Cylinder423,Cylinder273,Cylinder274]
  Placement = pos=(0,0,-117) rot=(0,0,1;0rad)
FEATURE [Part::Cut] Cut165
  Base = -> Tube038
  Placement = pos=(0,0,-1) rot=(0,0,1;0rad)
  Tool = -> Compound308
FEATURE [Part::Compound] Compound310
  Links = -> [Cylinder426,Cylinder419,Cylinder416,Cylinder427]
  Placement = pos=(0,0,-117) rot=(0,0,1;0rad)
FEATURE [Part::Cut] Cut164
  Base = -> Tube039
  Tool = -> Compound310
FEATURE [Part::Compound] Compound311
  Links = -> [Cylinder418,Cylinder417,Cylinder415,Cylinder433]
  Placement = pos=(0,0,-117) rot=(0,0,1;0rad)
FEATURE [Part::Cut] Cut166
  Base = -> Tube037
  Tool = -> Compound311
FEATURE [Part::Compound] Compound313
  Links = -> [Box181,Box184,Box182,Box183]
  Placement = pos=(0,0,-111) rot=(0,0,1;0rad)
FEATURE [Part::Cut] Cut163
  Base = -> Cut164
  Tool = -> Compound313
FEATURE [Part::Compound] Compound314
  Links = -> [Cylinder437,Cylinder436,Cylinder438,Cylinder441,Cylinder434,Cylinder439,Cylinder440,Cylinder435]
  Placement = pos=(0,0,-80) rot=(0,0,1;0.392699rad)
FEATURE [Part::Cut] Cut167
  Base = -> Cut166
  Tool = -> Compound314
FEATURE [Part::Chamfer] Chamfer004
  Base = -> Cut163
  Edges = 1 edges r=1: [Edge6]
  Placement = pos=(0,0,-1) rot=(0,0,1;0rad)
FEATURE [Part::Cylinder] Cylinder449  label="Válec449"
  Angle = 360
  AttacherType = Attacher::AttachEngine3D
  Height = 3
  Placement = pos=(41,0,-54) rot=(0,0,1;0rad)
  Radius = 3
FEATURE [Part::Compound] Compound315
  Links = -> [Cylinder442,Cylinder445,Cylinder447,Cylinder444,Cylinder446,Cylinder443,Cylinder448,Cylinder449]
  Placement = pos=(0,0,-46) rot=(0,0,1;0.392699rad)
FEATURE [Part::Cut] Cut168
  Base = -> Cut167
  Tool = -> Compound315
FEATURE [Part::Chamfer] Chamfer005
  Base = -> Cut168
  Edges = 1 edges r=1: [Edge3]
FEATURE [Part::Compound] Compound316  label="J-midi_undermotor-cover"
  Links = -> [Cut165,Chamfer004,Chamfer005]
  Placement = pos=(0,0,16) rot=(0,0,1;0rad)
FEATURE [Part::Cylinder] Cylinder670  label="Válec670"
  Angle = 360
  AttacherType = Attacher::AttachEngine3D
  Height = 60
  Placement = pos=(41,0,-54) rot=(0,0,1;0rad)
  Radius = 1.5
FEATURE [Part::Cylinder] Cylinder671  label="Válec671"
  Angle = 360
  AttacherType = Attacher::AttachEngine3D
  Height = 60
  Placement = pos=(28.9914,28.9914,-54) rot=(0,0,1;0.785398rad)
  Radius = 1.5
FEATURE [Part::Cylinder] Cylinder672  label="Válec672"
  Angle = 360
  AttacherType = Attacher::AttachEngine3D
  Height = 60
  Placement = pos=(1.2e-14,-41,-54) rot=(0,0,-1;1.5708rad)
  Radius = 1.5
FEATURE [Part::Cylinder] Cylinder673  label="Válec673"
  Angle = 360
  AttacherType = Attacher::AttachEngine3D
  Height = 60
  Placement = pos=(28.9914,-28.9914,-54) rot=(0,0,-1;0.785398rad)
  Radius = 1.5
FEATURE [Part::Cylinder] Cylinder674  label="Válec674"
  Angle = 360
  AttacherType = Attacher::AttachEngine3D
  Height = 60
  Placement = pos=(-28.9914,-28.9914,-54) rot=(0,0,1;3.92699rad)
  Radius = 1.5
FEATURE [Part::Cylinder] Cylinder675  label="Válec675"
  Angle = 360
  AttacherType = Attacher::AttachEngine3D
  Height = 60
  Placement = pos=(-28.9914,28.9914,-54) rot=(0,0,1;2.35619rad)
  Radius = 1.5
FEATURE [Part::Cylinder] Cylinder676  label="Válec676"
  Angle = 360
  AttacherType = Attacher::AttachEngine3D
  Height = 60
  Placement = pos=(-4e-15,41,-54) rot=(0,0,1;1.5708rad)
  Radius = 1.5
FEATURE [Part::Cylinder] Cylinder677  label="Válec677"
  Angle = 360
  AttacherType = Attacher::AttachEngine3D
  Height = 60
  Placement = pos=(-41,-1.1e-14,-54) rot=(0,0,1;3.14159rad)
  Radius = 1.5
FEATURE [Part::FeaturePython] Tube059  # WARN: FeaturePython — macro-defined, semantics opaque (R4)
  AttacherType = Attacher::AttachEngine3D
  Height = 2
  InnerRadius = 12
  OuterRadius = 46
  Placement = pos=(0,0,-35) rot=(0,0,1;0rad)
FEATURE [Part::FeaturePython] Tube060  # WARN: FeaturePython — macro-defined, semantics opaque (R4)
  AttacherType = Attacher::AttachEngine3D
  Height = 9
  InnerRadius = 27.6
  OuterRadius = 32
  Placement = pos=(0,0,-33) rot=(0,0,1;0rad)
FEATURE [Part::FeaturePython] Tube061  # WARN: FeaturePython — macro-defined, semantics opaque (R4)
  AttacherType = Attacher::AttachEngine3D
  Height = 1
  InnerRadius = 23.6
  OuterRadius = 32
  Placement = pos=(0,0,-33) rot=(0,0,1;0rad)
FEATURE [Part::Compound] Compound686
  Links = -> [Cylinder671,Cylinder676,Cylinder675,Cylinder677,Cylinder674,Cylinder672,Cylinder673,Cylinder670]
  Placement = pos=(0,0,-31) rot=(0,0,1;0.392699rad)
FEATURE [Part::Chamfer] Chamfer020
  Base = -> Tube060
  Edges = 1 edges r=1: [Edge4]
FEATURE [Part::Cut] Cut301
  Base = -> Tube059
  Tool = -> Compound686
FEATURE [Part::Compound] Compound687  label="J-midi_undermotor-undercover"
  Links = -> [Chamfer020,Cut301,Tube061]
  Placement = pos=(0,0,-32) rot=(0,0,1;0rad)
FEATURE [Part::FeaturePython] Tube040  # WARN: FeaturePython — macro-defined, semantics opaque (R4)
  AttacherType = Attacher::AttachEngine3D
  Height = 10
  InnerRadius = 12
  OuterRadius = 20.2
  Placement = pos=(0,0,17) rot=(0,0,1;0rad)
FEATURE [Part::FeaturePython] Tube041  # WARN: FeaturePython — macro-defined, semantics opaque (R4)
  AttacherType = Attacher::AttachEngine3D
  Height = 4
  InnerRadius = 19.5
  OuterRadius = 24.8
  Placement = pos=(0,0,23) rot=(0,0,1;0rad)
FEATURE [Part::Cylinder] Cylinder603  label="Válec603"
  Angle = 360
  AttacherType = Attacher::AttachEngine3D
  Height = 3
  Placement = pos=(-16,7e-15,2) rot=(0,0,1;0.392699rad)
  Radius = 3
FEATURE [Part::Cylinder] Cylinder602  label="Válec602"
  Angle = 360
  AttacherType = Attacher::AttachEngine3D
  Height = 3
  Placement = pos=(2e-15,16,2) rot=(0,0,-1;1.1781rad)
  Radius = 3
FEATURE [Part::Cylinder] Cylinder609  label="Válec609"
  Angle = 360
  AttacherType = Attacher::AttachEngine3D
  Height = 30
  Placement = pos=(16,0,2) rot=(0,0,1;3.53429rad)
  Radius = 1.5
FEATURE [Part::Cylinder] Cylinder607  label="Válec607"
  Angle = 360
  AttacherType = Attacher::AttachEngine3D
  Height = 3
  Placement = pos=(16,0,2) rot=(0,0,1;3.53429rad)
  Radius = 3
FEATURE [Part::Cylinder] Cylinder605  label="Válec605"
  Angle = 360
  AttacherType = Attacher::AttachEngine3D
  Height = 30
  Placement = pos=(2e-15,16,2) rot=(0,0,-1;1.1781rad)
  Radius = 1.5
FEATURE [Part::Box] Box292  label="Krychle292"
  AttacherType = Attacher::AttachEngine3D
  Height = 2
  Length = 10
  Placement = pos=(-3,-11,6) rot=(0,0,-1;1.5708rad)
  Width = 6
FEATURE [Part::Cylinder] Cylinder604  label="Válec604"
  Angle = 360
  AttacherType = Attacher::AttachEngine3D
  Height = 30
  Placement = pos=(16,0,2) rot=(0,0,1;3.53429rad)
  Radius = 1.5
FEATURE [Part::Cylinder] Cylinder610  label="Válec610"
  Angle = 360
  AttacherType = Attacher::AttachEngine3D
  Height = 30
  Placement = pos=(-16,7e-15,2) rot=(0,0,1;0.392699rad)
  Radius = 1.5
FEATURE [Part::Cylinder] Cylinder601  label="Válec601"
  Angle = 360
  AttacherType = Attacher::AttachEngine3D
  Height = 3
  Placement = pos=(-1.2e-14,-16,2) rot=(0,0,1;1.96349rad)
  Radius = 3
FEATURE [Part::Cylinder] Cylinder608  label="Válec608"
  Angle = 360
  AttacherType = Attacher::AttachEngine3D
  Height = 30
  Placement = pos=(-1.2e-14,-16,2) rot=(0,0,1;1.96349rad)
  Radius = 1.5
FEATURE [Part::Box] Box293  label="Krychle293"
  AttacherType = Attacher::AttachEngine3D
  Height = 2
  Length = 10
  Placement = pos=(3,11,6) rot=(0,0,1;1.5708rad)
  Width = 6
FEATURE [Part::Cylinder] Cylinder600  label="Válec600"
  Angle = 360
  AttacherType = Attacher::AttachEngine3D
  Height = 30
  Placement = pos=(-1.2e-14,-16,2) rot=(0,0,1;1.96349rad)
  Radius = 1.5
FEATURE [Part::Cylinder] Cylinder611  label="Válec611"
  Angle = 360
  AttacherType = Attacher::AttachEngine3D
  Height = 30
  Placement = pos=(2e-15,16,2) rot=(0,0,-1;1.1781rad)
  Radius = 1.5
FEATURE [Part::Compound] Compound648
  Links = -> [Cylinder608,Cylinder610,Cylinder611,Cylinder609]
  Placement = pos=(0,0,5) rot=(0,0,1;0.785398rad)
FEATURE [Part::Box] Box290  label="Krychle290"
  AttacherType = Attacher::AttachEngine3D
  Height = 2
  Length = 10
  Placement = pos=(-11,3,6) rot=(0,0,1;3.14159rad)
  Width = 6
FEATURE [Part::Cylinder] Cylinder606  label="Válec606"
  Angle = 360
  AttacherType = Attacher::AttachEngine3D
  Height = 30
  Placement = pos=(-16,7e-15,2) rot=(0,0,1;0.392699rad)
  Radius = 1.5
FEATURE [Part::Compound] Compound647
  Links = -> [Cylinder600,Cylinder606,Cylinder605,Cylinder604]
  Placement = pos=(0,0,-2) rot=(0,0,1;0rad)
FEATURE [Part::Box] Box291  label="Krychle291"
  AttacherType = Attacher::AttachEngine3D
  Height = 2
  Length = 10
  Placement = pos=(11,-3,6) rot=(0,0,1;0rad)
  Width = 6
FEATURE [Part::Compound] Compound650
  Links = -> [Box291,Box293,Box290,Box292]
  Placement = pos=(0,0,15) rot=(0,0,1;0.785398rad)
FEATURE [Part::Compound] Compound646
  Links = -> [Cylinder601,Cylinder603,Cylinder602,Cylinder607]
  Placement = pos=(0,0,22) rot=(0,0,1;0rad)
FEATURE [Part::Cut] Cut276
  Base = -> Tube040
  Tool = -> Compound646
FEATURE [Part::Cut] Cut278
  Base = -> Cut276
  Tool = -> Compound647
FEATURE [Part::Cut] Cut279
  Base = -> Cut278
  Tool = -> Compound650
FEATURE [Part::Cut] Cut277
  Base = -> Cut279
  Tool = -> Compound648
FEATURE [Part::Compound] Compound649
  Links = -> [Tube041,Cut277]
FEATURE [Part::Chamfer] Chamfer016  label="J-midi_arm-bearing-fix"
  Base = -> Compound649
  Edges = 1 edges r=1: [Edge8]
  Placement = pos=(0,0,-128) rot=(0,0,1;0rad)
FEATURE [Part::Wedge] Wedge032  label="Klín032"
  AttacherType = Attacher::AttachEngine3D
  Placement = pos=(0,0,12) rot=(0,0,1;0rad)
  X2max = 0
  X2min = 0
  Xmax = 10
  Xmin = -10
  Ymax = 0
  Ymin = -32
  Z2max = 12
  Z2min = 0
  Zmax = 12
  Zmin = 0
FEATURE [Part::Wedge] Wedge033  label="Klín033"
  AttacherType = Attacher::AttachEngine3D
  Placement = pos=(0,0,12) rot=(0,0,-1;1.5708rad)
  X2max = 0
  X2min = 0
  Xmax = 10
  Xmin = -10
  Ymax = 0
  Ymin = -32
  Z2max = 12
  Z2min = 0
  Zmax = 12
  Zmin = 0
FEATURE [Part::Wedge] Wedge034  label="Klín034"
  AttacherType = Attacher::AttachEngine3D
  Placement = pos=(0,0,12) rot=(0,0,1;3.14159rad)
  X2max = 0
  X2min = 0
  Xmax = 10
  Xmin = -10
  Ymax = 0
  Ymin = -32
  Z2max = 12
  Z2min = 0
  Zmax = 12
  Zmin = 0
FEATURE [Part::Wedge] Wedge035  label="Klín035"
  AttacherType = Attacher::AttachEngine3D
  Placement = pos=(0,0,12) rot=(0,0,1;1.5708rad)
  X2max = 0
  X2min = 0
  Xmax = 10
  Xmin = -10
  Ymax = 0
  Ymin = -32
  Z2max = 12
  Z2min = 0
  Zmax = 12
  Zmin = 0
FEATURE [Part::Cylinder] Cylinder1152  label="Válec1152"
  Angle = 360
  AttacherType = Attacher::AttachEngine3D
  Height = 20
  Placement = pos=(4.25,4.25,-88) rot=(0,0,1;3.14159rad)
  Radius = 1
FEATURE [Part::Cylinder] Cylinder1153  label="Válec1153"
  Angle = 360
  AttacherType = Attacher::AttachEngine3D
  Height = 4
  Placement = pos=(0,0,15) rot=(0,0,1;0rad)
  Radius = 8
FEATURE [Part::Cylinder] Cylinder1154  label="Válec1154"
  Angle = 360
  AttacherType = Attacher::AttachEngine3D
  Height = 20
  Placement = pos=(-4.25,4.25,-88) rot=(0,0,-1;1.5708rad)
  Radius = 1
FEATURE [Part::FeaturePython] Tube104  # WARN: FeaturePython — macro-defined, semantics opaque (R4)
  AttacherType = Attacher::AttachEngine3D
  Height = 10
  InnerRadius = 2.65
  OuterRadius = 8
  Placement = pos=(0,0,19) rot=(0,0,1;0rad)
FEATURE [Part::FeaturePython] wormgear068  # WARN: FeaturePython — macro-defined, semantics opaque (R4)
  AttacherType = Attacher::AttachEngine3D
  Placement = pos=(0,0,29) rot=(0,0,1;0.994838rad)
  beta = 41.9872
  clearance = 0.25
  diameter = 20
  head = 0.25
  height = 12
  module = 1.5
  pressure_angle = 20
  reverse_pitch = false
  teeth = 12
  version = 0.0.3
FEATURE [Part::FeaturePython] Tube105  # WARN: FeaturePython — macro-defined, semantics opaque (R4)
  AttacherType = Attacher::AttachEngine3D
  Height = 12
  InnerRadius = 4.1
  OuterRadius = 8
  Placement = pos=(0,0,12) rot=(0,0,1;0rad)
FEATURE [Part::Compound] Compound885
  Links = -> [Wedge032,Wedge035,Wedge034,Wedge033]
FEATURE [Part::Cylinder] Cylinder1155  label="Válec1155"
  Angle = 360
  AttacherType = Attacher::AttachEngine3D
  Height = 20
  Placement = pos=(4.25,-4.25,-88) rot=(0,0,1;1.5708rad)
  Radius = 1
FEATURE [Part::Cylinder] Cylinder1156  label="Válec1156"
  Angle = 360
  AttacherType = Attacher::AttachEngine3D
  Height = 20
  Placement = pos=(-4.25,4.25,-88) rot=(0,0,-1;1.5708rad)
  Radius = 1
FEATURE [Part::Cylinder] Cylinder1157  label="Válec1157"
  Angle = 360
  AttacherType = Attacher::AttachEngine3D
  Height = 2
  Placement = pos=(-4.25,-4.25,-88) rot=(0,0,1;0rad)
  Radius = 2
FEATURE [Part::Cylinder] Cylinder1158  label="Válec1158"
  Angle = 360
  AttacherType = Attacher::AttachEngine3D
  Height = 20
  Placement = pos=(-4.25,-4.25,-88) rot=(0,0,1;0rad)
  Radius = 1
FEATURE [Part::Cylinder] Cylinder1159  label="Válec1159"
  Angle = 360
  AttacherType = Attacher::AttachEngine3D
  Height = 2
  Placement = pos=(-4.25,4.25,-88) rot=(0,0,-1;1.5708rad)
  Radius = 2
FEATURE [Part::Cylinder] Cylinder1160  label="Válec1160"
  Angle = 360
  AttacherType = Attacher::AttachEngine3D
  Height = 2
  Placement = pos=(4.25,4.25,-88) rot=(0,0,1;3.14159rad)
  Radius = 2
FEATURE [Part::Cylinder] Cylinder1161  label="Válec1161"
  Angle = 360
  AttacherType = Attacher::AttachEngine3D
  Height = 20
  Placement = pos=(4.25,-4.25,-88) rot=(0,0,1;1.5708rad)
  Radius = 1
FEATURE [Part::Cylinder] Cylinder1162  label="Válec1162"
  Angle = 360
  AttacherType = Attacher::AttachEngine3D
  Height = 20
  Placement = pos=(4.25,-4.25,-88) rot=(0,0,1;1.5708rad)
  Radius = 1
FEATURE [Part::Cylinder] Cylinder1163  label="Válec1163"
  Angle = 360
  AttacherType = Attacher::AttachEngine3D
  Height = 2
  Placement = pos=(4.25,-4.25,-88) rot=(0,0,1;1.5708rad)
  Radius = 2
FEATURE [Part::Compound] Compound886
  Links = -> [Cylinder1157,Cylinder1163,Cylinder1160,Cylinder1159]
  Placement = pos=(0,0,91) rot=(0,0,1;0rad)
FEATURE [Part::Cylinder] Cylinder1164  label="Válec1164"
  Angle = 360
  AttacherType = Attacher::AttachEngine3D
  Height = 20
  Placement = pos=(4.25,4.25,-88) rot=(0,0,1;3.14159rad)
  Radius = 1
FEATURE [Part::Cylinder] Cylinder1165  label="Válec1165"
  Angle = 360
  AttacherType = Attacher::AttachEngine3D
  Height = 20
  Placement = pos=(-4.25,4.25,-88) rot=(0,0,-1;1.5708rad)
  Radius = 1
FEATURE [Part::Compound] Compound883
  Links = -> [Cylinder1158,Cylinder1162,Cylinder1164,Cylinder1165]
  Placement = pos=(0,0,91) rot=(0,0,1;0rad)
FEATURE [Part::Cut] Cut434
  Base = -> Tube104
  Tool = -> Compound883
FEATURE [Part::Cylinder] Cylinder1166  label="Válec1166"
  Angle = 360
  AttacherType = Attacher::AttachEngine3D
  Height = 20
  Placement = pos=(4.25,4.25,-88) rot=(0,0,1;3.14159rad)
  Radius = 1
FEATURE [Part::Cylinder] Cylinder1167  label="Válec1167"
  Angle = 360
  AttacherType = Attacher::AttachEngine3D
  Height = 20
  Placement = pos=(-4.25,-4.25,-88) rot=(0,0,1;0rad)
  Radius = 1
FEATURE [Part::Compound] Compound882
  Links = -> [Cylinder1167,Cylinder1155,Cylinder1152,Cylinder1154]
  Placement = pos=(0,0,91) rot=(0,0,1;0rad)
FEATURE [Part::Cylinder] Cylinder1168  label="Válec1168"
  Angle = 360
  AttacherType = Attacher::AttachEngine3D
  Height = 20
  Placement = pos=(-4.25,-4.25,-88) rot=(0,0,1;0rad)
  Radius = 1
FEATURE [Part::Cylinder] Cylinder1169  label="Válec1169"
  Angle = 360
  AttacherType = Attacher::AttachEngine3D
  Height = 60
  Placement = pos=(0,0,-10) rot=(0,0,1;0rad)
  Radius = 2.75
FEATURE [Part::Cut] Cut436
  Base = -> wormgear068
  Tool = -> Cylinder1169
FEATURE [Part::Cut] Cut439
  Base = -> Tube105
  Placement = pos=(0,0,-9) rot=(0,0,1;0rad)
  Tool = -> Compound885
FEATURE [Part::Chamfer] Chamfer030
  Base = -> Cut439
  Edges = 8 edges r=1: [Edge7,Edge8,Edge21,Edge22,Edge31,Edge32,Edge45,Edge46]
FEATURE [Part::Cut] Cut438
  Base = -> Chamfer030
  Tool = -> Compound886
FEATURE [Part::Cut] Cut437
  Base = -> Cut438
  Tool = -> Compound882
FEATURE [Part::Compound] Compound887
  Links = -> [Cylinder1168,Cylinder1161,Cylinder1166,Cylinder1156]
  Placement = pos=(0,0,91) rot=(0,0,1;0rad)
FEATURE [Part::Cut] Cut435
  Base = -> Cylinder1153
  Tool = -> Compound887
FEATURE [Part::Compound] Compound884  label="J-midi_inner-planeo-m1.5-reinforced_v4"
  Links = -> [Cut436,Cut437,Cut435,Cut434]
  Placement = pos=(0,0,8) rot=(0,0,1;0.10472rad)
FEATURE [Part::Cylinder] Cylinder1170  label="Válec1170"
  Angle = 360
  AttacherType = Attacher::AttachEngine3D
  Height = 20
  Placement = pos=(4,4,-88) rot=(0,0,1;3.14159rad)
  Radius = 1
FEATURE [Part::Cylinder] Cylinder1171  label="Válec1171"
  Angle = 360
  AttacherType = Attacher::AttachEngine3D
  Height = 4
  Placement = pos=(0,0,15) rot=(0,0,1;0rad)
  Radius = 7.5
FEATURE [Part::Cylinder] Cylinder1172  label="Válec1172"
  Angle = 360
  AttacherType = Attacher::AttachEngine3D
  Height = 20
  Placement = pos=(-4,4,-88) rot=(0,0,-1;1.5708rad)
  Radius = 1
FEATURE [Part::Cylinder] Cylinder1173  label="Válec1173"
  Angle = 360
  AttacherType = Attacher::AttachEngine3D
  Height = 20
  Placement = pos=(4,-4,-88) rot=(0,0,1;1.5708rad)
  Radius = 1
FEATURE [Part::Cylinder] Cylinder1174  label="Válec1174"
  Angle = 360
  AttacherType = Attacher::AttachEngine3D
  Height = 20
  Placement = pos=(-4,4,-88) rot=(0,0,-1;1.5708rad)
  Radius = 1
FEATURE [Part::Cylinder] Cylinder1175  label="Válec1175"
  Angle = 360
  AttacherType = Attacher::AttachEngine3D
  Height = 2
  Placement = pos=(-4,-4,-88) rot=(0,0,1;0rad)
  Radius = 2
FEATURE [Part::Cylinder] Cylinder1176  label="Válec1176"
  Angle = 360
  AttacherType = Attacher::AttachEngine3D
  Height = 20
  Placement = pos=(-4,-4,-88) rot=(0,0,1;0rad)
  Radius = 1
FEATURE [Part::Cylinder] Cylinder1177  label="Válec1177"
  Angle = 360
  AttacherType = Attacher::AttachEngine3D
  Height = 2
  Placement = pos=(-4,4,-88) rot=(0,0,-1;1.5708rad)
  Radius = 2
FEATURE [Part::Cylinder] Cylinder1178  label="Válec1178"
  Angle = 360
  AttacherType = Attacher::AttachEngine3D
  Height = 2
  Placement = pos=(4,4,-88) rot=(0,0,1;3.14159rad)
  Radius = 2
FEATURE [Part::Cylinder] Cylinder1179  label="Válec1179"
  Angle = 360
  AttacherType = Attacher::AttachEngine3D
  Height = 20
  Placement = pos=(4,-4,-88) rot=(0,0,1;1.5708rad)
  Radius = 1
FEATURE [Part::Cylinder] Cylinder1180  label="Válec1180"
  Angle = 360
  AttacherType = Attacher::AttachEngine3D
  Height = 20
  Placement = pos=(4,-4,-88) rot=(0,0,1;1.5708rad)
  Radius = 1
FEATURE [Part::Cylinder] Cylinder1181  label="Válec1181"
  Angle = 360
  AttacherType = Attacher::AttachEngine3D
  Height = 2
  Placement = pos=(4,-4,-88) rot=(0,0,1;1.5708rad)
  Radius = 2
FEATURE [Part::Cylinder] Cylinder1182  label="Válec1182"
  Angle = 360
  AttacherType = Attacher::AttachEngine3D
  Height = 20
  Placement = pos=(4,4,-88) rot=(0,0,1;3.14159rad)
  Radius = 1
FEATURE [Part::Cylinder] Cylinder1183  label="Válec1183"
  Angle = 360
  AttacherType = Attacher::AttachEngine3D
  Height = 20
  Placement = pos=(-4,4,-88) rot=(0,0,-1;1.5708rad)
  Radius = 1
FEATURE [Part::Compound] Compound889
  Links = -> [Cylinder1176,Cylinder1180,Cylinder1182,Cylinder1183]
  Placement = pos=(0,0,91) rot=(0,0,1;0rad)
FEATURE [Part::Compound] Compound892
  Links = -> [Cylinder1175,Cylinder1181,Cylinder1178,Cylinder1177]
  Placement = pos=(0,0,91) rot=(0,0,1;0rad)
FEATURE [Part::Wedge] Wedge036  label="Klín036"
  AttacherType = Attacher::AttachEngine3D
  Placement = pos=(0,0,12) rot=(0,0,1;1.5708rad)
  X2max = 0
  X2min = 0
  Xmax = 10
  Xmin = -10
  Ymax = 0
  Ymin = -32
  Z2max = 12
  Z2min = 0
  Zmax = 12
  Zmin = 0
FEATURE [Part::Wedge] Wedge037  label="Klín037"
  AttacherType = Attacher::AttachEngine3D
  Placement = pos=(0,0,12) rot=(0,0,-1;1.5708rad)
  X2max = 0
  X2min = 0
  Xmax = 10
  Xmin = -10
  Ymax = 0
  Ymin = -32
  Z2max = 12
  Z2min = 0
  Zmax = 12
  Zmin = 0
FEATURE [Part::Wedge] Wedge038  label="Klín038"
  AttacherType = Attacher::AttachEngine3D
  Placement = pos=(0,0,12) rot=(0,0,1;0rad)
  X2max = 0
  X2min = 0
  Xmax = 10
  Xmin = -10
  Ymax = 0
  Ymin = -32
  Z2max = 12
  Z2min = 0
  Zmax = 12
  Zmin = 0
FEATURE [Part::Wedge] Wedge039  label="Klín039"
  AttacherType = Attacher::AttachEngine3D
  Placement = pos=(0,0,12) rot=(0,0,1;3.14159rad)
  X2max = 0
  X2min = 0
  Xmax = 10
  Xmin = -10
  Ymax = 0
  Ymin = -32
  Z2max = 12
  Z2min = 0
  Zmax = 12
  Zmin = 0
FEATURE [Part::Compound] Compound891
  Links = -> [Wedge038,Wedge036,Wedge039,Wedge037]
FEATURE [Part::FeaturePython] Tube106  # WARN: FeaturePython — macro-defined, semantics opaque (R4)
  AttacherType = Attacher::AttachEngine3D
  Height = 10
  InnerRadius = 2.75
  OuterRadius = 7.5
  Placement = pos=(0,0,19) rot=(0,0,1;0rad)
FEATURE [Part::Cut] Cut440
  Base = -> Tube106
  Tool = -> Compound889
FEATURE [Part::FeaturePython] wormgear069  # WARN: FeaturePython — macro-defined, semantics opaque (R4)
  AttacherType = Attacher::AttachEngine3D
  Placement = pos=(0,0,29) rot=(0,0,1;0.994838rad)
  beta = 40.6013
  clearance = 0.25
  diameter = 21
  head = 0.25
  height = 12
  module = 1.5
  pressure_angle = 20
  reverse_pitch = false
  teeth = 12
  version = 0.0.3
FEATURE [Part::FeaturePython] Tube107  # WARN: FeaturePython — macro-defined, semantics opaque (R4)
  AttacherType = Attacher::AttachEngine3D
  Height = 12
  InnerRadius = 3.75
  OuterRadius = 7.5
  Placement = pos=(0,0,12) rot=(0,0,1;0rad)
FEATURE [Part::Cylinder] Cylinder1184  label="Válec1184"
  Angle = 360
  AttacherType = Attacher::AttachEngine3D
  Height = 20
  Placement = pos=(4,4,-88) rot=(0,0,1;3.14159rad)
  Radius = 1
FEATURE [Part::Cylinder] Cylinder1185  label="Válec1185"
  Angle = 360
  AttacherType = Attacher::AttachEngine3D
  Height = 20
  Placement = pos=(-4,-4,-88) rot=(0,0,1;0rad)
  Radius = 1
FEATURE [Part::Compound] Compound888
  Links = -> [Cylinder1185,Cylinder1173,Cylinder1170,Cylinder1172]
  Placement = pos=(0,0,91) rot=(0,0,1;0rad)
FEATURE [Part::Cylinder] Cylinder1186  label="Válec1186"
  Angle = 360
  AttacherType = Attacher::AttachEngine3D
  Height = 20
  Placement = pos=(-4,-4,-88) rot=(0,0,1;0rad)
  Radius = 1
FEATURE [Part::Compound] Compound893
  Links = -> [Cylinder1186,Cylinder1179,Cylinder1184,Cylinder1174]
  Placement = pos=(0,0,91) rot=(0,0,1;0rad)
FEATURE [Part::Cut] Cut441
  Base = -> Cylinder1171
  Tool = -> Compound893
FEATURE [Part::Cylinder] Cylinder1187  label="Válec1187"
  Angle = 360
  AttacherType = Attacher::AttachEngine3D
  Height = 60
  Placement = pos=(0,0,-10) rot=(0,0,1;0rad)
  Radius = 2.75
FEATURE [Part::Cut] Cut442
  Base = -> wormgear069
  Tool = -> Cylinder1187
FEATURE [Part::Cut] Cut445
  Base = -> Tube107
  Placement = pos=(0,0,-9) rot=(0,0,1;0rad)
  Tool = -> Compound891
FEATURE [Part::Chamfer] Chamfer031
  Base = -> Cut445
  Edges = 8 edges r=1: [Edge7,Edge8,Edge21,Edge22,Edge31,Edge32,Edge45,Edge46]
FEATURE [Part::Cut] Cut444
  Base = -> Chamfer031
  Tool = -> Compound892
FEATURE [Part::Cut] Cut443
  Base = -> Cut444
  Tool = -> Compound888
FEATURE [Part::Compound] Compound890  label="J-midi_inner-planeo-m1.5-reinforced_v5"
  Links = -> [Cut442,Cut443,Cut441,Cut440]
  Placement = pos=(0,0,8) rot=(0,0,1;0.10472rad)
FEATURE [Part::FeaturePython] Tube108  label="ZKL-6002"  # WARN: FeaturePython — macro-defined, semantics opaque (R4)
  AttacherType = Attacher::AttachEngine3D
  Height = 9
  InnerRadius = 7.5
  OuterRadius = 16
  Placement = pos=(0,0,-42) rot=(0,0,1;0rad)
FEATURE [Part::FeaturePython] Tube109  label="ZKL-16006"  # WARN: FeaturePython — macro-defined, semantics opaque (R4)
  AttacherType = Attacher::AttachEngine3D
  Height = 9
  InnerRadius = 15
  OuterRadius = 27.5
  Placement = pos=(0,0,-64) rot=(0,0,1;0rad)
FEATURE [Part::Box] Box448  label="Krychle448"
  AttacherType = Attacher::AttachEngine3D
  Height = 2
  Length = 8
  Placement = pos=(-30.4056,34.6482,23) rot=(0,0,1;2.35619rad)
  Width = 6
FEATURE [Part::Box] Box449  label="Krychle449"
  AttacherType = Attacher::AttachEngine3D
  Height = 2
  Length = 8
  Placement = pos=(3,46,23) rot=(0,0,1;1.5708rad)
  Width = 6
FEATURE [Part::Box] Box450  label="Krychle450"
  AttacherType = Attacher::AttachEngine3D
  Height = 2
  Length = 8
  Placement = pos=(-46,3,23) rot=(0,0,1;3.14159rad)
  Width = 6
FEATURE [Part::Cylinder] Cylinder399  label="Válec399"
  Angle = 360
  AttacherType = Attacher::AttachEngine3D
  Height = 50
  Placement = pos=(50,0,-15) rot=(0,0,1;0rad)
  Radius = 1.5
FEATURE [Part::Box] Box451  label="Krychle451"
  AttacherType = Attacher::AttachEngine3D
  Height = 2
  Length = 8
  Placement = pos=(46,-3,23) rot=(0,0,1;0rad)
  Width = 6
FEATURE [Part::Box] Box185  label="Krychle185"
  AttacherType = Attacher::AttachEngine3D
  Height = 2
  Length = 8
  Placement = pos=(34.6482,30.4056,23) rot=(0,0,1;0.785398rad)
  Width = 6
FEATURE [Part::Cylinder] Cylinder400  label="Válec400"
  Angle = 360
  AttacherType = Attacher::AttachEngine3D
  Height = 50
  Placement = pos=(35.3553,35.3553,-15) rot=(0,0,1;0.785398rad)
  Radius = 1.5
FEATURE [Part::Cylinder] Cylinder401  label="Válec401"
  Angle = 360
  AttacherType = Attacher::AttachEngine3D
  Height = 50
  Placement = pos=(-7e-15,50,-15) rot=(0,0,1;1.5708rad)
  Radius = 1.5
FEATURE [Part::Box] Box186  label="Krychle186"
  AttacherType = Attacher::AttachEngine3D
  Height = 2
  Length = 8
  Placement = pos=(-34.6482,-30.4056,23) rot=(0,0,1;3.92699rad)
  Width = 6
FEATURE [Part::Box] Box187  label="Krychle187"
  AttacherType = Attacher::AttachEngine3D
  Height = 2
  Length = 8
  Placement = pos=(-3,-46,23) rot=(0,0,-1;1.5708rad)
  Width = 6
FEATURE [Part::Box] Box188  label="Krychle188"
  AttacherType = Attacher::AttachEngine3D
  Height = 2
  Length = 8
  Placement = pos=(30.4056,-34.6482,23) rot=(0,0,-1;0.785398rad)
  Width = 6
FEATURE [Part::Cylinder] Cylinder402  label="Válec402"
  Angle = 360
  AttacherType = Attacher::AttachEngine3D
  Height = 50
  Placement = pos=(-35.3553,35.3553,-15) rot=(0,0,1;2.35619rad)
  Radius = 1.5
FEATURE [Part::Cylinder] Cylinder403  label="Válec403"
  Angle = 360
  AttacherType = Attacher::AttachEngine3D
  Height = 50
  Placement = pos=(-50,-2.3e-14,-15) rot=(0,0,1;3.14159rad)
  Radius = 1.5
FEATURE [Part::Cylinder] Cylinder404  label="Válec404"
  Angle = 360
  AttacherType = Attacher::AttachEngine3D
  Height = 50
  Placement = pos=(-35.3553,-35.3553,-15) rot=(0,0,1;3.92699rad)
  Radius = 1.5
FEATURE [Part::Cylinder] Cylinder405  label="Válec405"
  Angle = 360
  AttacherType = Attacher::AttachEngine3D
  Height = 50
  Placement = pos=(2.5e-14,-50,-15) rot=(0,0,-1;1.5708rad)
  Radius = 1.5
FEATURE [Part::Cylinder] Cylinder406  label="Válec406"
  Angle = 360
  AttacherType = Attacher::AttachEngine3D
  Height = 50
  Placement = pos=(35.3553,-35.3553,-15) rot=(0,0,-1;0.785398rad)
  Radius = 1.5
FEATURE [Part::Box] Box189  label="Krychle189"
  AttacherType = Attacher::AttachEngine3D
  Height = 6
  Length = 2
  Placement = pos=(32,48,24) rot=(0,0,1;0rad)
  Width = 6
FEATURE [Part::Box] Box190  label="Krychle190"
  AttacherType = Attacher::AttachEngine3D
  Height = 6
  Length = 2
  Placement = pos=(32,-54,24) rot=(0,0,1;0rad)
  Width = 6
FEATURE [Part::Box] Box191  label="Krychle191"
  AttacherType = Attacher::AttachEngine3D
  Height = 6
  Length = 2
  Placement = pos=(38,33,39) rot=(0,0,1;0rad)
  Width = 6
FEATURE [Part::Box] Box192  label="Krychle192"
  AttacherType = Attacher::AttachEngine3D
  Height = 6
  Length = 2
  Placement = pos=(38,-39,39) rot=(0,0,1;0rad)
  Width = 6
FEATURE [Part::Cylinder] Cylinder407  label="Válec407"
  Angle = 360
  AttacherType = Attacher::AttachEngine3D
  Height = 100
  Placement = pos=(34,-36,42) rot=(0,1,0;1.5708rad)
  Radius = 1.5
FEATURE [Part::Cylinder] Cylinder408  label="Válec408"
  Angle = 360
  AttacherType = Attacher::AttachEngine3D
  Height = 100
  Placement = pos=(24,51,27) rot=(0,1,0;1.5708rad)
  Radius = 1.5
FEATURE [Part::Cylinder] Cylinder409  label="Válec409"
  Angle = 360
  AttacherType = Attacher::AttachEngine3D
  Height = 100
  Placement = pos=(24,-51,27) rot=(0,1,0;1.5708rad)
  Radius = 1.5
FEATURE [Part::Cylinder] Cylinder410  label="Válec410"
  Angle = 360
  AttacherType = Attacher::AttachEngine3D
  Height = 100
  Placement = pos=(34,36,42) rot=(0,1,0;1.5708rad)
  Radius = 1.5
FEATURE [Part::FeaturePython] Tube003  # WARN: FeaturePython — macro-defined, semantics opaque (R4)
  AttacherType = Attacher::AttachEngine3D
  Height = 5
  InnerRadius = 46.4
  OuterRadius = 47
  Placement = pos=(0,0,40) rot=(0,0,1;0rad)
FEATURE [Part::FeaturePython] Tube110  # WARN: FeaturePython — macro-defined, semantics opaque (R4)
  AttacherType = Attacher::AttachEngine3D
  Height = 25
  InnerRadius = 47
  OuterRadius = 54
  Placement = pos=(0,0,20) rot=(0,0,1;0rad)
FEATURE [Part::Compound] Compound894
  Links = -> [Cylinder408,Cylinder409,Cylinder410,Cylinder407]
FEATURE [Part::Compound] Compound730
  Links = -> [Box451,Box185,Box449,Box448,Box450,Box186,Box187,Box188]
  Placement = pos=(0,0,1) rot=(0,0,1;0rad)
FEATURE [Part::Compound] Compound731
  Links = -> [Box189,Box190,Box191,Box192]
FEATURE [Part::Compound] Compound732
  Links = -> [Cylinder399,Cylinder400,Cylinder401,Cylinder402,Cylinder403,Cylinder404,Cylinder405,Cylinder406]
  Placement = pos=(0,0,-5) rot=(0,0,1;0rad)
FEATURE [Part::Cut] Cut447
  Base = -> Tube110
  Tool = -> Compound732
FEATURE [Part::Cut] Cut446
  Base = -> Cut447
  Tool = -> Compound730
FEATURE [Part::Box] Box452  label="Krychle452"
  AttacherType = Attacher::AttachEngine3D
  Height = 25
  Length = 46
  Placement = pos=(0,-54,20) rot=(0,0,1;0rad)
  Width = 108
FEATURE [Part::Cylinder] Cylinder1188  label="Válec1188"
  Angle = 360
  AttacherType = Attacher::AttachEngine3D
  Height = 25
  Placement = pos=(0,0,20) rot=(0,0,1;0rad)
  Radius = 47
FEATURE [Part::Cylinder] Cylinder1189  label="Válec1189"
  Angle = 360
  AttacherType = Attacher::AttachEngine3D
  Height = 50
  Placement = pos=(50,0,-15) rot=(0,0,1;0rad)
  Radius = 1.5
FEATURE [Part::Cylinder] Cylinder1190  label="Válec1190"
  Angle = 360
  AttacherType = Attacher::AttachEngine3D
  Height = 50
  Placement = pos=(35.3553,35.3553,-15) rot=(0,0,1;0.785398rad)
  Radius = 1.5
FEATURE [Part::Cylinder] Cylinder1191  label="Válec1191"
  Angle = 360
  AttacherType = Attacher::AttachEngine3D
  Height = 50
  Placement = pos=(-7e-15,50,-15) rot=(0,0,1;1.5708rad)
  Radius = 1.5
FEATURE [Part::Cylinder] Cylinder1192  label="Válec1192"
  Angle = 360
  AttacherType = Attacher::AttachEngine3D
  Height = 50
  Placement = pos=(-35.3553,35.3553,-15) rot=(0,0,1;2.35619rad)
  Radius = 1.5
FEATURE [Part::Cylinder] Cylinder1193  label="Válec1193"
  Angle = 360
  AttacherType = Attacher::AttachEngine3D
  Height = 50
  Placement = pos=(-50,-2.3e-14,-15) rot=(0,0,1;3.14159rad)
  Radius = 1.5
FEATURE [Part::Cylinder] Cylinder1194  label="Válec1194"
  Angle = 360
  AttacherType = Attacher::AttachEngine3D
  Height = 50
  Placement = pos=(-35.3553,-35.3553,-15) rot=(0,0,1;3.92699rad)
  Radius = 1.5
FEATURE [Part::Cylinder] Cylinder1195  label="Válec1195"
  Angle = 360
  AttacherType = Attacher::AttachEngine3D
  Height = 50
  Placement = pos=(2.5e-14,-50,-15) rot=(0,0,-1;1.5708rad)
  Radius = 1.5
FEATURE [Part::Cylinder] Cylinder1196  label="Válec1196"
  Angle = 360
  AttacherType = Attacher::AttachEngine3D
  Height = 50
  Placement = pos=(35.3553,-35.3553,-15) rot=(0,0,-1;0.785398rad)
  Radius = 1.5
FEATURE [Part::Box] Box453  label="Krychle453"
  AttacherType = Attacher::AttachEngine3D
  Height = 2
  Length = 8
  Placement = pos=(3,46,23) rot=(0,0,1;1.5708rad)
  Width = 6
FEATURE [Part::Box] Box454  label="Krychle454"
  AttacherType = Attacher::AttachEngine3D
  Height = 2
  Length = 8
  Placement = pos=(-30.4056,34.6482,23) rot=(0,0,1;2.35619rad)
  Width = 6
FEATURE [Part::Box] Box455  label="Krychle455"
  AttacherType = Attacher::AttachEngine3D
  Height = 2
  Length = 8
  Placement = pos=(46,-3,23) rot=(0,0,1;0rad)
  Width = 6
FEATURE [Part::Box] Box456  label="Krychle456"
  AttacherType = Attacher::AttachEngine3D
  Height = 2
  Length = 8
  Placement = pos=(-46,3,23) rot=(0,0,1;3.14159rad)
  Width = 6
FEATURE [Part::Box] Box457  label="Krychle457"
  AttacherType = Attacher::AttachEngine3D
  Height = 2
  Length = 8
  Placement = pos=(-34.6482,-30.4056,23) rot=(0,0,1;3.92699rad)
  Width = 6
FEATURE [Part::Box] Box458  label="Krychle458"
  AttacherType = Attacher::AttachEngine3D
  Height = 2
  Length = 8
  Placement = pos=(30.4056,-34.6482,23) rot=(0,0,-1;0.785398rad)
  Width = 6
FEATURE [Part::Box] Box459  label="Krychle459"
  AttacherType = Attacher::AttachEngine3D
  Height = 2
  Length = 8
  Placement = pos=(34.6482,30.4056,23) rot=(0,0,1;0.785398rad)
  Width = 6
FEATURE [Part::Box] Box460  label="Krychle460"
  AttacherType = Attacher::AttachEngine3D
  Height = 2
  Length = 8
  Placement = pos=(-3,-46,23) rot=(0,0,-1;1.5708rad)
  Width = 6
FEATURE [Part::Cylinder] Cylinder1197  label="Válec1197"
  Angle = 360
  AttacherType = Attacher::AttachEngine3D
  Height = 100
  Placement = pos=(24,51,27) rot=(0,1,0;1.5708rad)
  Radius = 1.5
FEATURE [Part::Cylinder] Cylinder1198  label="Válec1198"
  Angle = 360
  AttacherType = Attacher::AttachEngine3D
  Height = 100
  Placement = pos=(24,-51,26) rot=(0,1,0;1.5708rad)
  Radius = 1.5
FEATURE [Part::Cylinder] Cylinder1199  label="Válec1199"
  Angle = 360
  AttacherType = Attacher::AttachEngine3D
  Height = 100
  Placement = pos=(34,36,42) rot=(0,1,0;1.5708rad)
  Radius = 1.5
FEATURE [Part::Cylinder] Cylinder1200  label="Válec1200"
  Angle = 360
  AttacherType = Attacher::AttachEngine3D
  Height = 100
  Placement = pos=(34,-36,42) rot=(0,1,0;1.5708rad)
  Radius = 1.5
FEATURE [Part::Box] Box461  label="Krychle461"
  AttacherType = Attacher::AttachEngine3D
  Height = 6
  Length = 2
  Placement = pos=(36,48,24) rot=(0,0,1;0rad)
  Width = 6
FEATURE [Part::Box] Box462  label="Krychle462"
  AttacherType = Attacher::AttachEngine3D
  Height = 6
  Length = 2
  Placement = pos=(36,-54,24) rot=(0,0,1;0rad)
  Width = 6
FEATURE [Part::Box] Box463  label="Krychle463"
  AttacherType = Attacher::AttachEngine3D
  Height = 6
  Length = 2
  Placement = pos=(38,33,39) rot=(0,0,1;0rad)
  Width = 6
FEATURE [Part::Box] Box464  label="Krychle464"
  AttacherType = Attacher::AttachEngine3D
  Height = 6
  Length = 2
  Placement = pos=(38,-39,39) rot=(0,0,1;0rad)
  Width = 6
FEATURE [Part::Compound] Compound895
  Links = -> [Box461,Box462,Box463,Box464]
FEATURE [Part::Compound] Compound896
  Links = -> [Cylinder1197,Cylinder1198,Cylinder1199,Cylinder1200]
FEATURE [Part::Compound] Compound897
  Links = -> [Box455,Box459,Box453,Box454,Box456,Box457,Box460,Box458]
  Placement = pos=(0,0,1) rot=(0,0,1;0rad)
FEATURE [Part::Compound] Compound898
  Links = -> [Cylinder1189,Cylinder1190,Cylinder1191,Cylinder1192,Cylinder1193,Cylinder1194,Cylinder1195,Cylinder1196]
  Placement = pos=(0,0,-5) rot=(0,0,1;0rad)
FEATURE [Part::Cut] Cut448
  Base = -> Cut446
  Tool = -> Compound731
FEATURE [Part::Cut] Cut449
  Base = -> Cut448
  Tool = -> Compound894
FEATURE [Part::Cut] Cut452
  Base = -> Box452
  Tool = -> Cylinder1188
FEATURE [Part::Cut] Cut451
  Base = -> Cut452
  Tool = -> Compound895
FEATURE [Part::Cut] Cut453
  Base = -> Cut451
  Tool = -> Compound898
FEATURE [Part::Cut] Cut454
  Base = -> Cut453
  Tool = -> Compound897
FEATURE [Part::Cut] Cut450
  Base = -> Cut454
  Tool = -> Compound896
FEATURE [Part::Compound] Compound899  label="J-midi-deep_slip-ring"
  Links = -> [Cut449,Cut450,Tube003]
FEATURE [Part::Box] Box485  label="Krychle485"
  AttacherType = Attacher::AttachEngine3D
  Height = 2
  Length = 6
  Placement = pos=(-30.4056,34.6482,33) rot=(0,0,1;3.92699rad)
  Width = 8
FEATURE [Part::Box] Box486  label="Krychle486"
  AttacherType = Attacher::AttachEngine3D
  Height = 2
  Length = 6
  Placement = pos=(-3,-46,33) rot=(0,0,1;0rad)
  Width = 8
FEATURE [Part::Box] Box487  label="Krychle487"
  AttacherType = Attacher::AttachEngine3D
  Height = 2
  Length = 6
  Placement = pos=(46,-3,33) rot=(0,0,1;1.5708rad)
  Width = 8
FEATURE [Part::Cylinder] Cylinder1201  label="Válec1201"
  Angle = 360
  AttacherType = Attacher::AttachEngine3D
  Height = 32
  Placement = pos=(-29.6985,29.6985,33.5) rot=(0,0,1;3.92699rad)
  Radius = 1.5
FEATURE [Part::Box] Box488  label="Krychle488"
  AttacherType = Attacher::AttachEngine3D
  Height = 2
  Length = 6
  Placement = pos=(-46,3,33) rot=(0,0,-1;1.5708rad)
  Width = 8
FEATURE [Part::Box] Box489  label="Krychle489"
  AttacherType = Attacher::AttachEngine3D
  Height = 2
  Length = 6
  Placement = pos=(30.4056,-34.6482,33) rot=(0,0,1;0.785398rad)
  Width = 8
FEATURE [Part::Cylinder] Cylinder1202  label="Válec1202"
  Angle = 360
  AttacherType = Attacher::AttachEngine3D
  Height = 32
  Placement = pos=(-42,-2.4e-14,33.5) rot=(0,0,-1;1.5708rad)
  Radius = 1.5
FEATURE [Part::Box] Box490  label="Krychle490"
  AttacherType = Attacher::AttachEngine3D
  Height = 2
  Length = 6
  Placement = pos=(3,46,33) rot=(0,0,1;3.14159rad)
  Width = 8
FEATURE [Part::Cylinder] Cylinder1203  label="Válec1203"
  Angle = 360
  AttacherType = Attacher::AttachEngine3D
  Height = 32
  Placement = pos=(29.6985,29.6985,33.5) rot=(0,0,1;2.35619rad)
  Radius = 1.5
FEATURE [Part::Box] Box491  label="Krychle491"
  AttacherType = Attacher::AttachEngine3D
  Height = 2
  Length = 6
  Placement = pos=(34.6482,30.4056,33) rot=(0,0,1;2.35619rad)
  Width = 8
FEATURE [Part::Cylinder] Cylinder1204  label="Válec1204"
  Angle = 360
  AttacherType = Attacher::AttachEngine3D
  Height = 32
  Placement = pos=(42,6e-15,33.5) rot=(0,0,1;1.5708rad)
  Radius = 1.5
FEATURE [Part::Cylinder] Cylinder1205  label="Válec1205"
  Angle = 360
  AttacherType = Attacher::AttachEngine3D
  Height = 32
  Placement = pos=(29.6985,-29.6985,33.5) rot=(0,0,1;0.785398rad)
  Radius = 1.5
FEATURE [Part::Cylinder] Cylinder1206  label="Válec1206"
  Angle = 360
  AttacherType = Attacher::AttachEngine3D
  Height = 32
  Placement = pos=(-29.6985,-29.6985,33.5) rot=(0,0,-1;0.785398rad)
  Radius = 1.5
FEATURE [Part::Box] Box492  label="Krychle492"
  AttacherType = Attacher::AttachEngine3D
  Height = 2
  Length = 6
  Placement = pos=(-34.6482,-30.4056,33) rot=(0,0,-1;0.785398rad)
  Width = 8
FEATURE [Part::Cylinder] Cylinder1207  label="Válec1207"
  Angle = 360
  AttacherType = Attacher::AttachEngine3D
  Height = 32
  Placement = pos=(0,-42,33.5) rot=(0,0,1;0rad)
  Radius = 1.5
FEATURE [Part::Cylinder] Cylinder1208  label="Válec1208"
  Angle = 360
  AttacherType = Attacher::AttachEngine3D
  Height = 32
  Placement = pos=(-1.4e-14,42,33.5) rot=(0,0,1;3.14159rad)
  Radius = 1.5
FEATURE [Part::Cylinder] Cylinder1209  label="Válec1209"
  Angle = 360
  AttacherType = Attacher::AttachEngine3D
  Height = 12
  Placement = pos=(-29.6985,29.6985,33.5) rot=(0,0,1;3.92699rad)
  Radius = 1.5
FEATURE [Part::Cylinder] Cylinder1210  label="Válec1210"
  Angle = 360
  AttacherType = Attacher::AttachEngine3D
  Height = 12
  Placement = pos=(42,6e-15,33.5) rot=(0,0,1;1.5708rad)
  Radius = 1.5
FEATURE [Part::Cylinder] Cylinder1211  label="Válec1211"
  Angle = 360
  AttacherType = Attacher::AttachEngine3D
  Height = 12
  Placement = pos=(29.6985,29.6985,33.5) rot=(0,0,1;2.35619rad)
  Radius = 1.5
FEATURE [Part::Cylinder] Cylinder1212  label="Válec1212"
  Angle = 360
  AttacherType = Attacher::AttachEngine3D
  Height = 12
  Placement = pos=(-29.6985,-29.6985,33.5) rot=(0,0,-1;0.785398rad)
  Radius = 1.5
FEATURE [Part::Cylinder] Cylinder1213  label="Válec1213"
  Angle = 360
  AttacherType = Attacher::AttachEngine3D
  Height = 12
  Placement = pos=(29.6985,-29.6985,33.5) rot=(0,0,1;0.785398rad)
  Radius = 1.5
FEATURE [Part::Cylinder] Cylinder1214  label="Válec1214"
  Angle = 360
  AttacherType = Attacher::AttachEngine3D
  Height = 12
  Placement = pos=(0,-42,33.5) rot=(0,0,1;0rad)
  Radius = 1.5
FEATURE [Part::Cylinder] Cylinder1215  label="Válec1215"
  Angle = 360
  AttacherType = Attacher::AttachEngine3D
  Height = 12
  Placement = pos=(-42,-2.4e-14,33.5) rot=(0,0,-1;1.5708rad)
  Radius = 1.5
FEATURE [Part::Cylinder] Cylinder1216  label="Válec1216"
  Angle = 360
  AttacherType = Attacher::AttachEngine3D
  Height = 12
  Placement = pos=(-1.4e-14,42,33.5) rot=(0,0,1;3.14159rad)
  Radius = 1.5
FEATURE [Part::Box] Box501  label="Krychle501"
  AttacherType = Attacher::AttachEngine3D
  Height = 2
  Length = 6
  Placement = pos=(30.4056,-34.6482,33) rot=(0,0,1;0.785398rad)
  Width = 8
FEATURE [Part::Box] Box502  label="Krychle502"
  AttacherType = Attacher::AttachEngine3D
  Height = 2
  Length = 6
  Placement = pos=(3,46,33) rot=(0,0,1;3.14159rad)
  Width = 8
FEATURE [Part::Cylinder] Cylinder1217  label="Válec1217"
  Angle = 360
  AttacherType = Attacher::AttachEngine3D
  Height = 12
  Radius = 40
FEATURE [Part::Cylinder] Cylinder1218  label="Válec1218"
  Angle = 360
  AttacherType = Attacher::AttachEngine3D
  Height = 12
  Radius = 40
FEATURE [Part::Box] Box503  label="Krychle503"
  AttacherType = Attacher::AttachEngine3D
  Height = 2
  Length = 6
  Placement = pos=(-46,3,33) rot=(0,0,-1;1.5708rad)
  Width = 8
FEATURE [Part::Box] Box504  label="Krychle504"
  AttacherType = Attacher::AttachEngine3D
  Height = 2
  Length = 6
  Placement = pos=(-3,-46,33) rot=(0,0,1;0rad)
  Width = 8
FEATURE [Part::Box] Box505  label="Krychle505"
  AttacherType = Attacher::AttachEngine3D
  Height = 2
  Length = 6
  Placement = pos=(-34.6482,-30.4056,33) rot=(0,0,-1;0.785398rad)
  Width = 8
FEATURE [Part::Box] Box506  label="Krychle506"
  AttacherType = Attacher::AttachEngine3D
  Height = 2
  Length = 6
  Placement = pos=(46,-3,33) rot=(0,0,1;1.5708rad)
  Width = 8
FEATURE [Part::Box] Box507  label="Krychle507"
  AttacherType = Attacher::AttachEngine3D
  Height = 2
  Length = 6
  Placement = pos=(34.6482,30.4056,33) rot=(0,0,1;2.35619rad)
  Width = 8
FEATURE [Part::Box] Box508  label="Krychle508"
  AttacherType = Attacher::AttachEngine3D
  Height = 2
  Length = 6
  Placement = pos=(-30.4056,34.6482,33) rot=(0,0,1;3.92699rad)
  Width = 8
FEATURE [Part::FeaturePython] Tube111  # WARN: FeaturePython — macro-defined, semantics opaque (R4)
  AttacherType = Attacher::AttachEngine3D
  Height = 24
  InnerRadius = 40
  OuterRadius = 46
  Placement = pos=(0,0,21) rot=(0,0,1;0rad)
FEATURE [Part::FeaturePython] Tube112  # WARN: FeaturePython — macro-defined, semantics opaque (R4)
  AttacherType = Attacher::AttachEngine3D
  Height = 1
  InnerRadius = 36
  OuterRadius = 46
  Placement = pos=(0,0,45) rot=(0,0,1;0rad)
FEATURE [Part::Compound] Compound900
  Links = -> [Cylinder1207,Cylinder1205,Cylinder1204,Cylinder1203,Cylinder1208,Cylinder1201,Cylinder1202,Cylinder1206]
  Placement = pos=(0,0,4) rot=(0,0,1;0.392699rad)
FEATURE [Part::Cut] Cut455
  Base = -> Tube111
  Tool = -> Compound900
FEATURE [Part::Compound] Compound901
  Links = -> [Box492,Box489,Box487,Box486,Box491,Box490,Box485,Box488]
  Placement = pos=(0,0,7) rot=(0,0,1;0.392699rad)
FEATURE [Part::Cut] Cut456
  Base = -> Cut455
  Tool = -> Compound901
FEATURE [Part::Compound] Compound902
  Links = -> [Cylinder1214,Cylinder1213,Cylinder1210,Cylinder1211,Cylinder1216,Cylinder1209,Cylinder1215,Cylinder1212]
  Placement = pos=(0,0,4) rot=(0,0,1;0.392699rad)
FEATURE [Part::Cut] Cut457
  Base = -> Tube112
  Tool = -> Compound902
FEATURE [Part::Compound] Compound903
  Links = -> [Box505,Box501,Box506,Box504,Box507,Box502,Box508,Box503]
  Placement = pos=(0,0,7) rot=(0,0,1;0.392699rad)
FEATURE [Part::FeaturePython] wormgear070  # WARN: FeaturePython — macro-defined, semantics opaque (R4)
  AttacherType = Attacher::AttachEngine3D
  Placement = pos=(0,0,0) rot=(0,0,-1;0.1309rad)
  beta = 38.7636
  clearance = 0.25
  diameter = 67.25
  head = 0
  height = 14
  module = 1.5
  pressure_angle = 20
  reverse_pitch = false
  teeth = 36
  version = 0.0.3
FEATURE [Part::Cut] Cut458
  Base = -> Cylinder1218
  Placement = pos=(0,0,21) rot=(0,0,1;0.258309rad)
  Tool = -> wormgear070
FEATURE [Part::FeaturePython] wormgear071  # WARN: FeaturePython — macro-defined, semantics opaque (R4)
  AttacherType = Attacher::AttachEngine3D
  Placement = pos=(0,0,0) rot=(0,0,1;0.10472rad)
  beta = 38.7636
  clearance = 0.25
  diameter = 67.25
  head = 0
  height = 14
  module = 1.5
  pressure_angle = 20
  reverse_pitch = true
  teeth = 36
  version = 0.0.3
FEATURE [Part::Cut] Cut459
  Base = -> Cylinder1217
  Placement = pos=(0,0,33) rot=(0,0,1;0.466876rad)
  Tool = -> wormgear071
FEATURE [Part::Cut] Cut460
  Base = -> Cut459
  Tool = -> Compound903
FEATURE [Part::Compound] Compound904
  Links = -> [Cut460,Cut458]
FEATURE [Part::FeaturePython] Tube113  # WARN: FeaturePython — macro-defined, semantics opaque (R4)
  AttacherType = Attacher::AttachEngine3D
  Height = 18.8
  InnerRadius = 46
  OuterRadius = 46.6
  Placement = pos=(0,0,21) rot=(0,0,1;0rad)
FEATURE [Part::Compound] Compound905  label="J-midi_slip-actuator-ring-m1.5"
  Links = -> [Tube113,Compound904,Cut457,Cut456]
FEATURE [Mesh::Feature] Mesh016  label="J-midi_encoder-belt-ring-A (Meshed)"
FEATURE [Mesh::Feature] Mesh017  label="J-midi_encoder-belt-ring_B (Meshed)"
FEATURE [Part::Cylinder] Cylinder1219  label="Válec1219"
  Angle = 360
  AttacherType = Attacher::AttachEngine3D
  Height = 8
  Radius = 36
FEATURE [Part::Cylinder] Cylinder1220  label="Válec1220"
  Angle = 360
  AttacherType = Attacher::AttachEngine3D
  Height = 6
  Placement = pos=(-22,0,2) rot=(0,0,1;0rad)
  Radius = 8
FEATURE [Part::Cylinder] Cylinder1221  label="Válec1221"
  Angle = 360
  AttacherType = Attacher::AttachEngine3D
  Height = 6
  Placement = pos=(11,19.0526,2) rot=(0,0,1;4.18879rad)
  Radius = 8
FEATURE [Part::Cylinder] Cylinder1222  label="Válec1222"
  Angle = 360
  AttacherType = Attacher::AttachEngine3D
  Height = 6
  Placement = pos=(11,-19.0526,2) rot=(0,0,1;2.0944rad)
  Radius = 8
FEATURE [Part::Cylinder] Cylinder1223  label="Válec1223"
  Angle = 360
  AttacherType = Attacher::AttachEngine3D
  Height = 60
  Placement = pos=(26,4,-6) rot=(0,0,1;0rad)
  Radius = 1.5
FEATURE [Part::Cylinder] Cylinder1224  label="Válec1224"
  Angle = 360
  AttacherType = Attacher::AttachEngine3D
  Height = 6
  Placement = pos=(0,0,2) rot=(0,0,1;0rad)
  Radius = 8
FEATURE [Part::Cylinder] Cylinder1225  label="Válec1225"
  Angle = 360
  AttacherType = Attacher::AttachEngine3D
  Height = 3
  Placement = pos=(26,-4,-6) rot=(0,0,1;0rad)
  Radius = 3
FEATURE [Part::Cylinder] Cylinder1226  label="Válec1226"
  Angle = 360
  AttacherType = Attacher::AttachEngine3D
  Height = 60
  Placement = pos=(26,-4,-6) rot=(0,0,1;0rad)
  Radius = 1.5
FEATURE [Part::Cylinder] Cylinder1227  label="Válec1227"
  Angle = 360
  AttacherType = Attacher::AttachEngine3D
  Height = 3
  Placement = pos=(26,4,-6) rot=(0,0,1;0rad)
  Radius = 3
FEATURE [Part::Cylinder] Cylinder1228  label="Válec1228"
  Angle = 360
  AttacherType = Attacher::AttachEngine3D
  Height = 1
  Placement = pos=(0,0,-1) rot=(0,0,1;0rad)
  Radius = 16
FEATURE [Part::Cylinder] Cylinder1229  label="Válec1229"
  Angle = 360
  AttacherType = Attacher::AttachEngine3D
  Height = 8
  Placement = pos=(0,0,-9) rot=(0,0,1;0rad)
  Radius = 16
FEATURE [Part::Compound] Compound906
  Links = -> [Cylinder1220,Cylinder1222,Cylinder1221,Cylinder1224]
FEATURE [Part::Compound] Compound907
  Links = -> [Cylinder1227,Cylinder1225]
  Placement = pos=(0,0,6) rot=(0,0,1;4.18879rad)
FEATURE [Part::Compound] Compound909
  Links = -> [Cylinder1227,Cylinder1225]
  Placement = pos=(0,0,6) rot=(0,0,1;0rad)
FEATURE [Part::Compound] Compound912
  Links = -> [Cylinder1223,Cylinder1226]
FEATURE [Part::Compound] Compound913
  Links = -> [Cylinder1223,Cylinder1226]
  Placement = pos=(0,0,0) rot=(0,0,1;4.18879rad)
FEATURE [Part::Compound] Compound914
  Links = -> [Cylinder1227,Cylinder1225]
  Placement = pos=(0,0,6) rot=(0,0,1;2.0944rad)
FEATURE [Part::Compound] Compound908
  Links = -> [Compound914,Compound907,Compound909]
FEATURE [Part::Compound] Compound915
  Links = -> [Cylinder1223,Cylinder1226]
  Placement = pos=(0,0,0) rot=(0,0,1;2.0944rad)
FEATURE [Part::Compound] Compound911
  Links = -> [Compound915,Compound913,Compound912]
FEATURE [Part::Chamfer] Chamfer032
  Base = -> Cylinder1229
  Edges = 1 edges r=1: [Edge3]
FEATURE [Part::Cut] Cut463
  Base = -> Cylinder1219
  Tool = -> Compound906
FEATURE [Part::Cut] Cut462
  Base = -> Cut463
  Tool = -> Compound911
FEATURE [Part::Cut] Cut461
  Base = -> Cut462
  Tool = -> Compound908
FEATURE [Part::FeaturePython] Tube114  # WARN: FeaturePython — macro-defined, semantics opaque (R4)
  AttacherType = Attacher::AttachEngine3D
  Height = 1
  InnerRadius = 7
  OuterRadius = 8
  Placement = pos=(-22,0,2) rot=(0,0,1;0rad)
FEATURE [Part::FeaturePython] Tube115  # WARN: FeaturePython — macro-defined, semantics opaque (R4)
  AttacherType = Attacher::AttachEngine3D
  Height = 1
  InnerRadius = 7
  OuterRadius = 8
  Placement = pos=(11,-19.0526,2) rot=(0,0,1;2.0944rad)
FEATURE [Part::FeaturePython] Tube116  # WARN: FeaturePython — macro-defined, semantics opaque (R4)
  AttacherType = Attacher::AttachEngine3D
  Height = 1
  InnerRadius = 7
  OuterRadius = 8
  Placement = pos=(0,0,2) rot=(0,0,1;4.18879rad)
FEATURE [Part::FeaturePython] Tube117  # WARN: FeaturePython — macro-defined, semantics opaque (R4)
  AttacherType = Attacher::AttachEngine3D
  Height = 1
  InnerRadius = 7
  OuterRadius = 8
  Placement = pos=(11,19.0526,2) rot=(0,0,1;4.18879rad)
FEATURE [Part::Compound] Compound910  label="J-midi_quikovina_fixo003"
  Links = -> [Tube114,Tube116,Tube115,Tube117,Cut461]
FEATURE [Part::Compound] Compound916  label="J-midi_slip-quikovina-fixo"
  Links = -> [Chamfer032,Cylinder1228,Compound910]
FEATURE [Part::Cylinder] Cylinder1230  label="Válec1230"
  Angle = 360
  AttacherType = Attacher::AttachEngine3D
  Height = 60
  Placement = pos=(41,0,-54) rot=(0,0,1;0rad)
  Radius = 1.5
FEATURE [Part::Cylinder] Cylinder1231  label="Válec1231"
  Angle = 360
  AttacherType = Attacher::AttachEngine3D
  Height = 60
  Placement = pos=(28.9914,28.9914,-54) rot=(0,0,1;0.785398rad)
  Radius = 1.5
FEATURE [Part::Cylinder] Cylinder1232  label="Válec1232"
  Angle = 360
  AttacherType = Attacher::AttachEngine3D
  Height = 60
  Placement = pos=(1.2e-14,-41,-54) rot=(0,0,-1;1.5708rad)
  Radius = 1.5
FEATURE [Part::Cylinder] Cylinder1233  label="Válec1233"
  Angle = 360
  AttacherType = Attacher::AttachEngine3D
  Height = 60
  Placement = pos=(28.9914,-28.9914,-54) rot=(0,0,-1;0.785398rad)
  Radius = 1.5
FEATURE [Part::Cylinder] Cylinder1234  label="Válec1234"
  Angle = 360
  AttacherType = Attacher::AttachEngine3D
  Height = 60
  Placement = pos=(-28.9914,-28.9914,-54) rot=(0,0,1;3.92699rad)
  Radius = 1.5
FEATURE [Part::Cylinder] Cylinder1235  label="Válec1235"
  Angle = 360
  AttacherType = Attacher::AttachEngine3D
  Height = 60
  Placement = pos=(-28.9914,28.9914,-54) rot=(0,0,1;2.35619rad)
  Radius = 1.5
FEATURE [Part::Cylinder] Cylinder1236  label="Válec1236"
  Angle = 360
  AttacherType = Attacher::AttachEngine3D
  Height = 60
  Placement = pos=(-4e-15,41,-54) rot=(0,0,1;1.5708rad)
  Radius = 1.5
FEATURE [Part::Cylinder] Cylinder1237  label="Válec1237"
  Angle = 360
  AttacherType = Attacher::AttachEngine3D
  Height = 60
  Placement = pos=(-41,-1.1e-14,-54) rot=(0,0,1;3.14159rad)
  Radius = 1.5
FEATURE [Part::Compound] Compound917
  Links = -> [Cylinder1231,Cylinder1236,Cylinder1235,Cylinder1237,Cylinder1234,Cylinder1232,Cylinder1233,Cylinder1230]
  Placement = pos=(0,0,-31) rot=(0,0,1;0.392699rad)
FEATURE [Part::FeaturePython] Tube118  # WARN: FeaturePython — macro-defined, semantics opaque (R4)
  AttacherType = Attacher::AttachEngine3D
  Height = 2
  InnerRadius = 12
  OuterRadius = 46
  Placement = pos=(0,0,-35) rot=(0,0,1;0rad)
FEATURE [Part::FeaturePython] Tube119  # WARN: FeaturePython — macro-defined, semantics opaque (R4)
  AttacherType = Attacher::AttachEngine3D
  Height = 9
  InnerRadius = 16.4
  OuterRadius = 32
  Placement = pos=(0,0,-33) rot=(0,0,1;0rad)
FEATURE [Part::Chamfer] Chamfer033
  Base = -> Tube119
  Edges = 1 edges r=1: [Edge4]
FEATURE [Part::FeaturePython] Tube120  # WARN: FeaturePython — macro-defined, semantics opaque (R4)
  AttacherType = Attacher::AttachEngine3D
  Height = 1
  InnerRadius = 23.6
  OuterRadius = 32
  Placement = pos=(0,0,-33) rot=(0,0,1;0rad)
FEATURE [Part::Cut] Cut464
  Base = -> Tube118
  Tool = -> Compound917
FEATURE [Part::Compound] Compound918  label="J-midi_slip-undermotor-undercover"
  Links = -> [Chamfer033,Cut464,Tube120]
  Placement = pos=(0,0,-32) rot=(0,0,1;0rad)
FEATURE [Part::Box] Box509  label="Krychle509"
  AttacherType = Attacher::AttachEngine3D
  Height = 60
  Length = 50
  Placement = pos=(0,0,8) rot=(0,0,1;1.36136rad)
  Width = 50
FEATURE [Part::FeaturePython] Tube121  # WARN: FeaturePython — macro-defined, semantics opaque (R4)
  AttacherType = Attacher::AttachEngine3D
  Height = 1
  InnerRadius = 7
  OuterRadius = 8
  Placement = pos=(-22,0,2) rot=(0,0,1;0rad)
FEATURE [Part::FeaturePython] Tube122  # WARN: FeaturePython — macro-defined, semantics opaque (R4)
  AttacherType = Attacher::AttachEngine3D
  Height = 51
  InnerRadius = 15
  OuterRadius = 30
  Placement = pos=(0,0,8) rot=(0,0,1;0rad)
FEATURE [Part::FeaturePython] Tube123  # WARN: FeaturePython — macro-defined, semantics opaque (R4)
  AttacherType = Attacher::AttachEngine3D
  Height = 1
  InnerRadius = 12
  OuterRadius = 20
  Placement = pos=(0,0,-1) rot=(0,0,1;0rad)
FEATURE [Part::FeaturePython] Tube124  # WARN: FeaturePython — macro-defined, semantics opaque (R4)
  AttacherType = Attacher::AttachEngine3D
  Height = 1
  InnerRadius = 7
  OuterRadius = 8
  Placement = pos=(11,19.0526,2) rot=(0,0,1;4.18879rad)
FEATURE [Part::FeaturePython] Tube125  # WARN: FeaturePython — macro-defined, semantics opaque (R4)
  AttacherType = Attacher::AttachEngine3D
  Height = 1
  InnerRadius = 7
  OuterRadius = 8
  Placement = pos=(11,-19.0526,2) rot=(0,0,1;2.0944rad)
FEATURE [Part::FeaturePython] Tube126  # WARN: FeaturePython — macro-defined, semantics opaque (R4)
  AttacherType = Attacher::AttachEngine3D
  Height = 8
  InnerRadius = 12
  OuterRadius = 20
  Placement = pos=(0,0,-9) rot=(0,0,1;0rad)
FEATURE [Part::Cylinder] Cylinder1238  label="Válec1238"
  Angle = 360
  AttacherType = Attacher::AttachEngine3D
  Height = 60
  Placement = pos=(26,-4,-6) rot=(0,0,1;0rad)
  Radius = 1.45
FEATURE [Part::Cylinder] Cylinder1239  label="Válec1239"
  Angle = 360
  AttacherType = Attacher::AttachEngine3D
  Height = 8
  Radius = 36
FEATURE [Part::Cylinder] Cylinder1240  label="Válec1240"
  Angle = 360
  AttacherType = Attacher::AttachEngine3D
  Height = 20
  Placement = pos=(0,0,-4) rot=(0,0,1;0rad)
  Radius = 12
FEATURE [Part::Cut] Cut469
  Base = -> Cylinder1239
  Tool = -> Cylinder1240
FEATURE [Part::Box] Box510  label="Krychle510"
  AttacherType = Attacher::AttachEngine3D
  Height = 60
  Length = 50
  Placement = pos=(0,0,8) rot=(0,0,-1;0.837758rad)
  Width = 50
FEATURE [Part::Cylinder] Cylinder1241  label="Válec1241"
  Angle = 360
  AttacherType = Attacher::AttachEngine3D
  Height = 80
  Placement = pos=(26,4,-6) rot=(0,0,1;0rad)
  Radius = 1.45
FEATURE [Part::Cylinder] Cylinder1242  label="Válec1242"
  Angle = 360
  AttacherType = Attacher::AttachEngine3D
  Height = 80
  Placement = pos=(26,-4,-6) rot=(0,0,1;0rad)
  Radius = 1.45
FEATURE [Part::Cylinder] Cylinder1243  label="Válec1243"
  Angle = 360
  AttacherType = Attacher::AttachEngine3D
  Height = 3
  Placement = pos=(26,4,-6) rot=(0,0,1;0rad)
  Radius = 3
FEATURE [Part::Cylinder] Cylinder1244  label="Válec1244"
  Angle = 360
  AttacherType = Attacher::AttachEngine3D
  Height = 6
  Placement = pos=(11,-19.0526,2) rot=(0,0,1;2.0944rad)
  Radius = 8
FEATURE [Part::Cylinder] Cylinder1245  label="Válec1245"
  Angle = 360
  AttacherType = Attacher::AttachEngine3D
  Height = 60
  Placement = pos=(26,4,-6) rot=(0,0,1;0rad)
  Radius = 1.45
FEATURE [Part::Compound] Compound921
  Links = -> [Cylinder1245,Cylinder1238]
  Placement = pos=(0,0,0) rot=(0,0,1;4.18879rad)
FEATURE [Part::Cylinder] Cylinder1246  label="Válec1246"
  Angle = 360
  AttacherType = Attacher::AttachEngine3D
  Height = 6
  Placement = pos=(11,19.0526,2) rot=(0,0,1;4.18879rad)
  Radius = 8
FEATURE [Part::Cylinder] Cylinder1247  label="Válec1247"
  Angle = 360
  AttacherType = Attacher::AttachEngine3D
  Height = 3
  Placement = pos=(26,-4,-6) rot=(0,0,1;0rad)
  Radius = 3
FEATURE [Part::Box] Box511  label="Krychle511"
  AttacherType = Attacher::AttachEngine3D
  Height = 60
  Length = 50
  Placement = pos=(0,0,8) rot=(0,0,1;2.61799rad)
  Width = 100
FEATURE [Part::Cylinder] Cylinder1248  label="Válec1248"
  Angle = 360
  AttacherType = Attacher::AttachEngine3D
  Height = 6
  Placement = pos=(-22,0,2) rot=(0,0,1;0rad)
  Radius = 8
FEATURE [Part::Box] Box512  label="Krychle512"
  AttacherType = Attacher::AttachEngine3D
  Height = 60
  Length = 50
  Placement = pos=(0,0,8) rot=(0,0,1;4.18879rad)
  Width = 100
FEATURE [Part::Compound] Compound923
  Links = -> [Cylinder1245,Cylinder1238]
FEATURE [Part::Compound] Compound924
  Links = -> [Cylinder1245,Cylinder1238]
  Placement = pos=(0,0,0) rot=(0,0,1;2.0944rad)
FEATURE [Part::Compound] Compound925
  Links = -> [Compound924,Compound921,Compound923]
FEATURE [Part::Compound] Compound926
  Links = -> [Tube125,Tube124,Tube121]
FEATURE [Part::Compound] Compound928
  Links = -> [Cylinder1241,Cylinder1242]
  Placement = pos=(0,0,0) rot=(0,0,1;1.0472rad)
FEATURE [Part::Compound] Compound929
  Links = -> [Cylinder1243,Cylinder1247]
  Placement = pos=(0,0,6) rot=(0,0,1;4.18879rad)
FEATURE [Part::Compound] Compound930
  Links = -> [Cylinder1248,Cylinder1244,Cylinder1246]
FEATURE [Part::Compound] Compound931
  Links = -> [Cylinder1243,Cylinder1247]
  Placement = pos=(0,0,6) rot=(0,0,1;0rad)
FEATURE [Part::Compound] Compound932
  Links = -> [Cylinder1243,Cylinder1247]
  Placement = pos=(0,0,6) rot=(0,0,1;2.0944rad)
FEATURE [Part::Compound] Compound920
  Links = -> [Compound932,Compound929,Compound931]
FEATURE [Part::Cut] Cut470
  Base = -> Tube122
  Tool = -> Box512
FEATURE [Part::Cut] Cut471
  Base = -> Cut470
  Tool = -> Box511
FEATURE [Part::Cut] Cut472
  Base = -> Cut469
  Tool = -> Compound930
FEATURE [Part::Cut] Cut467
  Base = -> Cut472
  Tool = -> Compound920
FEATURE [Part::Cut] Cut474
  Base = -> Cut467
  Tool = -> Compound925
FEATURE [Part::Cut] Cut475
  Base = -> Cut471
  Tool = -> Box510
FEATURE [Part::Cut] Cut466
  Base = -> Cut475
  Tool = -> Box509
FEATURE [Part::Cut] Cut465
  Base = -> Cut466
  Placement = pos=(0,0,0) rot=(0,0,-1;1.0472rad)
  Tool = -> Compound928
FEATURE [Part::Cut] Cut468
  Base = -> Cut466
  Placement = pos=(0,0,0) rot=(0,0,1;3.14159rad)
  Tool = -> Compound928
FEATURE [Part::Cut] Cut473
  Base = -> Cut466
  Placement = pos=(0,0,0) rot=(0,0,1;1.0472rad)
  Tool = -> Compound928
FEATURE [Part::Compound] Compound919
  Links = -> [Cut465,Cut468,Cut473]
FEATURE [Part::Compound] Compound927  label="J-midi_pikovina003"
  Links = -> [Compound919,Cut474,Compound926]
FEATURE [Part::Compound] Compound922  label="J-midi_pikovina_fixo003"
  Links = -> [Tube126,Tube123,Compound927]
FEATURE [Part::Chamfer] Chamfer034  label="J-midi-deep_slip-pikovina_fixo"
  Base = -> Compound922
  Edges = 1 edges r=1: [Edge3]
  Placement = pos=(0,0,100) rot=(0,0,1;0rad)
FEATURE [Part::Cylinder] Cylinder1249  label="Válec1249"
  Angle = 360
  AttacherType = Attacher::AttachEngine3D
  Height = 60
  Placement = pos=(1.2e-14,-41,-54) rot=(0,0,-1;1.5708rad)
  Radius = 1.5
FEATURE [Part::Cylinder] Cylinder1250  label="Válec1250"
  Angle = 360
  AttacherType = Attacher::AttachEngine3D
  Height = 60
  Placement = pos=(-4e-15,41,-54) rot=(0,0,1;1.5708rad)
  Radius = 1.5
FEATURE [Part::Cylinder] Cylinder1251  label="Válec1251"
  Angle = 360
  AttacherType = Attacher::AttachEngine3D
  Height = 60
  Placement = pos=(41,0,-54) rot=(0,0,1;0rad)
  Radius = 1.5
FEATURE [Part::Cylinder] Cylinder1252  label="Válec1252"
  Angle = 360
  AttacherType = Attacher::AttachEngine3D
  Height = 60
  Placement = pos=(-28.9914,-28.9914,-54) rot=(0,0,1;3.92699rad)
  Radius = 1.5
FEATURE [Part::Cylinder] Cylinder1253  label="Válec1253"
  Angle = 360
  AttacherType = Attacher::AttachEngine3D
  Height = 60
  Placement = pos=(-41,-1.1e-14,-54) rot=(0,0,1;3.14159rad)
  Radius = 1.5
FEATURE [Part::Cylinder] Cylinder1254  label="Válec1254"
  Angle = 360
  AttacherType = Attacher::AttachEngine3D
  Height = 60
  Placement = pos=(28.9914,-28.9914,-54) rot=(0,0,-1;0.785398rad)
  Radius = 1.5
FEATURE [Part::Cylinder] Cylinder1255  label="Válec1255"
  Angle = 360
  AttacherType = Attacher::AttachEngine3D
  Height = 60
  Placement = pos=(28.9914,28.9914,-54) rot=(0,0,1;0.785398rad)
  Radius = 1.5
FEATURE [Part::Cylinder] Cylinder1256  label="Válec1256"
  Angle = 360
  AttacherType = Attacher::AttachEngine3D
  Height = 60
  Placement = pos=(-28.9914,28.9914,-54) rot=(0,0,1;2.35619rad)
  Radius = 1.5
FEATURE [Part::Compound] Compound933
  Links = -> [Cylinder1255,Cylinder1250,Cylinder1256,Cylinder1253,Cylinder1252,Cylinder1249,Cylinder1254,Cylinder1251]
  Placement = pos=(0,0,-31) rot=(0,0,1;0.392699rad)
FEATURE [Part::FeaturePython] Tube127  # WARN: FeaturePython — macro-defined, semantics opaque (R4)
  AttacherType = Attacher::AttachEngine3D
  Height = 2
  InnerRadius = 12
  OuterRadius = 46
  Placement = pos=(0,0,-35) rot=(0,0,1;0rad)
FEATURE [Part::FeaturePython] Tube128  # WARN: FeaturePython — macro-defined, semantics opaque (R4)
  AttacherType = Attacher::AttachEngine3D
  Height = 1
  InnerRadius = 20.05
  OuterRadius = 32
  Placement = pos=(0,0,-33) rot=(0,0,1;0rad)
FEATURE [Part::FeaturePython] Tube129  # WARN: FeaturePython — macro-defined, semantics opaque (R4)
  AttacherType = Attacher::AttachEngine3D
  Height = 9
  InnerRadius = 20.05
  OuterRadius = 32
  Placement = pos=(0,0,-33) rot=(0,0,1;0rad)
FEATURE [Part::Chamfer] Chamfer035
  Base = -> Tube129
  Edges = 1 edges r=1: [Edge4]
FEATURE [Part::Cut] Cut476
  Base = -> Tube127
  Tool = -> Compound933
FEATURE [Part::Compound] Compound934  label="J-midi_slip-undermotor-undercover_v2"
  Links = -> [Chamfer035,Cut476,Tube128]
  Placement = pos=(0,0,-32) rot=(0,0,1;0rad)
FEATURE [Part::Chamfer] Chamfer  label="J-midi-deep_pikovina_fixo"
  Base = -> Chamfer027
  Edges = 1 edges r=2: [Edge71]
FEATURE [Part::Chamfer] Chamfer036  label="J-midi-deep_quikovina_fixo"
  Base = -> Compound667
  Edges = 1 edges r=2: [Edge35]
